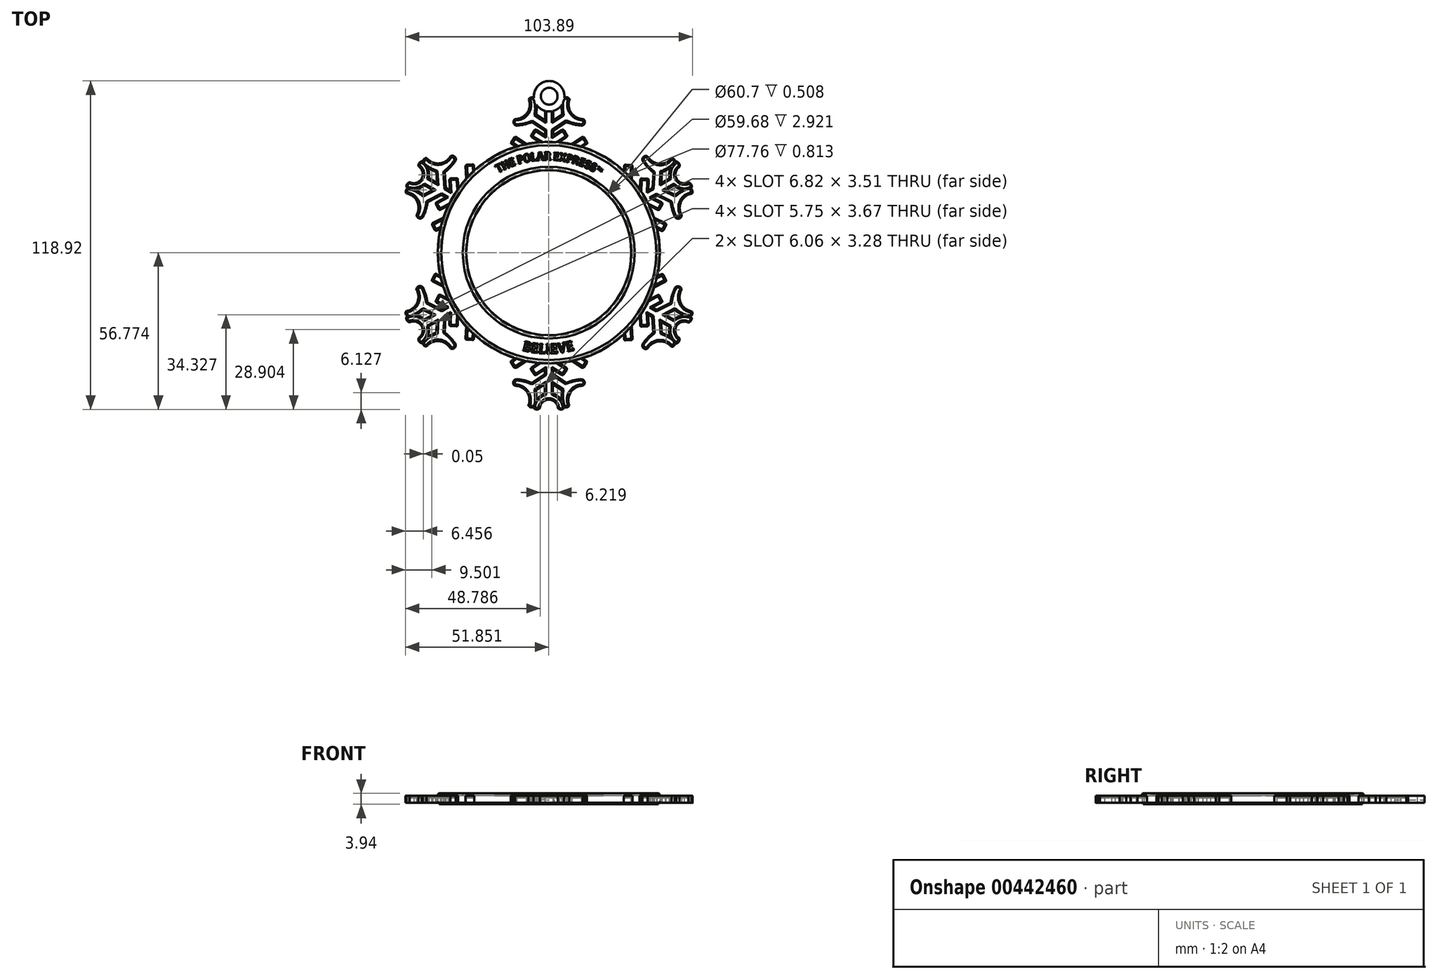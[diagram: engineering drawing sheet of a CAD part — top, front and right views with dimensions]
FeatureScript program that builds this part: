
annotation { "Feature Type Name" : "Feature", "Feature Type Description" : "" }
export const myFeature = defineFeature(function(context is Context, id is Id, definition is map)
    precondition{}
    {
        {
            var Q0;
            Q0=qCreatedBy(makeId("Top.planeOp"),FACE);
            var sketch = newSketch(context, id + "F0", { "sketchPlane" : qUnion([Q0])});
            skLineSegment(sketch, "E0.bottom", {"start": v(-89.67, 62.48) * mm, "end": v(13.76, 62.48) * mm});
            skLineSegment(sketch, "E0.top", {"start": v(-89.67, -44.14) * mm, "end": v(13.76, -44.14) * mm});
            skLineSegment(sketch, "E0.left", {"start": v(-89.67, 62.48) * mm, "end": v(-89.67, -44.14) * mm});
            skLineSegment(sketch, "E0.right", {"start": v(13.76, 62.48) * mm, "end": v(13.76, -44.14) * mm});
            skSolve(sketch);
        }
        {
            var Q0;
            Q0=makeQuery(id+"F0.imprint","IMPRINT",FACE,{"disambiguationData":[TD([[makeQuery(id+"F0.imprint","IMPRINT",EDGE,{"derivedFrom":sQuery(id+"F0.wireOp",EDGE,"E0.bottom")}),-1.0]])]});
            var sketch = newSketch(context, id + "F1", { "sketchPlane" : qUnion([Q0])});
            skLineSegment(sketch, "E1", {"start": v(-37.72, -43.99) * mm, "end": v(-37.72, 64.24) * mm});
            skLineSegment(sketch, "E2", {"start": v(-50.86, -34.68) * mm, "end": v(-48.2, -32.93) * mm});
            skLineSegment(sketch, "E3", {"start": v(-48.2, -32.93) * mm, "end": v(-37.72, -32.93) * mm});
            skLineSegment(sketch, "E4", {"start": v(-49.18, -37.24) * mm, "end": v(-45.3, -34.68) * mm});
            skLineSegment(sketch, "E5", {"start": v(-45.3, -34.68) * mm, "end": v(-41.3, -35.15) * mm});
            skLineSegment(sketch, "E6", {"start": v(-41.3, -35.15) * mm, "end": v(-41.47, -35.86) * mm});
            skLineSegment(sketch, "E7", {"start": v(-41.47, -35.86) * mm, "end": v(-43.84, -37.4) * mm});
            skLineSegment(sketch, "E8", {"start": v(-42.17, -39.97) * mm, "end": v(-39.2, -38.03) * mm});
            skLineSegment(sketch, "E9", {"start": v(-39.2, -38.03) * mm, "end": v(-39.2, -39.79) * mm});
            skLineSegment(sketch, "E10", {"start": v(-39.2, -39.79) * mm, "end": v(-43.97, -42.95) * mm});
            skLineSegment(sketch, "E11", {"start": v(-50.86, -34.68) * mm, "end": v(-51.7, -35.23) * mm});
            skLineSegment(sketch, "E12", {"start": v(-49.18, -37.24) * mm, "end": v(-50.01, -37.79) * mm});
            skLineSegment(sketch, "E13", {"start": v(-51.7, -35.23) * mm, "end": v(-50.01, -37.79) * mm});
            skLineSegment(sketch, "E14", {"start": v(-43.84, -37.4) * mm, "end": v(-44.45, -37.8) * mm});
            skLineSegment(sketch, "E15", {"start": v(-44.45, -37.8) * mm, "end": v(-42.8, -40.34) * mm});
            skLineSegment(sketch, "E16", {"start": v(-42.17, -39.97) * mm, "end": v(-42.78, -40.37) * mm});
            skLineSegment(sketch, "E17", {"start": v(-42.8, -40.34) * mm, "end": v(-42.78, -40.37) * mm});
            skLineSegment(sketch, "E18.trimOffspring", {"start": v(-39.2, -43.46) * mm, "end": v(-39.2, -46.98) * mm});
            skArc(sketch, "E19", {"start": v(-39.2, -46.98) * mm, "mid": v(-41.06, -47.9) * mm, "end": v(-42.34, -49.52) * mm});
            skLineSegment(sketch, "E20", {"start": v(-37.72, -43.99) * mm, "end": v(-37.72, -49.05) * mm});
            skArc(sketch, "E21", {"start": v(-37.72, -49.05) * mm, "mid": v(-39.97, -49.95) * mm, "end": v(-40.99, -52.14) * mm});
            skArc(sketch, "E22", {"start": v(-45.12, -51.18) * mm, "mid": v(-45.67, -46.32) * mm, "end": v(-50, -44.04) * mm});
            skLineSegment(sketch, "E23", {"start": v(-39.2, -43.46) * mm, "end": v(-42.47, -45.63) * mm});
            skArc(sketch, "E24", {"start": v(-42.34, -49.52) * mm, "mid": v(-42.28, -47.57) * mm, "end": v(-42.47, -45.63) * mm});
            skArc(sketch, "E25", {"start": v(-43.97, -42.95) * mm, "mid": v(-46.67, -42.07) * mm, "end": v(-49.48, -41.65) * mm});
            skArc(sketch, "E26", {"start": v(-49.48, -41.65) * mm, "mid": v(-50.63, -42.65) * mm, "end": v(-50, -44.04) * mm});
            skArc(sketch, "E27", {"start": v(-45.12, -51.18) * mm, "mid": v(-44.22, -51.87) * mm, "end": v(-43.13, -51.55) * mm});
            skLineSegment(sketch, "E28", {"start": v(-43.13, -51.55) * mm, "end": v(-43.23, -52.11) * mm});
            skArc(sketch, "E29", {"start": v(-43.23, -52.11) * mm, "mid": v(-42.12, -52.62) * mm, "end": v(-40.99, -52.14) * mm});
            skSolve(sketch);
        }
        {
            var Q0;
            Q0 = qSketchRegion(id + "F1", true);
            extrude(context, id + "F2", {"entities" : qUnion([Q0]), "depth" : 1.52 * mm});
        }
        {
            var Q0;
            Q0=makeQuery(id+"F2.opExtrude","SWEPT_EDGE",EDGE,{"disambiguationData":[OSD([sQuery(id+"F1.wireOp",EDGE,"E11"),sQuery(id+"F1.wireOp",EDGE,"E13")])]});
            var Q1;
            Q1=makeQuery(id+"F2.opExtrude","SWEPT_EDGE",EDGE,{"disambiguationData":[OSD([sQuery(id+"F1.wireOp",EDGE,"E12"),sQuery(id+"F1.wireOp",EDGE,"E13")])]});
            var Q2;
            Q2=makeQuery(id+"F2.opExtrude","SWEPT_EDGE",EDGE,{"disambiguationData":[OSD([sQuery(id+"F1.wireOp",EDGE,"E14"),sQuery(id+"F1.wireOp",EDGE,"E15")])]});
            var Q3;
            Q3=makeQuery(id+"F2.opExtrude","SWEPT_EDGE",EDGE,{"disambiguationData":[OSD([sQuery(id+"F1.wireOp",EDGE,"E16"),sQuery(id+"F1.wireOp",EDGE,"E17")])]});
            fillet(context, id + "F3", {"entities" : qUnion([Q0, Q1, Q2, Q3]), "radius" : 0.5 * mm, "tangentPropagation" : true, "allowEdgeOverflow" : false});
        }
        {
            var Q0;
            Q0=makeQuery(id+"F2.opExtrude","SWEPT_BODY",BODY,{"disambiguationData":[OSD([sQuery(id+"F1.wireOp",EDGE,"E1"),sQuery(id+"F1.wireOp",EDGE,"E2"),sQuery(id+"F1.wireOp",EDGE,"E3"),sQuery(id+"F1.wireOp",EDGE,"E4"),sQuery(id+"F1.wireOp",EDGE,"E5"),sQuery(id+"F1.wireOp",EDGE,"E6"),sQuery(id+"F1.wireOp",EDGE,"E7"),sQuery(id+"F1.wireOp",EDGE,"E8"),sQuery(id+"F1.wireOp",EDGE,"E9"),sQuery(id+"F1.wireOp",EDGE,"E10"),sQuery(id+"F1.wireOp",EDGE,"E11"),sQuery(id+"F1.wireOp",EDGE,"E12"),sQuery(id+"F1.wireOp",EDGE,"E13"),sQuery(id+"F1.wireOp",EDGE,"E14"),sQuery(id+"F1.wireOp",EDGE,"E15"),sQuery(id+"F1.wireOp",EDGE,"E16"),sQuery(id+"F1.wireOp",EDGE,"E17"),sQuery(id+"F1.wireOp",EDGE,"E18.trimOffspring"),sQuery(id+"F1.wireOp",EDGE,"E19"),sQuery(id+"F1.wireOp",EDGE,"E20"),sQuery(id+"F1.wireOp",EDGE,"E21"),sQuery(id+"F1.wireOp",EDGE,"E22"),sQuery(id+"F1.wireOp",EDGE,"E23"),sQuery(id+"F1.wireOp",EDGE,"E24"),sQuery(id+"F1.wireOp",EDGE,"E25"),sQuery(id+"F1.wireOp",EDGE,"E26"),sQuery(id+"F1.wireOp",EDGE,"E27"),sQuery(id+"F1.wireOp",EDGE,"E28"),sQuery(id+"F1.wireOp",EDGE,"E29")])]});
            var Q1;
            Q1=makeQuery(id+"F2.opExtrude","SWEPT_FACE",FACE,{"disambiguationData":[OSD([sQuery(id+"F1.wireOp",EDGE,"E1"),sQuery(id+"F1.wireOp",EDGE,"E20")])]});
            mirror(context, id + "F4", {"operationType" : NewBodyOperationType.ADD, "entities" : qUnion([Q0]), "mirrorPlane" : qUnion([Q1])});
        }
        {
            var Q0;
            {var subQ0=makeQuery(id+"F2.opExtrude","CAP_FACE",FACE,{"disambiguationData":[OSD([sQuery(id+"F1.wireOp",EDGE,"E1"),sQuery(id+"F1.wireOp",EDGE,"E2"),sQuery(id+"F1.wireOp",EDGE,"E3"),sQuery(id+"F1.wireOp",EDGE,"E4"),sQuery(id+"F1.wireOp",EDGE,"E5"),sQuery(id+"F1.wireOp",EDGE,"E6"),sQuery(id+"F1.wireOp",EDGE,"E7"),sQuery(id+"F1.wireOp",EDGE,"E8"),sQuery(id+"F1.wireOp",EDGE,"E9"),sQuery(id+"F1.wireOp",EDGE,"E10"),sQuery(id+"F1.wireOp",EDGE,"E11"),sQuery(id+"F1.wireOp",EDGE,"E12"),sQuery(id+"F1.wireOp",EDGE,"E13"),sQuery(id+"F1.wireOp",EDGE,"E14"),sQuery(id+"F1.wireOp",EDGE,"E15"),sQuery(id+"F1.wireOp",EDGE,"E16"),sQuery(id+"F1.wireOp",EDGE,"E17"),sQuery(id+"F1.wireOp",EDGE,"E18.trimOffspring"),sQuery(id+"F1.wireOp",EDGE,"E19"),sQuery(id+"F1.wireOp",EDGE,"E20"),sQuery(id+"F1.wireOp",EDGE,"E21"),sQuery(id+"F1.wireOp",EDGE,"E22"),sQuery(id+"F1.wireOp",EDGE,"E23"),sQuery(id+"F1.wireOp",EDGE,"E24"),sQuery(id+"F1.wireOp",EDGE,"E25"),sQuery(id+"F1.wireOp",EDGE,"E26"),sQuery(id+"F1.wireOp",EDGE,"E27"),sQuery(id+"F1.wireOp",EDGE,"E28"),sQuery(id+"F1.wireOp",EDGE,"E29")])],"isStart":false});Q0=makeQuery(id+"F4.boolean.opBoolean","MERGE",FACE,{"derivedFrom":[subQ0,makeQuery(id+"F4.opPattern","COPY",FACE,{"derivedFrom":subQ0,"instanceName":"1"})]});}
            var sketch = newSketch(context, id + "F5", { "sketchPlane" : qUnion([Q0])});
            skLineSegment(sketch, "E30", {"start": v(-38.68, -37.09) * mm, "end": v(-38.68, -40.03) * mm});
            skLineSegment(sketch, "E31", {"start": v(-38.68, -47.34) * mm, "end": v(-38.68, -42.57) * mm});
            skLineSegment(sketch, "E32", {"start": v(-38.68, -40.03) * mm, "end": v(-43.93, -43.46) * mm});
            skLineSegment(sketch, "E33", {"start": v(-38.68, -42.57) * mm, "end": v(-42.98, -45.42) * mm});
            skLineSegment(sketch, "E34", {"start": v(-40.7, -35.88) * mm, "end": v(-43.4, -37.66) * mm});
            skLineSegment(sketch, "E35", {"start": v(-43.4, -37.66) * mm, "end": v(-43.77, -37.9) * mm});
            skLineSegment(sketch, "E36", {"start": v(-43.77, -37.9) * mm, "end": v(-42.61, -39.7) * mm});
            skLineSegment(sketch, "E37", {"start": v(-38.68, -37.09) * mm, "end": v(-42.61, -39.7) * mm});
            skLineSegment(sketch, "E38.trimOffspring", {"start": v(-38.68, -42.57) * mm, "end": v(-38.68, -47.34) * mm});
            skArc(sketch, "E39", {"start": v(-43.93, -43.46) * mm, "mid": v(-46.6, -42.57) * mm, "end": v(-49.38, -42.12) * mm});
            skArc(sketch, "E40", {"start": v(-49.38, -42.12) * mm, "mid": v(-50.03, -42.74) * mm, "end": v(-49.71, -43.58) * mm});
            skArc(sketch, "E41", {"start": v(-42.9, -50.88) * mm, "mid": v(-42.7, -48.15) * mm, "end": v(-42.98, -45.42) * mm});
            skArc(sketch, "E42", {"start": v(-44.52, -51) * mm, "mid": v(-45.27, -46) * mm, "end": v(-49.71, -43.58) * mm});
            skArc(sketch, "E43", {"start": v(-44.52, -51) * mm, "mid": v(-43.68, -51.33) * mm, "end": v(-42.9, -50.88) * mm});
            skArc(sketch, "E44", {"start": v(-37.76, -48.56) * mm, "mid": v(-40.27, -49.56) * mm, "end": v(-41.5, -51.96) * mm});
            skArc(sketch, "E45", {"start": v(-38.68, -47.34) * mm, "mid": v(-41.04, -48.47) * mm, "end": v(-42.51, -50.63) * mm});
            skArc(sketch, "E46", {"start": v(-42.72, -51.96) * mm, "mid": v(-42.11, -52.15) * mm, "end": v(-41.5, -51.96) * mm});
            skArc(sketch, "E47", {"start": v(-42.51, -50.63) * mm, "mid": v(-42.65, -51.3) * mm, "end": v(-42.72, -51.96) * mm});
            skLineSegment(sketch, "E48", {"start": v(-49.87, -37.08) * mm, "end": v(-45.7, -34.34) * mm});
            skLineSegment(sketch, "E49", {"start": v(-45.7, -34.34) * mm, "end": v(-48.36, -33.8) * mm});
            skLineSegment(sketch, "E50", {"start": v(-48.36, -33.8) * mm, "end": v(-48.45, -33.67) * mm});
            skLineSegment(sketch, "E51", {"start": v(-49.87, -37.08) * mm, "end": v(-51, -35.37) * mm});
            skLineSegment(sketch, "E52", {"start": v(-51, -35.37) * mm, "end": v(-48.45, -33.67) * mm});
            skLineSegment(sketch, "E53", {"start": v(-37.76, -48.56) * mm, "end": v(-37.58, -34.16) * mm});
            skLineSegment(sketch, "E54", {"start": v(-37.58, -34.16) * mm, "end": v(-40.7, -35.88) * mm});
            skSolve(sketch);
        }
        {
            var Q0;
            Q0 = qSketchRegion(id + "F5", true);
            extrude(context, id + "F6", {"entities" : qUnion([Q0]), "operationType" : NewBodyOperationType.REMOVE, "oppositeDirection" : true, "depth" : 0.76 * mm});
        }
        {
            var Q0;
            {var subQ0=makeQuery(id+"F2.opExtrude","CAP_FACE",FACE,{"disambiguationData":[OSD([sQuery(id+"F1.wireOp",EDGE,"E1"),sQuery(id+"F1.wireOp",EDGE,"E2"),sQuery(id+"F1.wireOp",EDGE,"E3"),sQuery(id+"F1.wireOp",EDGE,"E4"),sQuery(id+"F1.wireOp",EDGE,"E5"),sQuery(id+"F1.wireOp",EDGE,"E6"),sQuery(id+"F1.wireOp",EDGE,"E7"),sQuery(id+"F1.wireOp",EDGE,"E8"),sQuery(id+"F1.wireOp",EDGE,"E9"),sQuery(id+"F1.wireOp",EDGE,"E10"),sQuery(id+"F1.wireOp",EDGE,"E11"),sQuery(id+"F1.wireOp",EDGE,"E12"),sQuery(id+"F1.wireOp",EDGE,"E13"),sQuery(id+"F1.wireOp",EDGE,"E14"),sQuery(id+"F1.wireOp",EDGE,"E15"),sQuery(id+"F1.wireOp",EDGE,"E16"),sQuery(id+"F1.wireOp",EDGE,"E17"),sQuery(id+"F1.wireOp",EDGE,"E18.trimOffspring"),sQuery(id+"F1.wireOp",EDGE,"E19"),sQuery(id+"F1.wireOp",EDGE,"E20"),sQuery(id+"F1.wireOp",EDGE,"E21"),sQuery(id+"F1.wireOp",EDGE,"E22"),sQuery(id+"F1.wireOp",EDGE,"E23"),sQuery(id+"F1.wireOp",EDGE,"E24"),sQuery(id+"F1.wireOp",EDGE,"E25"),sQuery(id+"F1.wireOp",EDGE,"E26"),sQuery(id+"F1.wireOp",EDGE,"E27"),sQuery(id+"F1.wireOp",EDGE,"E28"),sQuery(id+"F1.wireOp",EDGE,"E29")])],"isStart":false});Q0=makeQuery(id+"F4.boolean.opBoolean","MERGE",FACE,{"derivedFrom":[subQ0,makeQuery(id+"F4.opPattern","COPY",FACE,{"derivedFrom":subQ0,"instanceName":"1"})]});}
            var sketch = newSketch(context, id + "F7", { "sketchPlane" : qUnion([Q0])});
            skLineSegment(sketch, "E55", {"start": v(-37.58, -34.16) * mm, "end": v(-31.7, -37.88) * mm});
            skLineSegment(sketch, "E56", {"start": v(-31.7, -37.88) * mm, "end": v(-32.82, -39.66) * mm});
            skLineSegment(sketch, "E57", {"start": v(-32.82, -39.66) * mm, "end": v(-36.7, -37.23) * mm});
            skLineSegment(sketch, "E58.right", {"start": v(-36.7, -37.23) * mm, "end": v(-36.7, -40.03) * mm});
            skPoint(sketch, "E59.start.orphan", {"position": v(-37.58, -36.67) * mm});
            skLineSegment(sketch, "E60", {"start": v(-37.76, -47.63) * mm, "end": v(-38.17, -35.66) * mm});
            skLineSegment(sketch, "E61", {"start": v(-38.17, -35.66) * mm, "end": v(-37.58, -34.16) * mm});
            skLineSegment(sketch, "E62", {"start": v(-36.7, -40.03) * mm, "end": v(-31.5, -43.46) * mm});
            skPoint(sketch, "E63.end.orphan", {"position": v(-36.25, -42.3) * mm});
            skPoint(sketch, "E64.end.orphan", {"position": v(-36.7, -42.95) * mm});
            skLineSegment(sketch, "E65", {"start": v(-36.7, -42.58) * mm, "end": v(-32.35, -45.36) * mm});
            skArc(sketch, "E66", {"start": v(-26.04, -42.12) * mm, "mid": v(-28.85, -42.5) * mm, "end": v(-31.5, -43.46) * mm});
            skArc(sketch, "E67", {"start": v(-32.35, -45.36) * mm, "mid": v(-32.64, -48.26) * mm, "end": v(-32.07, -51.11) * mm});
            skArc(sketch, "E68", {"start": v(-25.6, -43.58) * mm, "mid": v(-25.28, -42.69) * mm, "end": v(-26.04, -42.12) * mm});
            skArc(sketch, "E69", {"start": v(-32.07, -51.11) * mm, "mid": v(-31.44, -51.43) * mm, "end": v(-30.9, -50.98) * mm});
            skArc(sketch, "E70", {"start": v(-25.6, -43.58) * mm, "mid": v(-30.18, -45.9) * mm, "end": v(-30.9, -50.98) * mm});
            skLineSegment(sketch, "E71", {"start": v(-41.5, -51.96) * mm, "end": v(-29.9, -51.96) * mm});
            skArc(sketch, "E72", {"start": v(-34.1, -51.96) * mm, "mid": v(-35.24, -49.51) * mm, "end": v(-37.76, -48.56) * mm});
            skLineSegment(sketch, "E73", {"start": v(-38.68, -47.34) * mm, "end": v(-37.77, -47.34) * mm});
            skArc(sketch, "E74", {"start": v(-32.7, -51.96) * mm, "mid": v(-34.01, -49.06) * mm, "end": v(-36.7, -47.34) * mm});
            skArc(sketch, "E75", {"start": v(-34.1, -51.96) * mm, "mid": v(-33.4, -52.23) * mm, "end": v(-32.7, -51.96) * mm});
            skLineSegment(sketch, "E76.trimOffspring", {"start": v(-36.7, -42.58) * mm, "end": v(-36.7, -47.34) * mm});
            skLineSegment(sketch, "E77", {"start": v(-29.73, -34.22) * mm, "end": v(-25.56, -36.96) * mm});
            skLineSegment(sketch, "E78", {"start": v(-25.56, -36.96) * mm, "end": v(-24.45, -35.37) * mm});
            skLineSegment(sketch, "E79", {"start": v(-24.45, -35.37) * mm, "end": v(-27.72, -33.27) * mm});
            skLineSegment(sketch, "E80", {"start": v(-27.72, -33.27) * mm, "end": v(-29.73, -34.22) * mm});
            skSolve(sketch);
        }
        {
            var Q0;
            Q0 = qSketchRegion(id + "F7", true);
            var Q1;
            Q1=makeQuery(id+"F7.imprint","IMPRINT",FACE,{"disambiguationData":[TD([[makeQuery(id+"F7.imprint","IMPRINT",EDGE,{"derivedFrom":sQuery(id+"F7.wireOp",EDGE,"E55")}),-1.0]])]});
            extrude(context, id + "F8", {"entities" : qUnion([Q0, Q1]), "operationType" : NewBodyOperationType.REMOVE, "oppositeDirection" : true, "depth" : 0.76 * mm});
        }
        {
            var Q0;
            Q0=makeQuery(id+"F8.boolean.opBoolean","COPY",EDGE,{"derivedFrom":makeQuery(id+"F8.opExtrude","SWEPT_EDGE",EDGE,{"disambiguationData":[OSD([sQuery(id+"F7.wireOp",EDGE,"E78"),sQuery(id+"F7.wireOp",EDGE,"E79")])]})});
            var Q1;
            Q1=makeQuery(id+"F8.boolean.opBoolean","COPY",EDGE,{"derivedFrom":makeQuery(id+"F8.opExtrude","SWEPT_EDGE",EDGE,{"disambiguationData":[OSD([sQuery(id+"F7.wireOp",EDGE,"E77"),sQuery(id+"F7.wireOp",EDGE,"E78")])]})});
            var Q2;
            Q2=makeQuery(id+"F6.boolean.opBoolean","COPY",EDGE,{"derivedFrom":makeQuery(id+"F6.opExtrude","SWEPT_EDGE",EDGE,{"disambiguationData":[OSD([sQuery(id+"F5.wireOp",EDGE,"E51"),sQuery(id+"F5.wireOp",EDGE,"E52")])]})});
            var Q3;
            Q3=makeQuery(id+"F6.boolean.opBoolean","COPY",EDGE,{"derivedFrom":makeQuery(id+"F6.opExtrude","SWEPT_EDGE",EDGE,{"disambiguationData":[OSD([sQuery(id+"F5.wireOp",EDGE,"E48"),sQuery(id+"F5.wireOp",EDGE,"E51")])]})});
            var Q4;
            Q4=makeQuery(id+"F6.boolean.opBoolean","COPY",EDGE,{"derivedFrom":makeQuery(id+"F6.opExtrude","SWEPT_EDGE",EDGE,{"disambiguationData":[OSD([sQuery(id+"F5.wireOp",EDGE,"E35"),sQuery(id+"F5.wireOp",EDGE,"E36")])]})});
            var Q5;
            Q5=makeQuery(id+"F6.boolean.opBoolean","COPY",EDGE,{"derivedFrom":makeQuery(id+"F6.opExtrude","SWEPT_EDGE",EDGE,{"disambiguationData":[OSD([sQuery(id+"F5.wireOp",EDGE,"E36"),sQuery(id+"F5.wireOp",EDGE,"E37")])]})});
            var Q6;
            Q6=makeQuery(id+"F8.boolean.opBoolean","COPY",EDGE,{"derivedFrom":makeQuery(id+"F8.opExtrude","SWEPT_EDGE",EDGE,{"disambiguationData":[OSD([sQuery(id+"F7.wireOp",EDGE,"E55"),sQuery(id+"F7.wireOp",EDGE,"E56")])]})});
            var Q7;
            Q7=makeQuery(id+"F8.boolean.opBoolean","COPY",EDGE,{"derivedFrom":makeQuery(id+"F8.opExtrude","SWEPT_EDGE",EDGE,{"disambiguationData":[OSD([sQuery(id+"F7.wireOp",EDGE,"E56"),sQuery(id+"F7.wireOp",EDGE,"E57")])]})});
            fillet(context, id + "F9", {"entities" : qUnion([Q0, Q1, Q2, Q3, Q4, Q5, Q6, Q7]), "radius" : 0.5 * mm, "tangentPropagation" : true, "allowEdgeOverflow" : false});
        }
        {
            var Q0;
            Q0=makeQuery(id+"F2.opExtrude","SWEPT_FACE",FACE,{"disambiguationData":[OSD([sQuery(id+"F1.wireOp",EDGE,"E9")])]});
            cPlane(context, id + "F10", {"entities" : qUnion([Q0]), "cplaneType" : CPlaneType.OFFSET, "offset" : 1.52 * mm, "oppositeDirection" : true, "width" : 152.4 * mm, "height" : 152.4 * mm});
        }
        {
            var Q0;
            Q0=qCreatedBy(id+"F10.planeOp",FACE);
            var sketch = newSketch(context, id + "F11", { "sketchPlane" : qUnion([Q0])});
            skLineSegment(sketch, "E81", {"start": v(-4.25, 0) * mm, "end": v(-4.25, 7.93) * mm});
            skSolve(sketch);
        }
        {
            var Q0;
            Q0=makeQuery(id+"F2.opExtrude","SWEPT_BODY",BODY,{"disambiguationData":[OSD([sQuery(id+"F1.wireOp",EDGE,"E1"),sQuery(id+"F1.wireOp",EDGE,"E2"),sQuery(id+"F1.wireOp",EDGE,"E3"),sQuery(id+"F1.wireOp",EDGE,"E4"),sQuery(id+"F1.wireOp",EDGE,"E5"),sQuery(id+"F1.wireOp",EDGE,"E6"),sQuery(id+"F1.wireOp",EDGE,"E7"),sQuery(id+"F1.wireOp",EDGE,"E8"),sQuery(id+"F1.wireOp",EDGE,"E9"),sQuery(id+"F1.wireOp",EDGE,"E10"),sQuery(id+"F1.wireOp",EDGE,"E11"),sQuery(id+"F1.wireOp",EDGE,"E12"),sQuery(id+"F1.wireOp",EDGE,"E13"),sQuery(id+"F1.wireOp",EDGE,"E14"),sQuery(id+"F1.wireOp",EDGE,"E15"),sQuery(id+"F1.wireOp",EDGE,"E16"),sQuery(id+"F1.wireOp",EDGE,"E17"),sQuery(id+"F1.wireOp",EDGE,"E18.trimOffspring"),sQuery(id+"F1.wireOp",EDGE,"E19"),sQuery(id+"F1.wireOp",EDGE,"E20"),sQuery(id+"F1.wireOp",EDGE,"E21"),sQuery(id+"F1.wireOp",EDGE,"E22"),sQuery(id+"F1.wireOp",EDGE,"E23"),sQuery(id+"F1.wireOp",EDGE,"E24"),sQuery(id+"F1.wireOp",EDGE,"E25"),sQuery(id+"F1.wireOp",EDGE,"E26"),sQuery(id+"F1.wireOp",EDGE,"E27"),sQuery(id+"F1.wireOp",EDGE,"E28"),sQuery(id+"F1.wireOp",EDGE,"E29")])]});
            var Q1;
            Q1=sQuery(id+"F11.wireOp",EDGE,"E81");
            circularPattern(context, id + "F12", {"entities" : qUnion([Q0]), "axis" : qUnion([Q1]), "angle" : 360 * degree, "instanceCount" : 6, "equalSpace" : true});
        }
        {
            var Q0;
            {var subQ0=makeQuery(id+"F2.opExtrude","CAP_FACE",FACE,{"disambiguationData":[OSD([sQuery(id+"F1.wireOp",EDGE,"E1"),sQuery(id+"F1.wireOp",EDGE,"E2"),sQuery(id+"F1.wireOp",EDGE,"E3"),sQuery(id+"F1.wireOp",EDGE,"E4"),sQuery(id+"F1.wireOp",EDGE,"E5"),sQuery(id+"F1.wireOp",EDGE,"E6"),sQuery(id+"F1.wireOp",EDGE,"E7"),sQuery(id+"F1.wireOp",EDGE,"E8"),sQuery(id+"F1.wireOp",EDGE,"E9"),sQuery(id+"F1.wireOp",EDGE,"E10"),sQuery(id+"F1.wireOp",EDGE,"E11"),sQuery(id+"F1.wireOp",EDGE,"E12"),sQuery(id+"F1.wireOp",EDGE,"E13"),sQuery(id+"F1.wireOp",EDGE,"E14"),sQuery(id+"F1.wireOp",EDGE,"E15"),sQuery(id+"F1.wireOp",EDGE,"E16"),sQuery(id+"F1.wireOp",EDGE,"E17"),sQuery(id+"F1.wireOp",EDGE,"E18.trimOffspring"),sQuery(id+"F1.wireOp",EDGE,"E19"),sQuery(id+"F1.wireOp",EDGE,"E20"),sQuery(id+"F1.wireOp",EDGE,"E21"),sQuery(id+"F1.wireOp",EDGE,"E22"),sQuery(id+"F1.wireOp",EDGE,"E23"),sQuery(id+"F1.wireOp",EDGE,"E24"),sQuery(id+"F1.wireOp",EDGE,"E25"),sQuery(id+"F1.wireOp",EDGE,"E26"),sQuery(id+"F1.wireOp",EDGE,"E27"),sQuery(id+"F1.wireOp",EDGE,"E28"),sQuery(id+"F1.wireOp",EDGE,"E29")])],"isStart":false});Q0=makeQuery(id+"F12.opPattern","COPY",FACE,{"derivedFrom":makeQuery(id+"F4.boolean.opBoolean","MERGE",FACE,{"derivedFrom":[subQ0,makeQuery(id+"F4.opPattern","COPY",FACE,{"derivedFrom":subQ0,"instanceName":"1"})]}),"instanceName":"3"});}
            var sketch = newSketch(context, id + "F13", { "sketchPlane" : qUnion([Q0])});
            skLineSegment(sketch, "E82", {"start": v(-37.77, 42.66) * mm, "end": v(-37.77, -34.35) * mm});
            skCircle(sketch, "E83", {"center": v(-37.77, 4.15) * mm, "radius": 40.15 * mm});
            skSolve(sketch);
        }
        {
            var Q0;
            Q0 = qSketchRegion(id + "F13", true);
            extrude(context, id + "F14", {"entities" : qUnion([Q0]), "depth" : 1.9 * mm, "hasSecondDirection" : true, "secondDirectionOppositeDirection" : true, "secondDirectionDepth" : 1.52 * mm});
        }
        {
            var Q0;
            {var subQ0=makeQuery(id+"F2.opExtrude","CAP_FACE",FACE,{"disambiguationData":[OSD([sQuery(id+"F1.wireOp",EDGE,"E1"),sQuery(id+"F1.wireOp",EDGE,"E2"),sQuery(id+"F1.wireOp",EDGE,"E3"),sQuery(id+"F1.wireOp",EDGE,"E4"),sQuery(id+"F1.wireOp",EDGE,"E5"),sQuery(id+"F1.wireOp",EDGE,"E6"),sQuery(id+"F1.wireOp",EDGE,"E7"),sQuery(id+"F1.wireOp",EDGE,"E8"),sQuery(id+"F1.wireOp",EDGE,"E9"),sQuery(id+"F1.wireOp",EDGE,"E10"),sQuery(id+"F1.wireOp",EDGE,"E11"),sQuery(id+"F1.wireOp",EDGE,"E12"),sQuery(id+"F1.wireOp",EDGE,"E13"),sQuery(id+"F1.wireOp",EDGE,"E14"),sQuery(id+"F1.wireOp",EDGE,"E15"),sQuery(id+"F1.wireOp",EDGE,"E16"),sQuery(id+"F1.wireOp",EDGE,"E17"),sQuery(id+"F1.wireOp",EDGE,"E18.trimOffspring"),sQuery(id+"F1.wireOp",EDGE,"E19"),sQuery(id+"F1.wireOp",EDGE,"E20"),sQuery(id+"F1.wireOp",EDGE,"E21"),sQuery(id+"F1.wireOp",EDGE,"E22"),sQuery(id+"F1.wireOp",EDGE,"E23"),sQuery(id+"F1.wireOp",EDGE,"E24"),sQuery(id+"F1.wireOp",EDGE,"E25"),sQuery(id+"F1.wireOp",EDGE,"E26"),sQuery(id+"F1.wireOp",EDGE,"E27"),sQuery(id+"F1.wireOp",EDGE,"E28"),sQuery(id+"F1.wireOp",EDGE,"E29")])],"isStart":false});Q0=makeQuery(id+"F12.opPattern","COPY",FACE,{"derivedFrom":makeQuery(id+"F4.boolean.opBoolean","MERGE",FACE,{"derivedFrom":[subQ0,makeQuery(id+"F4.opPattern","COPY",FACE,{"derivedFrom":subQ0,"instanceName":"1"})]}),"instanceName":"3"});}
            var sketch = newSketch(context, id + "F15", { "sketchPlane" : qUnion([Q0])});
            skCircle(sketch, "E84", {"center": v(-37.62, 60.79) * mm, "radius": 5.51 * mm});
            skPoint(sketch, "E84.first.point", {"position": v(-43.13, 60.6) * mm});
            skPoint(sketch, "E84.second.point", {"position": v(-32.11, 60.6) * mm});
            skPoint(sketch, "E84.third.point", {"position": v(-39.1, 55.48) * mm});
            skSolve(sketch);
        }
        {
            var Q0;
            Q0 = qSketchRegion(id + "F15", true);
            extrude(context, id + "F16", {"entities" : qUnion([Q0]), "operationType" : NewBodyOperationType.ADD, "oppositeDirection" : true, "depth" : 1.52 * mm});
        }
        {
            var Q0;
            {var subQ0=makeQuery(id+"F2.opExtrude","CAP_FACE",FACE,{"disambiguationData":[OSD([sQuery(id+"F1.wireOp",EDGE,"E1"),sQuery(id+"F1.wireOp",EDGE,"E2"),sQuery(id+"F1.wireOp",EDGE,"E3"),sQuery(id+"F1.wireOp",EDGE,"E4"),sQuery(id+"F1.wireOp",EDGE,"E5"),sQuery(id+"F1.wireOp",EDGE,"E6"),sQuery(id+"F1.wireOp",EDGE,"E7"),sQuery(id+"F1.wireOp",EDGE,"E8"),sQuery(id+"F1.wireOp",EDGE,"E9"),sQuery(id+"F1.wireOp",EDGE,"E10"),sQuery(id+"F1.wireOp",EDGE,"E11"),sQuery(id+"F1.wireOp",EDGE,"E12"),sQuery(id+"F1.wireOp",EDGE,"E13"),sQuery(id+"F1.wireOp",EDGE,"E14"),sQuery(id+"F1.wireOp",EDGE,"E15"),sQuery(id+"F1.wireOp",EDGE,"E16"),sQuery(id+"F1.wireOp",EDGE,"E17"),sQuery(id+"F1.wireOp",EDGE,"E18.trimOffspring"),sQuery(id+"F1.wireOp",EDGE,"E19"),sQuery(id+"F1.wireOp",EDGE,"E20"),sQuery(id+"F1.wireOp",EDGE,"E21"),sQuery(id+"F1.wireOp",EDGE,"E22"),sQuery(id+"F1.wireOp",EDGE,"E23"),sQuery(id+"F1.wireOp",EDGE,"E24"),sQuery(id+"F1.wireOp",EDGE,"E25"),sQuery(id+"F1.wireOp",EDGE,"E26"),sQuery(id+"F1.wireOp",EDGE,"E27"),sQuery(id+"F1.wireOp",EDGE,"E28"),sQuery(id+"F1.wireOp",EDGE,"E29")])],"isStart":false});Q0=makeQuery(id+"F16.boolean.opBoolean","MERGE",FACE,{"derivedFrom":[makeQuery(id+"F12.opPattern","COPY",FACE,{"derivedFrom":makeQuery(id+"F4.boolean.opBoolean","MERGE",FACE,{"derivedFrom":[subQ0,makeQuery(id+"F4.opPattern","COPY",FACE,{"derivedFrom":subQ0,"instanceName":"1"})]}),"instanceName":"3"}),makeQuery(id+"F16.opExtrude","CAP_FACE",FACE,{"disambiguationData":[OSD([sQuery(id+"F15.wireOp",EDGE,"E84")])],"isStart":true})]});}
            var sketch = newSketch(context, id + "F17", { "sketchPlane" : qUnion([Q0])});
            skPoint(sketch, "E85.first.point", {"position": v(-40.63, 65.4) * mm});
            skPoint(sketch, "E85.second.point", {"position": v(-34.78, 56.05) * mm});
            skCircle(sketch, "E86", {"center": v(-37.63, 60.78) * mm, "radius": 4.15 * mm});
            skSolve(sketch);
        }
        {
            var Q0;
            Q0 = qSketchRegion(id + "F17", true);
            extrude(context, id + "F18", {"entities" : qUnion([Q0]), "operationType" : NewBodyOperationType.REMOVE, "oppositeDirection" : true, "depth" : 25.4 * mm});
        }
        {
            var Q0;
            Q0=makeQuery(id+"F14.opExtrude","CAP_FACE",FACE,{"disambiguationData":[OSD([sQuery(id+"F13.wireOp",EDGE,"E83")])],"isStart":false});
            var sketch = newSketch(context, id + "F19", { "sketchPlane" : qUnion([Q0])});
            skCircle(sketch, "E87", {"center": v(-37.77, 4.15) * mm, "radius": 40.15 * mm});
            skPoint(sketch, "E87.first.point", {"position": v(-58.85, 38.33) * mm});
            skPoint(sketch, "E87.second.point", {"position": v(-15.43, -29.21) * mm});
            skPoint(sketch, "E87.third.point", {"position": v(-9.12, 32.28) * mm});
            skCircle(sketch, "E88", {"center": v(-37.77, 4.15) * mm, "radius": 29.84 * mm});
            skSolve(sketch);
        }
        {
            var Q0;
            Q0=makeQuery(id+"F19.imprint","IMPRINT",FACE,{"disambiguationData":[TD([[makeQuery(id+"F19.imprint","IMPRINT",EDGE,{"derivedFrom":sQuery(id+"F19.wireOp",EDGE,"E88")}),1.0]])]});
            extrude(context, id + "F20", {"entities" : qUnion([Q0]), "operationType" : NewBodyOperationType.REMOVE, "oppositeDirection" : true, "depth" : 25.4 * mm});
        }
        {
            var Q0;
            Q0=makeQuery(id+"F14.opExtrude","CAP_FACE",FACE,{"disambiguationData":[OSD([sQuery(id+"F13.wireOp",EDGE,"E83")])],"isStart":false});
            var sketch = newSketch(context, id + "F21", { "sketchPlane" : qUnion([Q0])});
            skArc(sketch, "E89", {"start": v(-15.22, -29.07) * mm, "mid": v(-2.8, 23.88) * mm, "end": v(-54.55, 40.63) * mm});
            skPoint(sketch, "E89.first.point", {"position": v(-54.55, 40.63) * mm});
            skPoint(sketch, "E89.second.point", {"position": v(-15.22, -29.07) * mm});
            skPoint(sketch, "E89.third.point", {"position": v(-9.74, 32.9) * mm});
            skCircle(sketch, "E90.0", {"center": v(-37.77, 4.15) * mm, "radius": 38.88 * mm});
            skCircle(sketch, "E91.0", {"center": v(-37.77, 4.15) * mm, "radius": 31.1 * mm});
            skSolve(sketch);
        }
        {
            var Q0;
            Q0 = qSketchRegion(id + "F21", true);
            extrude(context, id + "F22", {"entities" : qUnion([Q0]), "operationType" : NewBodyOperationType.REMOVE, "oppositeDirection" : true, "depth" : 0.81 * mm});
        }
        {
            var Q0;
            Q0=makeQuery(id+"F14.opExtrude","CAP_EDGE",EDGE,{"disambiguationData":[OSD([sQuery(id+"F13.wireOp",EDGE,"E83")])],"isStart":false});
            var Q1;
            Q1=makeQuery(id+"F22.boolean.opBoolean","COPY",EDGE,{"derivedFrom":makeQuery(id+"F22.opExtrude","CAP_EDGE",EDGE,{"disambiguationData":[OSD([sQuery(id+"F21.wireOp",EDGE,"E90.0")])],"isStart":true})});
            var Q2;
            Q2=makeQuery(id+"F22.boolean.opBoolean","COPY",EDGE,{"derivedFrom":makeQuery(id+"F22.opExtrude","CAP_EDGE",EDGE,{"disambiguationData":[OSD([sQuery(id+"F21.wireOp",EDGE,"E91.0")])],"isStart":true})});
            var Q3;
            Q3=makeQuery(id+"F20.boolean.opBoolean","COPY",EDGE,{"derivedFrom":makeQuery(id+"F20.opExtrude","CAP_EDGE",EDGE,{"disambiguationData":[OSD([sQuery(id+"F19.wireOp",EDGE,"E88")])],"isStart":true})});
            var Q4;
            Q4=makeQuery(id+"F20.boolean.opBoolean","INTERSECT",EDGE,{"derivedFrom":[makeQuery(id+"F14.opExtrude","CAP_FACE",FACE,{"disambiguationData":[OSD([sQuery(id+"F13.wireOp",EDGE,"E83")])],"isStart":true}),makeQuery(id+"F20.opExtrude","SWEPT_FACE",FACE,{"disambiguationData":[OSD([sQuery(id+"F19.wireOp",EDGE,"E88")])]})]});
            var Q5;
            Q5=makeQuery(id+"F14.opExtrude","CAP_EDGE",EDGE,{"disambiguationData":[OSD([sQuery(id+"F13.wireOp",EDGE,"E83")])],"isStart":true});
            fillet(context, id + "F23", {"entities" : qUnion([Q0, Q1, Q2, Q3, Q4, Q5]), "radius" : 0.5 * mm, "tangentPropagation" : true, "allowEdgeOverflow" : false});
        }
        {
            var Q0;
            Q0=makeQuery(id+"F14.opExtrude","CAP_FACE",FACE,{"disambiguationData":[OSD([sQuery(id+"F13.wireOp",EDGE,"E83")])],"isStart":true});
            extrude(context, id + "F24", {"entities" : qUnion([Q0]), "depth" : 0.5 * mm});
        }
        {
            var Q0;
            Q0=makeQuery(id+"F22.boolean.opBoolean","COPY",FACE,{"derivedFrom":makeQuery(id+"F22.opExtrude","CAP_FACE",FACE,{"disambiguationData":[OSD([sQuery(id+"F21.wireOp",EDGE,"E90.0"),sQuery(id+"F21.wireOp",EDGE,"E91.0")])],"isStart":false})});
            var sketch = newSketch(context, id + "F25", { "sketchPlane" : qUnion([Q0])});
            skLineSegment(sketch, "E92", {"start": v(-56.52, 35.62) * mm, "end": v(-55.5, 33.7) * mm});
            skLineSegment(sketch, "E93", {"start": v(-55.5, 33.7) * mm, "end": v(-55.65, 33.63) * mm});
            skLineSegment(sketch, "E94", {"start": v(-55.65, 33.63) * mm, "end": v(-55.51, 33.37) * mm});
            skLineSegment(sketch, "E95", {"start": v(-55.51, 33.37) * mm, "end": v(-54.77, 33.77) * mm});
            skLineSegment(sketch, "E96", {"start": v(-54.77, 33.77) * mm, "end": v(-54.88, 33.99) * mm});
            skLineSegment(sketch, "E97", {"start": v(-54.88, 33.99) * mm, "end": v(-55.02, 33.91) * mm});
            skLineSegment(sketch, "E98", {"start": v(-55.02, 33.91) * mm, "end": v(-56.05, 35.83) * mm});
            skLineSegment(sketch, "E99", {"start": v(-56.05, 35.83) * mm, "end": v(-55.6, 36.08) * mm});
            skLineSegment(sketch, "E100", {"start": v(-55.6, 36.08) * mm, "end": v(-55.4, 35.93) * mm});
            skLineSegment(sketch, "E101", {"start": v(-55.4, 35.93) * mm, "end": v(-55.2, 36.01) * mm});
            skLineSegment(sketch, "E102", {"start": v(-55.2, 36.01) * mm, "end": v(-55.54, 36.52) * mm});
            skLineSegment(sketch, "E103", {"start": v(-55.54, 36.52) * mm, "end": v(-57.37, 35.6) * mm});
            skLineSegment(sketch, "E104", {"start": v(-57.37, 35.6) * mm, "end": v(-57.1, 35.06) * mm});
            skLineSegment(sketch, "E105", {"start": v(-57.1, 35.06) * mm, "end": v(-56.94, 35.06) * mm});
            skLineSegment(sketch, "E106", {"start": v(-56.94, 35.06) * mm, "end": v(-56.87, 35.48) * mm});
            skLineSegment(sketch, "E107", {"start": v(-56.87, 35.48) * mm, "end": v(-56.52, 35.62) * mm});
            skLineSegment(sketch, "E108", {"start": v(-53.96, 34.5) * mm, "end": v(-54.16, 34.4) * mm});
            skLineSegment(sketch, "E109", {"start": v(-54.16, 34.4) * mm, "end": v(-54.02, 34.13) * mm});
            skLineSegment(sketch, "E110", {"start": v(-54.02, 34.13) * mm, "end": v(-53.24, 34.47) * mm});
            skLineSegment(sketch, "E111", {"start": v(-53.24, 34.47) * mm, "end": v(-53.37, 34.71) * mm});
            skLineSegment(sketch, "E112", {"start": v(-53.37, 34.71) * mm, "end": v(-53.46, 34.67) * mm});
            skLineSegment(sketch, "E113", {"start": v(-53.46, 34.67) * mm, "end": v(-53.87, 35.62) * mm});
            skLineSegment(sketch, "E114", {"start": v(-53.87, 35.62) * mm, "end": v(-53, 36) * mm});
            skLineSegment(sketch, "E115", {"start": v(-53, 36) * mm, "end": v(-52.6, 35.09) * mm});
            skLineSegment(sketch, "E116", {"start": v(-52.6, 35.09) * mm, "end": v(-52.73, 35.02) * mm});
            skLineSegment(sketch, "E117", {"start": v(-52.73, 35.02) * mm, "end": v(-52.56, 34.71) * mm});
            skLineSegment(sketch, "E118", {"start": v(-52.56, 34.71) * mm, "end": v(-51.87, 35.09) * mm});
            skLineSegment(sketch, "E119", {"start": v(-51.87, 35.09) * mm, "end": v(-52, 35.33) * mm});
            skLineSegment(sketch, "E120", {"start": v(-52, 35.33) * mm, "end": v(-52.06, 35.3) * mm});
            skLineSegment(sketch, "E121", {"start": v(-52.06, 35.3) * mm, "end": v(-52.97, 37.32) * mm});
            skLineSegment(sketch, "E122", {"start": v(-52.95, 37.69) * mm, "end": v(-53.67, 37.42) * mm});
            skLineSegment(sketch, "E123", {"start": v(-53.67, 37.42) * mm, "end": v(-53.67, 37.12) * mm});
            skLineSegment(sketch, "E124", {"start": v(-53.67, 37.12) * mm, "end": v(-53.47, 37.12) * mm});
            skLineSegment(sketch, "E125", {"start": v(-53.47, 37.12) * mm, "end": v(-53.1, 36.42) * mm});
            skLineSegment(sketch, "E126", {"start": v(-53.1, 36.42) * mm, "end": v(-54.03, 36) * mm});
            skLineSegment(sketch, "E127", {"start": v(-54.03, 36) * mm, "end": v(-54.39, 36.74) * mm});
            skLineSegment(sketch, "E128", {"start": v(-54.39, 36.74) * mm, "end": v(-54.22, 36.83) * mm});
            skLineSegment(sketch, "E129", {"start": v(-54.22, 36.83) * mm, "end": v(-54.4, 37.06) * mm});
            skLineSegment(sketch, "E130", {"start": v(-54.4, 37.06) * mm, "end": v(-55.08, 36.78) * mm});
            skLineSegment(sketch, "E131", {"start": v(-55.08, 36.78) * mm, "end": v(-55.04, 36.49) * mm});
            skLineSegment(sketch, "E132", {"start": v(-54.88, 36.5) * mm, "end": v(-54.87, 36.5) * mm});
            skLineSegment(sketch, "E133", {"start": v(-55.04, 36.49) * mm, "end": v(-54.9, 36.56) * mm});
            skLineSegment(sketch, "E134", {"start": v(-54.9, 36.56) * mm, "end": v(-53.96, 34.5) * mm});
            skLineSegment(sketch, "E135", {"start": v(-52.95, 37.69) * mm, "end": v(-52.8, 37.5) * mm});
            skLineSegment(sketch, "E136", {"start": v(-52.8, 37.5) * mm, "end": v(-52.97, 37.4) * mm});
            skLineSegment(sketch, "E137", {"start": v(-52.97, 37.4) * mm, "end": v(-52.97, 37.32) * mm});
            skLineSegment(sketch, "E138", {"start": v(-52.15, 37.69) * mm, "end": v(-52.33, 37.69) * mm});
            skLineSegment(sketch, "E139", {"start": v(-52.33, 37.69) * mm, "end": v(-52.33, 37.98) * mm});
            skLineSegment(sketch, "E140", {"start": v(-52.33, 37.98) * mm, "end": v(-50.87, 38.51) * mm});
            skLineSegment(sketch, "E141", {"start": v(-50.87, 38.51) * mm, "end": v(-50.56, 37.96) * mm});
            skLineSegment(sketch, "E142", {"start": v(-50.56, 37.96) * mm, "end": v(-50.74, 37.86) * mm});
            skLineSegment(sketch, "E143", {"start": v(-50.74, 37.86) * mm, "end": v(-50.9, 38) * mm});
            skLineSegment(sketch, "E144", {"start": v(-50.9, 38) * mm, "end": v(-51.61, 37.8) * mm});
            skLineSegment(sketch, "E145", {"start": v(-51.61, 37.8) * mm, "end": v(-51.34, 37.08) * mm});
            skLineSegment(sketch, "E146", {"start": v(-51.34, 37.08) * mm, "end": v(-50.76, 37.24) * mm});
            skLineSegment(sketch, "E147", {"start": v(-50.76, 37.24) * mm, "end": v(-50.76, 37.42) * mm});
            skLineSegment(sketch, "E148", {"start": v(-50.76, 37.42) * mm, "end": v(-50.54, 37.42) * mm});
            skLineSegment(sketch, "E149", {"start": v(-50.54, 37.42) * mm, "end": v(-50.35, 36.94) * mm});
            skLineSegment(sketch, "E150", {"start": v(-50.35, 36.94) * mm, "end": v(-50.53, 36.8) * mm});
            skLineSegment(sketch, "E151", {"start": v(-50.53, 36.8) * mm, "end": v(-50.62, 36.9) * mm});
            skLineSegment(sketch, "E152", {"start": v(-50.62, 36.9) * mm, "end": v(-51.19, 36.71) * mm});
            skLineSegment(sketch, "E153", {"start": v(-51.19, 36.71) * mm, "end": v(-50.9, 35.83) * mm});
            skLineSegment(sketch, "E154", {"start": v(-50.9, 35.83) * mm, "end": v(-50.1, 36.14) * mm});
            skLineSegment(sketch, "E155", {"start": v(-50.1, 36.14) * mm, "end": v(-50.1, 36.42) * mm});
            skLineSegment(sketch, "E156", {"start": v(-50.1, 36.42) * mm, "end": v(-49.88, 36.42) * mm});
            skLineSegment(sketch, "E157", {"start": v(-49.88, 36.42) * mm, "end": v(-49.72, 35.88) * mm});
            skLineSegment(sketch, "E158", {"start": v(-49.72, 35.88) * mm, "end": v(-51.32, 35.2) * mm});
            skLineSegment(sketch, "E159", {"start": v(-51.32, 35.2) * mm, "end": v(-51.52, 35.49) * mm});
            skLineSegment(sketch, "E160", {"start": v(-51.52, 35.49) * mm, "end": v(-51.38, 35.53) * mm});
            skLineSegment(sketch, "E161", {"start": v(-51.38, 35.53) * mm, "end": v(-51.38, 35.78) * mm});
            skLineSegment(sketch, "E162", {"start": v(-51.38, 35.78) * mm, "end": v(-52.15, 37.69) * mm});
            skSolve(sketch);
        }
        {
            var Q0;
            Q0 = qSketchRegion(id + "F25", true);
            extrude(context, id + "F26", {"entities" : qUnion([Q0]), "operationType" : NewBodyOperationType.ADD, "depth" : 0.5 * mm});
        }
        {
            var Q0;
            Q0=makeQuery(id+"F22.boolean.opBoolean","COPY",FACE,{"derivedFrom":makeQuery(id+"F22.opExtrude","CAP_FACE",FACE,{"disambiguationData":[OSD([sQuery(id+"F21.wireOp",EDGE,"E90.0"),sQuery(id+"F21.wireOp",EDGE,"E91.0")])],"isStart":false})});
            var sketch = newSketch(context, id + "F27", { "sketchPlane" : qUnion([Q0])});
            skLineSegment(sketch, "E163", {"start": v(-49.19, 38.72) * mm, "end": v(-48.56, 36.58) * mm});
            skLineSegment(sketch, "E164", {"start": v(-48.56, 36.58) * mm, "end": v(-48.74, 36.47) * mm});
            skLineSegment(sketch, "E165", {"start": v(-48.74, 36.47) * mm, "end": v(-48.62, 36.2) * mm});
            skLineSegment(sketch, "E166", {"start": v(-48.62, 36.2) * mm, "end": v(-47.87, 36.41) * mm});
            skLineSegment(sketch, "E167", {"start": v(-47.87, 36.41) * mm, "end": v(-47.9, 36.72) * mm});
            skLineSegment(sketch, "E168", {"start": v(-47.9, 36.72) * mm, "end": v(-48.09, 36.7) * mm});
            skLineSegment(sketch, "E169", {"start": v(-48.09, 36.7) * mm, "end": v(-48.66, 38.78) * mm});
            skLineSegment(sketch, "E170", {"start": v(-48.77, 39.16) * mm, "end": v(-49.38, 39.03) * mm});
            skLineSegment(sketch, "E171", {"start": v(-49.38, 39.03) * mm, "end": v(-49.38, 38.75) * mm});
            skLineSegment(sketch, "E172", {"start": v(-49.38, 38.75) * mm, "end": v(-49.19, 38.72) * mm});
            skArc(sketch, "E173", {"start": v(-48.4, 37.8) * mm, "mid": v(-47.75, 38.5) * mm, "end": v(-48.66, 38.78) * mm});
            skArc(sketch, "E174", {"start": v(-48.3, 37.44) * mm, "mid": v(-47.28, 38.65) * mm, "end": v(-48.77, 39.16) * mm});
            skArc(sketch, "E175", {"start": v(-45.27, 39.17) * mm, "mid": v(-45.9, 39.5) * mm, "end": v(-46.37, 38.97) * mm});
            skArc(sketch, "E176", {"start": v(-46.14, 37.7) * mm, "mid": v(-45.5, 37.34) * mm, "end": v(-44.99, 37.87) * mm});
            skArc(sketch, "E177", {"start": v(-46.37, 38.97) * mm, "mid": v(-46.3, 38.33) * mm, "end": v(-46.14, 37.7) * mm});
            skArc(sketch, "E178", {"start": v(-44.99, 37.87) * mm, "mid": v(-45.07, 38.53) * mm, "end": v(-45.27, 39.17) * mm});
            skArc(sketch, "E179", {"start": v(-44.84, 39.46) * mm, "mid": v(-45.97, 39.91) * mm, "end": v(-46.89, 39.11) * mm});
            skArc(sketch, "E180", {"start": v(-46.89, 39.11) * mm, "mid": v(-46.86, 38.1) * mm, "end": v(-46.37, 37.2) * mm});
            skArc(sketch, "E181", {"start": v(-44.56, 37.6) * mm, "mid": v(-44.53, 38.56) * mm, "end": v(-44.84, 39.46) * mm});
            skArc(sketch, "E182", {"start": v(-46.37, 37.2) * mm, "mid": v(-45.36, 36.96) * mm, "end": v(-44.56, 37.6) * mm});
            skLineSegment(sketch, "E183", {"start": v(-44.04, 39.85) * mm, "end": v(-43.8, 37.62) * mm});
            skLineSegment(sketch, "E184", {"start": v(-43.8, 37.62) * mm, "end": v(-43.98, 37.6) * mm});
            skLineSegment(sketch, "E185", {"start": v(-43.98, 37.6) * mm, "end": v(-43.86, 37.29) * mm});
            skLineSegment(sketch, "E186", {"start": v(-43.86, 37.29) * mm, "end": v(-42.14, 37.53) * mm});
            skLineSegment(sketch, "E187", {"start": v(-42.14, 37.53) * mm, "end": v(-42.14, 38.17) * mm});
            skLineSegment(sketch, "E188", {"start": v(-42.14, 38.17) * mm, "end": v(-42.4, 38.17) * mm});
            skLineSegment(sketch, "E189", {"start": v(-42.4, 38.17) * mm, "end": v(-42.44, 37.88) * mm});
            skLineSegment(sketch, "E190", {"start": v(-42.44, 37.88) * mm, "end": v(-43.29, 37.76) * mm});
            skLineSegment(sketch, "E191", {"start": v(-43.29, 37.76) * mm, "end": v(-43.54, 39.9) * mm});
            skLineSegment(sketch, "E192", {"start": v(-43.54, 39.9) * mm, "end": v(-43.36, 39.93) * mm});
            skLineSegment(sketch, "E193", {"start": v(-43.36, 39.93) * mm, "end": v(-43.4, 40.24) * mm});
            skLineSegment(sketch, "E194", {"start": v(-43.4, 40.24) * mm, "end": v(-44.25, 40.17) * mm});
            skLineSegment(sketch, "E195", {"start": v(-44.25, 40.17) * mm, "end": v(-44.27, 39.86) * mm});
            skLineSegment(sketch, "E196", {"start": v(-44.27, 39.86) * mm, "end": v(-44.04, 39.85) * mm});
            skLineSegment(sketch, "E197", {"start": v(-41, 40.13) * mm, "end": v(-41.25, 38.88) * mm});
            skLineSegment(sketch, "E198", {"start": v(-41.45, 37.91) * mm, "end": v(-41.4, 37.84) * mm});
            skLineSegment(sketch, "E199", {"start": v(-41.4, 37.84) * mm, "end": v(-41.23, 37.84) * mm});
            skLineSegment(sketch, "E200", {"start": v(-41.23, 37.84) * mm, "end": v(-41.23, 37.55) * mm});
            skLineSegment(sketch, "E201", {"start": v(-41.23, 37.55) * mm, "end": v(-42.02, 37.55) * mm});
            skLineSegment(sketch, "E202", {"start": v(-42.02, 37.55) * mm, "end": v(-42.05, 37.82) * mm});
            skLineSegment(sketch, "E203", {"start": v(-42.05, 37.82) * mm, "end": v(-41.88, 37.84) * mm});
            skLineSegment(sketch, "E204", {"start": v(-41.88, 37.84) * mm, "end": v(-41.35, 40.17) * mm});
            skLineSegment(sketch, "E205", {"start": v(-41, 40.13) * mm, "end": v(-40.51, 38.88) * mm});
            skLineSegment(sketch, "E206", {"start": v(-40.15, 37.93) * mm, "end": v(-40.32, 37.93) * mm});
            skLineSegment(sketch, "E207", {"start": v(-40.32, 37.93) * mm, "end": v(-40.27, 37.62) * mm});
            skLineSegment(sketch, "E208", {"start": v(-40.27, 37.62) * mm, "end": v(-39.46, 37.67) * mm});
            skLineSegment(sketch, "E209", {"start": v(-39.46, 37.67) * mm, "end": v(-39.48, 38) * mm});
            skLineSegment(sketch, "E210", {"start": v(-39.48, 38) * mm, "end": v(-39.61, 38) * mm});
            skLineSegment(sketch, "E211", {"start": v(-39.61, 38) * mm, "end": v(-40.54, 40.18) * mm});
            skLineSegment(sketch, "E212", {"start": v(-41.34, 38.45) * mm, "end": v(-40.36, 38.49) * mm});
            skLineSegment(sketch, "E213", {"start": v(-40.51, 38.88) * mm, "end": v(-41.25, 38.88) * mm});
            skLineSegment(sketch, "E214", {"start": v(-41.35, 40.17) * mm, "end": v(-41.54, 40.2) * mm});
            skLineSegment(sketch, "E215", {"start": v(-41.54, 40.2) * mm, "end": v(-41.5, 40.51) * mm});
            skLineSegment(sketch, "E216", {"start": v(-41.5, 40.51) * mm, "end": v(-40.38, 40.51) * mm});
            skLineSegment(sketch, "E217", {"start": v(-40.38, 40.51) * mm, "end": v(-40.3, 40.27) * mm});
            skLineSegment(sketch, "E218", {"start": v(-40.3, 40.27) * mm, "end": v(-40.54, 40.18) * mm});
            skLineSegment(sketch, "E219.trimOffspring", {"start": v(-40.36, 38.49) * mm, "end": v(-40.15, 37.93) * mm});
            skLineSegment(sketch, "E220.trimOffspring", {"start": v(-41.34, 38.45) * mm, "end": v(-41.45, 37.91) * mm});
            skLineSegment(sketch, "E221", {"start": v(-39.1, 40.27) * mm, "end": v(-39.1, 38) * mm});
            skLineSegment(sketch, "E222", {"start": v(-39.1, 38) * mm, "end": v(-39.3, 38) * mm});
            skLineSegment(sketch, "E223", {"start": v(-39.3, 38) * mm, "end": v(-39.3, 37.69) * mm});
            skLineSegment(sketch, "E224", {"start": v(-39.3, 37.69) * mm, "end": v(-38.53, 37.69) * mm});
            skLineSegment(sketch, "E225", {"start": v(-38.53, 37.69) * mm, "end": v(-38.43, 38) * mm});
            skLineSegment(sketch, "E226", {"start": v(-38.43, 38) * mm, "end": v(-38.62, 38) * mm});
            skLineSegment(sketch, "E227", {"start": v(-38.62, 38) * mm, "end": v(-38.62, 38.87) * mm});
            skLineSegment(sketch, "E228", {"start": v(-38.62, 38.87) * mm, "end": v(-38.24, 38.87) * mm});
            skLineSegment(sketch, "E229", {"start": v(-38.06, 39.3) * mm, "end": v(-38.62, 39.3) * mm});
            skLineSegment(sketch, "E230", {"start": v(-38.62, 39.3) * mm, "end": v(-38.62, 40.24) * mm});
            skLineSegment(sketch, "E231", {"start": v(-38.62, 40.24) * mm, "end": v(-38.12, 40.24) * mm});
            skLineSegment(sketch, "E232", {"start": v(-37.84, 40.57) * mm, "end": v(-39.24, 40.57) * mm});
            skLineSegment(sketch, "E233", {"start": v(-39.24, 40.57) * mm, "end": v(-39.3, 40.31) * mm});
            skLineSegment(sketch, "E234", {"start": v(-39.3, 40.31) * mm, "end": v(-39.1, 40.27) * mm});
            skArc(sketch, "E235", {"start": v(-38.06, 39.3) * mm, "mid": v(-37.73, 39.79) * mm, "end": v(-38.12, 40.24) * mm});
            skArc(sketch, "E236", {"start": v(-37.74, 39.03) * mm, "mid": v(-37.24, 39.83) * mm, "end": v(-37.84, 40.57) * mm});
            skArc(sketch, "E237", {"start": v(-37.34, 38.14) * mm, "mid": v(-37.4, 38.65) * mm, "end": v(-37.74, 39.03) * mm});
            skArc(sketch, "E238", {"start": v(-37.84, 38.1) * mm, "mid": v(-37.92, 38.54) * mm, "end": v(-38.24, 38.87) * mm});
            skArc(sketch, "E239", {"start": v(-37.84, 38.1) * mm, "mid": v(-37.79, 37.85) * mm, "end": v(-37.6, 37.69) * mm});
            skArc(sketch, "E240", {"start": v(-37.34, 38.14) * mm, "mid": v(-37.21, 37.98) * mm, "end": v(-37, 37.97) * mm});
            skArc(sketch, "E241", {"start": v(-37.08, 37.7) * mm, "mid": v(-36.98, 37.81) * mm, "end": v(-37, 37.97) * mm});
            skLineSegment(sketch, "E242", {"start": v(-37.6, 37.69) * mm, "end": v(-37.08, 37.7) * mm});
            skPoint(sketch, "E243.start.orphan", {"position": v(-37.98, 40.4) * mm});
            skPoint(sketch, "E244.trimOffspring.end.orphan", {"position": v(-38.15, 39.08) * mm});
            skSolve(sketch);
        }
        {
            var Q0;
            Q0 = qSketchRegion(id + "F27", true);
            extrude(context, id + "F28", {"entities" : qUnion([Q0]), "operationType" : NewBodyOperationType.ADD, "depth" : 0.76 * mm});
        }
        {
            var Q0;
            {var subQ0=sQuery(id+"F21.wireOp",EDGE,"E91.0");var subQ1=sQuery(id+"F21.wireOp",EDGE,"E90.0");Q0=makeQuery(id+"F28.boolean.opBoolean","SPLIT",FACE,{"disambiguationData":[TD([makeQuery(id+"F22.boolean.opBoolean","COPY",FACE,{"derivedFrom":makeQuery(id+"F22.opExtrude","SWEPT_FACE",FACE,{"disambiguationData":[OSD([subQ1])]})})])],"derivedFrom":makeQuery(id+"F22.boolean.opBoolean","COPY",FACE,{"derivedFrom":makeQuery(id+"F22.opExtrude","CAP_FACE",FACE,{"disambiguationData":[OSD([subQ1,subQ0])],"isStart":false})})});}
            var sketch = newSketch(context, id + "F29", { "sketchPlane" : qUnion([Q0])});
            skLineSegment(sketch, "E245", {"start": v(-35.83, 37.96) * mm, "end": v(-35.72, 40.18) * mm});
            skLineSegment(sketch, "E246", {"start": v(-35.72, 40.18) * mm, "end": v(-35.89, 40.19) * mm});
            skLineSegment(sketch, "E247", {"start": v(-35.89, 40.19) * mm, "end": v(-35.78, 40.5) * mm});
            skLineSegment(sketch, "E248", {"start": v(-35.78, 40.5) * mm, "end": v(-34.16, 40.34) * mm});
            skLineSegment(sketch, "E249", {"start": v(-34.16, 40.34) * mm, "end": v(-34.16, 39.8) * mm});
            skLineSegment(sketch, "E250", {"start": v(-34.16, 39.8) * mm, "end": v(-34.44, 39.7) * mm});
            skLineSegment(sketch, "E251", {"start": v(-34.44, 39.7) * mm, "end": v(-34.44, 39.95) * mm});
            skLineSegment(sketch, "E252", {"start": v(-34.44, 39.95) * mm, "end": v(-34.64, 40.08) * mm});
            skLineSegment(sketch, "E253", {"start": v(-34.64, 40.08) * mm, "end": v(-35.22, 40.08) * mm});
            skLineSegment(sketch, "E254", {"start": v(-35.22, 39.23) * mm, "end": v(-34.64, 39.15) * mm});
            skLineSegment(sketch, "E255", {"start": v(-34.64, 39.15) * mm, "end": v(-34.61, 39.38) * mm});
            skLineSegment(sketch, "E256", {"start": v(-34.61, 39.38) * mm, "end": v(-34.4, 39.26) * mm});
            skLineSegment(sketch, "E257", {"start": v(-34.4, 39.26) * mm, "end": v(-34.4, 38.7) * mm});
            skLineSegment(sketch, "E258", {"start": v(-34.4, 38.7) * mm, "end": v(-34.66, 38.64) * mm});
            skLineSegment(sketch, "E259", {"start": v(-34.66, 38.64) * mm, "end": v(-34.7, 38.8) * mm});
            skLineSegment(sketch, "E260", {"start": v(-35.42, 37.95) * mm, "end": v(-34.6, 37.84) * mm});
            skLineSegment(sketch, "E261", {"start": v(-34.6, 37.84) * mm, "end": v(-34.42, 38.09) * mm});
            skLineSegment(sketch, "E262", {"start": v(-34.42, 38.09) * mm, "end": v(-34.22, 38.09) * mm});
            skLineSegment(sketch, "E263", {"start": v(-34.22, 38.09) * mm, "end": v(-34.29, 37.47) * mm});
            skLineSegment(sketch, "E264", {"start": v(-34.29, 37.47) * mm, "end": v(-36.06, 37.65) * mm});
            skLineSegment(sketch, "E265", {"start": v(-36.06, 37.65) * mm, "end": v(-36.06, 37.9) * mm});
            skLineSegment(sketch, "E266", {"start": v(-36.06, 37.9) * mm, "end": v(-35.83, 37.96) * mm});
            skLineSegment(sketch, "E267", {"start": v(-35.22, 40.08) * mm, "end": v(-35.3, 39.24) * mm});
            skLineSegment(sketch, "E268", {"start": v(-35.33, 38.92) * mm, "end": v(-34.7, 38.8) * mm});
            skLineSegment(sketch, "E269", {"start": v(-34.64, 39.15) * mm, "end": v(-35.3, 39.24) * mm});
            skLineSegment(sketch, "E270.trimOffspring", {"start": v(-35.33, 38.92) * mm, "end": v(-35.42, 37.95) * mm});
            skLineSegment(sketch, "E271", {"start": v(-33.58, 40.01) * mm, "end": v(-33, 38.76) * mm});
            skLineSegment(sketch, "E272", {"start": v(-31.8, 37.4) * mm, "end": v(-32.4, 38.7) * mm});
            skLineSegment(sketch, "E273", {"start": v(-32.94, 39.85) * mm, "end": v(-32.77, 39.85) * mm});
            skLineSegment(sketch, "E274", {"start": v(-32.77, 39.85) * mm, "end": v(-32.77, 40.13) * mm});
            skLineSegment(sketch, "E275", {"start": v(-32.77, 40.13) * mm, "end": v(-33.58, 40.3) * mm});
            skLineSegment(sketch, "E276", {"start": v(-33.58, 40.3) * mm, "end": v(-33.75, 40.06) * mm});
            skLineSegment(sketch, "E277", {"start": v(-33.75, 40.06) * mm, "end": v(-33.58, 40.01) * mm});
            skLineSegment(sketch, "E278", {"start": v(-33.42, 37.68) * mm, "end": v(-32.79, 38.32) * mm});
            skLineSegment(sketch, "E279", {"start": v(-31.52, 39.61) * mm, "end": v(-31.37, 39.61) * mm});
            skLineSegment(sketch, "E280", {"start": v(-31.37, 39.61) * mm, "end": v(-31.37, 39.9) * mm});
            skLineSegment(sketch, "E281", {"start": v(-31.37, 39.9) * mm, "end": v(-32.05, 40.01) * mm});
            skLineSegment(sketch, "E282", {"start": v(-32.05, 40.01) * mm, "end": v(-32.2, 39.83) * mm});
            skLineSegment(sketch, "E283", {"start": v(-32.2, 39.83) * mm, "end": v(-32.05, 39.78) * mm});
            skLineSegment(sketch, "E284", {"start": v(-32.05, 39.78) * mm, "end": v(-32.62, 39.16) * mm});
            skLineSegment(sketch, "E285", {"start": v(-33.91, 37.76) * mm, "end": v(-34.11, 37.76) * mm});
            skLineSegment(sketch, "E286", {"start": v(-34.11, 37.76) * mm, "end": v(-34.07, 37.46) * mm});
            skLineSegment(sketch, "E287", {"start": v(-34.07, 37.46) * mm, "end": v(-33.36, 37.36) * mm});
            skLineSegment(sketch, "E288", {"start": v(-33.36, 37.36) * mm, "end": v(-33.24, 37.57) * mm});
            skLineSegment(sketch, "E289", {"start": v(-33.24, 37.57) * mm, "end": v(-33.42, 37.68) * mm});
            skLineSegment(sketch, "E290", {"start": v(-32.43, 37.55) * mm, "end": v(-32.58, 37.55) * mm});
            skLineSegment(sketch, "E291", {"start": v(-32.58, 37.55) * mm, "end": v(-32.58, 37.23) * mm});
            skLineSegment(sketch, "E292", {"start": v(-32.58, 37.23) * mm, "end": v(-31.76, 37.05) * mm});
            skLineSegment(sketch, "E293", {"start": v(-31.76, 37.05) * mm, "end": v(-31.62, 37.33) * mm});
            skLineSegment(sketch, "E294", {"start": v(-31.62, 37.33) * mm, "end": v(-31.8, 37.4) * mm});
            skLineSegment(sketch, "E295.trimOffspring", {"start": v(-33, 38.76) * mm, "end": v(-33.91, 37.76) * mm});
            skLineSegment(sketch, "E296.trimOffspring", {"start": v(-32.62, 39.16) * mm, "end": v(-32.94, 39.85) * mm});
            skLineSegment(sketch, "E297.trimOffspring", {"start": v(-32.4, 38.7) * mm, "end": v(-31.52, 39.61) * mm});
            skLineSegment(sketch, "E298.trimOffspring", {"start": v(-32.79, 38.32) * mm, "end": v(-32.43, 37.55) * mm});
            skLineSegment(sketch, "E299", {"start": v(-31.33, 37.28) * mm, "end": v(-31.23, 37.35) * mm});
            skLineSegment(sketch, "E300", {"start": v(-31.23, 37.35) * mm, "end": v(-30.77, 39.45) * mm});
            skLineSegment(sketch, "E301", {"start": v(-30.31, 39.35) * mm, "end": v(-30.53, 38.35) * mm});
            skLineSegment(sketch, "E302", {"start": v(-30.77, 37.24) * mm, "end": v(-30.74, 37.14) * mm});
            skLineSegment(sketch, "E303", {"start": v(-30.74, 37.14) * mm, "end": v(-30.6, 37.1) * mm});
            skLineSegment(sketch, "E304", {"start": v(-30.6, 37.1) * mm, "end": v(-30.72, 36.83) * mm});
            skLineSegment(sketch, "E305", {"start": v(-30.72, 36.83) * mm, "end": v(-31.45, 37) * mm});
            skLineSegment(sketch, "E306", {"start": v(-31.45, 37) * mm, "end": v(-31.45, 37.29) * mm});
            skLineSegment(sketch, "E307", {"start": v(-31.45, 37.29) * mm, "end": v(-31.33, 37.28) * mm});
            skLineSegment(sketch, "E308", {"start": v(-30.77, 39.45) * mm, "end": v(-30.85, 39.54) * mm});
            skLineSegment(sketch, "E309", {"start": v(-30.85, 39.54) * mm, "end": v(-30.77, 39.8) * mm});
            skLineSegment(sketch, "E310", {"start": v(-30.77, 39.8) * mm, "end": v(-29.74, 39.6) * mm});
            skLineSegment(sketch, "E311", {"start": v(-30.53, 38.35) * mm, "end": v(-30.02, 38.23) * mm});
            skLineSegment(sketch, "E312", {"start": v(-30.1, 37.86) * mm, "end": v(-30.61, 37.97) * mm});
            skArc(sketch, "E313", {"start": v(-30.02, 38.23) * mm, "mid": v(-29.66, 38.92) * mm, "end": v(-30.31, 39.35) * mm});
            skArc(sketch, "E314", {"start": v(-30.1, 37.86) * mm, "mid": v(-29.15, 38.56) * mm, "end": v(-29.74, 39.6) * mm});
            skLineSegment(sketch, "E315.trimOffspring", {"start": v(-30.61, 37.97) * mm, "end": v(-30.77, 37.24) * mm});
            skSolve(sketch);
        }
        {
            var Q0;
            Q0 = qSketchRegion(id + "F29", true);
            extrude(context, id + "F30", {"entities" : qUnion([Q0]), "operationType" : NewBodyOperationType.ADD, "depth" : 0.76 * mm});
        }
        {
            var Q0;
            {var subQ95=sQuery(id+"F21.wireOp",EDGE,"E90.0");var subQ96=makeQuery(id+"F22.boolean.opBoolean","COPY",FACE,{"derivedFrom":makeQuery(id+"F22.opExtrude","SWEPT_FACE",FACE,{"disambiguationData":[OSD([subQ95])]})});var subQ97=sQuery(id+"F21.wireOp",EDGE,"E91.0");Q0=makeQuery(id+"F30.boolean.opBoolean","SPLIT",FACE,{"disambiguationData":[TD([subQ96])],"derivedFrom":makeQuery(id+"F28.boolean.opBoolean","SPLIT",FACE,{"disambiguationData":[TD([subQ96])],"derivedFrom":makeQuery(id+"F22.boolean.opBoolean","COPY",FACE,{"derivedFrom":makeQuery(id+"F22.opExtrude","CAP_FACE",FACE,{"disambiguationData":[OSD([subQ95,subQ97])],"isStart":false})})})});}
            var sketch = newSketch(context, id + "F31", { "sketchPlane" : qUnion([Q0])});
            skLineSegment(sketch, "E316", {"start": v(-29.13, 36.82) * mm, "end": v(-28.47, 38.9) * mm});
            skLineSegment(sketch, "E317", {"start": v(-28.47, 38.9) * mm, "end": v(-28.64, 38.95) * mm});
            skLineSegment(sketch, "E318", {"start": v(-28.64, 38.95) * mm, "end": v(-28.54, 39.28) * mm});
            skLineSegment(sketch, "E319", {"start": v(-28.54, 39.28) * mm, "end": v(-27.44, 38.93) * mm});
            skLineSegment(sketch, "E320", {"start": v(-27.58, 38.64) * mm, "end": v(-28.01, 38.74) * mm});
            skLineSegment(sketch, "E321", {"start": v(-28.01, 38.74) * mm, "end": v(-28.27, 37.88) * mm});
            skLineSegment(sketch, "E322", {"start": v(-28.62, 36.7) * mm, "end": v(-28.49, 36.56) * mm});
            skLineSegment(sketch, "E323", {"start": v(-28.49, 36.56) * mm, "end": v(-28.63, 36.33) * mm});
            skLineSegment(sketch, "E324", {"start": v(-28.63, 36.33) * mm, "end": v(-29.31, 36.49) * mm});
            skLineSegment(sketch, "E325", {"start": v(-29.31, 36.49) * mm, "end": v(-29.31, 36.79) * mm});
            skLineSegment(sketch, "E326", {"start": v(-29.31, 36.79) * mm, "end": v(-29.13, 36.82) * mm});
            skLineSegment(sketch, "E327", {"start": v(-28.27, 37.88) * mm, "end": v(-27.8, 37.7) * mm});
            skLineSegment(sketch, "E328", {"start": v(-27.93, 37.37) * mm, "end": v(-28.38, 37.5) * mm});
            skArc(sketch, "E329", {"start": v(-27.8, 37.7) * mm, "mid": v(-27.3, 38.08) * mm, "end": v(-27.58, 38.64) * mm});
            skArc(sketch, "E330", {"start": v(-27.5, 37.37) * mm, "mid": v(-26.87, 38.13) * mm, "end": v(-27.44, 38.93) * mm});
            skLineSegment(sketch, "E331", {"start": v(-27.93, 37.37) * mm, "end": v(-27.86, 37.23) * mm});
            skLineSegment(sketch, "E332", {"start": v(-27.77, 36.85) * mm, "end": v(-27.77, 36.17) * mm});
            skLineSegment(sketch, "E333", {"start": v(-27.77, 36.17) * mm, "end": v(-27.69, 36.06) * mm});
            skLineSegment(sketch, "E334", {"start": v(-27.69, 36.06) * mm, "end": v(-27.24, 35.92) * mm});
            skLineSegment(sketch, "E335", {"start": v(-27.24, 35.92) * mm, "end": v(-27.06, 36.13) * mm});
            skLineSegment(sketch, "E336", {"start": v(-27.06, 36.13) * mm, "end": v(-27.32, 36.25) * mm});
            skLineSegment(sketch, "E337", {"start": v(-27.32, 36.25) * mm, "end": v(-27.32, 36.98) * mm});
            skArc(sketch, "E338", {"start": v(-27.32, 36.98) * mm, "mid": v(-27.37, 37.2) * mm, "end": v(-27.5, 37.37) * mm});
            skArc(sketch, "E339", {"start": v(-27.77, 36.85) * mm, "mid": v(-27.77, 37.05) * mm, "end": v(-27.86, 37.23) * mm});
            skLineSegment(sketch, "E340.trimOffspring", {"start": v(-28.38, 37.5) * mm, "end": v(-28.62, 36.7) * mm});
            skLineSegment(sketch, "E341", {"start": v(-26.9, 36.1) * mm, "end": v(-26.7, 36.1) * mm});
            skLineSegment(sketch, "E342", {"start": v(-26.7, 36.1) * mm, "end": v(-25.94, 38.1) * mm});
            skLineSegment(sketch, "E343", {"start": v(-25.94, 38.1) * mm, "end": v(-26.1, 38.27) * mm});
            skLineSegment(sketch, "E344", {"start": v(-26.1, 38.27) * mm, "end": v(-25.9, 38.48) * mm});
            skLineSegment(sketch, "E345", {"start": v(-25.9, 38.48) * mm, "end": v(-24.4, 37.92) * mm});
            skLineSegment(sketch, "E346", {"start": v(-24.4, 37.92) * mm, "end": v(-24.62, 37.37) * mm});
            skLineSegment(sketch, "E347", {"start": v(-24.62, 37.37) * mm, "end": v(-24.85, 37.36) * mm});
            skLineSegment(sketch, "E348", {"start": v(-24.85, 37.36) * mm, "end": v(-24.84, 37.64) * mm});
            skLineSegment(sketch, "E349", {"start": v(-24.84, 37.64) * mm, "end": v(-25.43, 37.92) * mm});
            skLineSegment(sketch, "E350", {"start": v(-25.75, 37.15) * mm, "end": v(-25.25, 36.91) * mm});
            skLineSegment(sketch, "E351", {"start": v(-25.25, 36.91) * mm, "end": v(-25.1, 37.1) * mm});
            skLineSegment(sketch, "E352", {"start": v(-25.1, 37.1) * mm, "end": v(-24.92, 36.94) * mm});
            skLineSegment(sketch, "E353", {"start": v(-24.92, 36.94) * mm, "end": v(-25.11, 36.4) * mm});
            skLineSegment(sketch, "E354", {"start": v(-25.11, 36.4) * mm, "end": v(-25.3, 36.4) * mm});
            skLineSegment(sketch, "E355", {"start": v(-25.3, 36.4) * mm, "end": v(-25.3, 36.55) * mm});
            skLineSegment(sketch, "E356", {"start": v(-25.3, 36.55) * mm, "end": v(-25.89, 36.82) * mm});
            skLineSegment(sketch, "E357", {"start": v(-25.89, 36.82) * mm, "end": v(-26.22, 35.97) * mm});
            skLineSegment(sketch, "E358", {"start": v(-26.22, 35.97) * mm, "end": v(-25.88, 36.82) * mm});
            skLineSegment(sketch, "E359", {"start": v(-26.22, 35.97) * mm, "end": v(-25.54, 35.64) * mm});
            skLineSegment(sketch, "E360", {"start": v(-25.54, 35.64) * mm, "end": v(-25.43, 35.64) * mm});
            skLineSegment(sketch, "E361", {"start": v(-25.43, 35.64) * mm, "end": v(-25.3, 35.87) * mm});
            skLineSegment(sketch, "E362", {"start": v(-25.3, 35.87) * mm, "end": v(-25.05, 35.73) * mm});
            skLineSegment(sketch, "E363", {"start": v(-25.05, 35.73) * mm, "end": v(-25.3, 35.2) * mm});
            skLineSegment(sketch, "E364", {"start": v(-25.3, 35.2) * mm, "end": v(-26.92, 35.77) * mm});
            skLineSegment(sketch, "E365", {"start": v(-26.92, 35.77) * mm, "end": v(-26.9, 36.1) * mm});
            skLineSegment(sketch, "E366.trimOffspring", {"start": v(-25.75, 37.15) * mm, "end": v(-25.43, 37.92) * mm});
            skArc(sketch, "E367", {"start": v(-24.45, 35.34) * mm, "mid": v(-23.67, 35.02) * mm, "end": v(-23.77, 35.85) * mm});
            skArc(sketch, "E368", {"start": v(-23.77, 37.4) * mm, "mid": v(-24.24, 36.62) * mm, "end": v(-23.77, 35.85) * mm});
            skArc(sketch, "E369", {"start": v(-22.8, 37.3) * mm, "mid": v(-23.28, 37.45) * mm, "end": v(-23.77, 37.4) * mm});
            skArc(sketch, "E370", {"start": v(-22.89, 36.86) * mm, "mid": v(-23.56, 37.03) * mm, "end": v(-23.48, 36.34) * mm});
            skArc(sketch, "E371", {"start": v(-24.37, 34.77) * mm, "mid": v(-23.02, 35.05) * mm, "end": v(-23.48, 36.34) * mm});
            skLineSegment(sketch, "E372", {"start": v(-24.45, 35.34) * mm, "end": v(-24.45, 35.67) * mm});
            skLineSegment(sketch, "E373", {"start": v(-24.45, 35.67) * mm, "end": v(-24.6, 35.75) * mm});
            skLineSegment(sketch, "E374", {"start": v(-24.6, 35.75) * mm, "end": v(-24.93, 35.34) * mm});
            skLineSegment(sketch, "E375", {"start": v(-24.93, 35.34) * mm, "end": v(-24.88, 35.2) * mm});
            skLineSegment(sketch, "E376", {"start": v(-24.88, 35.2) * mm, "end": v(-24.37, 34.77) * mm});
            skLineSegment(sketch, "E377", {"start": v(-22.89, 36.86) * mm, "end": v(-22.89, 36.47) * mm});
            skLineSegment(sketch, "E378", {"start": v(-22.89, 36.47) * mm, "end": v(-22.69, 36.47) * mm});
            skLineSegment(sketch, "E379", {"start": v(-22.69, 36.47) * mm, "end": v(-22.32, 36.86) * mm});
            skLineSegment(sketch, "E380", {"start": v(-22.32, 36.86) * mm, "end": v(-22.8, 37.3) * mm});
            skLineSegment(sketch, "E381", {"start": v(-20.84, 35.8) * mm, "end": v(-20.84, 35.43) * mm});
            skLineSegment(sketch, "E382", {"start": v(-20.84, 35.43) * mm, "end": v(-20.7, 35.38) * mm});
            skLineSegment(sketch, "E383", {"start": v(-20.7, 35.38) * mm, "end": v(-20.28, 35.82) * mm});
            skLineSegment(sketch, "E384", {"start": v(-20.28, 35.82) * mm, "end": v(-20.46, 36.06) * mm});
            skArc(sketch, "E385", {"start": v(-20.46, 36.06) * mm, "mid": v(-21.63, 36.46) * mm, "end": v(-22.15, 35.34) * mm});
            skArc(sketch, "E386", {"start": v(-20.84, 35.8) * mm, "mid": v(-21.4, 36.14) * mm, "end": v(-21.64, 35.52) * mm});
            skArc(sketch, "E387", {"start": v(-22.49, 34.43) * mm, "mid": v(-21.72, 34.09) * mm, "end": v(-21.77, 34.93) * mm});
            skArc(sketch, "E388", {"start": v(-22.02, 33.67) * mm, "mid": v(-21.13, 34) * mm, "end": v(-21.12, 34.94) * mm});
            skArc(sketch, "E389", {"start": v(-21.64, 35.52) * mm, "mid": v(-21.4, 35.21) * mm, "end": v(-21.12, 34.94) * mm});
            skArc(sketch, "E390", {"start": v(-22.15, 35.34) * mm, "mid": v(-21.99, 35.1) * mm, "end": v(-21.77, 34.93) * mm});
            skArc(sketch, "E391", {"start": v(-23, 34.41) * mm, "mid": v(-22.6, 33.93) * mm, "end": v(-22.02, 33.67) * mm});
            skLineSegment(sketch, "E392", {"start": v(-23, 34.41) * mm, "end": v(-22.61, 34.85) * mm});
            skLineSegment(sketch, "E393", {"start": v(-22.61, 34.85) * mm, "end": v(-22.48, 34.8) * mm});
            skLineSegment(sketch, "E394", {"start": v(-22.48, 34.8) * mm, "end": v(-22.49, 34.43) * mm});
            skLineSegment(sketch, "E395", {"start": v(-20.04, 34.58) * mm, "end": v(-20, 34.63) * mm});
            skLineSegment(sketch, "E396", {"start": v(-20, 34.63) * mm, "end": v(-19.63, 35.13) * mm});
            skLineSegment(sketch, "E397", {"start": v(-19.63, 35.13) * mm, "end": v(-19.75, 35.22) * mm});
            skLineSegment(sketch, "E398", {"start": v(-19.75, 35.22) * mm, "end": v(-19.86, 35.22) * mm});
            skLineSegment(sketch, "E399", {"start": v(-19.86, 35.22) * mm, "end": v(-20, 35.22) * mm});
            skLineSegment(sketch, "E400", {"start": v(-20, 35.22) * mm, "end": v(-19.78, 35.48) * mm});
            skLineSegment(sketch, "E401", {"start": v(-19.78, 35.48) * mm, "end": v(-19.12, 34.93) * mm});
            skLineSegment(sketch, "E402", {"start": v(-19.12, 34.93) * mm, "end": v(-19.27, 34.75) * mm});
            skLineSegment(sketch, "E403", {"start": v(-19.27, 34.75) * mm, "end": v(-19.3, 34.77) * mm});
            skLineSegment(sketch, "E404", {"start": v(-19.3, 34.77) * mm, "end": v(-19.42, 34.99) * mm});
            skLineSegment(sketch, "E405", {"start": v(-19.42, 34.99) * mm, "end": v(-19.81, 34.43) * mm});
            skLineSegment(sketch, "E406", {"start": v(-19.81, 34.43) * mm, "end": v(-19.78, 34.36) * mm});
            skLineSegment(sketch, "E407", {"start": v(-19.78, 34.36) * mm, "end": v(-19.89, 34.23) * mm});
            skLineSegment(sketch, "E408", {"start": v(-19.89, 34.23) * mm, "end": v(-20.2, 34.43) * mm});
            skLineSegment(sketch, "E409", {"start": v(-20.2, 34.43) * mm, "end": v(-20.12, 34.57) * mm});
            skLineSegment(sketch, "E410", {"start": v(-20.12, 34.57) * mm, "end": v(-20.04, 34.58) * mm});
            skLineSegment(sketch, "E411", {"start": v(-19.26, 34.08) * mm, "end": v(-19, 34.4) * mm});
            skLineSegment(sketch, "E412", {"start": v(-19, 34.4) * mm, "end": v(-19, 33.95) * mm});
            skLineSegment(sketch, "E413", {"start": v(-19, 33.95) * mm, "end": v(-18.95, 33.92) * mm});
            skLineSegment(sketch, "E414", {"start": v(-18.95, 33.92) * mm, "end": v(-18.55, 34.08) * mm});
            skLineSegment(sketch, "E415", {"start": v(-18.55, 34.08) * mm, "end": v(-18.8, 33.72) * mm});
            skLineSegment(sketch, "E416", {"start": v(-18.8, 33.72) * mm, "end": v(-18.89, 33.76) * mm});
            skLineSegment(sketch, "E417", {"start": v(-18.89, 33.76) * mm, "end": v(-18.96, 33.6) * mm});
            skLineSegment(sketch, "E418", {"start": v(-18.96, 33.6) * mm, "end": v(-18.7, 33.38) * mm});
            skLineSegment(sketch, "E419", {"start": v(-18.7, 33.38) * mm, "end": v(-18.57, 33.44) * mm});
            skLineSegment(sketch, "E420", {"start": v(-18.57, 33.44) * mm, "end": v(-18.64, 33.58) * mm});
            skLineSegment(sketch, "E421", {"start": v(-18.64, 33.58) * mm, "end": v(-18.22, 34.11) * mm});
            skLineSegment(sketch, "E422", {"start": v(-18.22, 34.11) * mm, "end": v(-18.14, 34.08) * mm});
            skLineSegment(sketch, "E423", {"start": v(-18.14, 34.08) * mm, "end": v(-18.14, 34.16) * mm});
            skLineSegment(sketch, "E424", {"start": v(-18.14, 34.16) * mm, "end": v(-18.32, 34.4) * mm});
            skLineSegment(sketch, "E425", {"start": v(-18.32, 34.4) * mm, "end": v(-18.75, 34.2) * mm});
            skLineSegment(sketch, "E426", {"start": v(-18.75, 34.2) * mm, "end": v(-18.76, 34.68) * mm});
            skLineSegment(sketch, "E427", {"start": v(-18.76, 34.68) * mm, "end": v(-18.95, 34.86) * mm});
            skLineSegment(sketch, "E428", {"start": v(-18.95, 34.86) * mm, "end": v(-19.06, 34.77) * mm});
            skLineSegment(sketch, "E429", {"start": v(-19.06, 34.77) * mm, "end": v(-19.02, 34.66) * mm});
            skLineSegment(sketch, "E430", {"start": v(-19.02, 34.66) * mm, "end": v(-19.4, 34.15) * mm});
            skLineSegment(sketch, "E431", {"start": v(-19.4, 34.15) * mm, "end": v(-19.53, 34.17) * mm});
            skLineSegment(sketch, "E432", {"start": v(-19.53, 34.17) * mm, "end": v(-19.53, 34.02) * mm});
            skLineSegment(sketch, "E433", {"start": v(-19.53, 34.02) * mm, "end": v(-19.36, 33.86) * mm});
            skLineSegment(sketch, "E434", {"start": v(-19.36, 33.86) * mm, "end": v(-19.21, 33.9) * mm});
            skLineSegment(sketch, "E435", {"start": v(-19.21, 33.9) * mm, "end": v(-19.26, 34.08) * mm});
            skSolve(sketch);
        }
        {
            var Q0;
            Q0 = qSketchRegion(id + "F31", true);
            extrude(context, id + "F32", {"entities" : qUnion([Q0]), "operationType" : NewBodyOperationType.ADD, "depth" : 0.76 * mm});
        }
        {
            var Q0;
            {var subQ153=sQuery(id+"F21.wireOp",EDGE,"E90.0");var subQ154=makeQuery(id+"F22.boolean.opBoolean","COPY",FACE,{"derivedFrom":makeQuery(id+"F22.opExtrude","SWEPT_FACE",FACE,{"disambiguationData":[OSD([subQ153])]})});var subQ155=sQuery(id+"F21.wireOp",EDGE,"E91.0");Q0=makeQuery(id+"F32.boolean.opBoolean","SPLIT",FACE,{"disambiguationData":[TD([subQ154])],"derivedFrom":makeQuery(id+"F30.boolean.opBoolean","SPLIT",FACE,{"disambiguationData":[TD([subQ154])],"derivedFrom":makeQuery(id+"F28.boolean.opBoolean","SPLIT",FACE,{"disambiguationData":[TD([subQ154])],"derivedFrom":makeQuery(id+"F22.boolean.opBoolean","COPY",FACE,{"derivedFrom":makeQuery(id+"F22.opExtrude","CAP_FACE",FACE,{"disambiguationData":[OSD([subQ153,subQ155])],"isStart":false})})})})});}
            var sketch = newSketch(context, id + "F33", { "sketchPlane" : qUnion([Q0])});
            skLineSegment(sketch, "E436", {"start": v(-46.8, -30.92) * mm, "end": v(-46.25, -28.38) * mm});
            skLineSegment(sketch, "E437", {"start": v(-46.25, -28.38) * mm, "end": v(-46.46, -28.23) * mm});
            skLineSegment(sketch, "E438", {"start": v(-46.46, -28.23) * mm, "end": v(-46.36, -27.9) * mm});
            skLineSegment(sketch, "E439", {"start": v(-46.36, -27.9) * mm, "end": v(-44.77, -28.25) * mm});
            skLineSegment(sketch, "E440", {"start": v(-45.15, -28.6) * mm, "end": v(-45.65, -28.49) * mm});
            skLineSegment(sketch, "E441", {"start": v(-45.65, -28.49) * mm, "end": v(-45.86, -29.44) * mm});
            skLineSegment(sketch, "E442", {"start": v(-45.86, -29.44) * mm, "end": v(-45.38, -29.54) * mm});
            skLineSegment(sketch, "E443", {"start": v(-45.38, -30.04) * mm, "end": v(-45.96, -29.93) * mm});
            skLineSegment(sketch, "E444", {"start": v(-45.96, -29.93) * mm, "end": v(-46.17, -31.06) * mm});
            skLineSegment(sketch, "E445", {"start": v(-46.17, -31.06) * mm, "end": v(-45.7, -31.15) * mm});
            skLineSegment(sketch, "E446", {"start": v(-45.79, -31.6) * mm, "end": v(-47.12, -31.34) * mm});
            skLineSegment(sketch, "E447", {"start": v(-47.12, -31.34) * mm, "end": v(-47.12, -31.01) * mm});
            skLineSegment(sketch, "E448", {"start": v(-47.12, -31.01) * mm, "end": v(-46.8, -30.92) * mm});
            skArc(sketch, "E449", {"start": v(-45.38, -29.54) * mm, "mid": v(-44.93, -29.15) * mm, "end": v(-45.15, -28.6) * mm});
            skArc(sketch, "E450", {"start": v(-44.85, -29.9) * mm, "mid": v(-44.3, -29.1) * mm, "end": v(-44.77, -28.25) * mm});
            skArc(sketch, "E451", {"start": v(-45.7, -31.15) * mm, "mid": v(-45.14, -30.7) * mm, "end": v(-45.38, -30.04) * mm});
            skArc(sketch, "E452", {"start": v(-45.79, -31.6) * mm, "mid": v(-44.57, -31.16) * mm, "end": v(-44.85, -29.9) * mm});
            skLineSegment(sketch, "E453", {"start": v(-42.84, -28.96) * mm, "end": v(-42.98, -30.02) * mm});
            skLineSegment(sketch, "E454", {"start": v(-43.24, -32.07) * mm, "end": v(-44.01, -31.97) * mm});
            skLineSegment(sketch, "E455", {"start": v(-44.01, -31.97) * mm, "end": v(-44.01, -31.63) * mm});
            skLineSegment(sketch, "E456", {"start": v(-44.01, -31.63) * mm, "end": v(-43.84, -31.63) * mm});
            skLineSegment(sketch, "E457", {"start": v(-43.84, -31.63) * mm, "end": v(-43.5, -28.87) * mm});
            skLineSegment(sketch, "E458", {"start": v(-43.5, -28.87) * mm, "end": v(-43.7, -28.85) * mm});
            skLineSegment(sketch, "E459", {"start": v(-43.7, -28.85) * mm, "end": v(-43.56, -28.48) * mm});
            skLineSegment(sketch, "E460", {"start": v(-43.56, -28.48) * mm, "end": v(-41.61, -28.74) * mm});
            skLineSegment(sketch, "E461", {"start": v(-41.61, -28.74) * mm, "end": v(-41.61, -29.42) * mm});
            skLineSegment(sketch, "E462", {"start": v(-41.61, -29.42) * mm, "end": v(-41.97, -29.47) * mm});
            skLineSegment(sketch, "E463", {"start": v(-41.97, -29.47) * mm, "end": v(-42, -29.16) * mm});
            skLineSegment(sketch, "E464", {"start": v(-42, -29.16) * mm, "end": v(-42.84, -28.96) * mm});
            skLineSegment(sketch, "E465", {"start": v(-42.98, -30.02) * mm, "end": v(-42.2, -30.11) * mm});
            skLineSegment(sketch, "E466", {"start": v(-42.2, -30.11) * mm, "end": v(-42.18, -29.92) * mm});
            skLineSegment(sketch, "E467", {"start": v(-42.18, -29.92) * mm, "end": v(-41.89, -29.95) * mm});
            skLineSegment(sketch, "E468", {"start": v(-41.98, -30.8) * mm, "end": v(-42.29, -30.76) * mm});
            skLineSegment(sketch, "E469", {"start": v(-42.29, -30.76) * mm, "end": v(-42.31, -30.58) * mm});
            skLineSegment(sketch, "E470", {"start": v(-42.31, -30.58) * mm, "end": v(-43.04, -30.5) * mm});
            skLineSegment(sketch, "E471", {"start": v(-43.04, -30.5) * mm, "end": v(-43.18, -31.6) * mm});
            skLineSegment(sketch, "E472", {"start": v(-43.18, -31.6) * mm, "end": v(-42.23, -31.72) * mm});
            skLineSegment(sketch, "E473", {"start": v(-42.23, -31.72) * mm, "end": v(-42.04, -31.4) * mm});
            skLineSegment(sketch, "E474", {"start": v(-42.04, -31.4) * mm, "end": v(-41.71, -31.43) * mm});
            skLineSegment(sketch, "E475", {"start": v(-41.71, -31.43) * mm, "end": v(-41.93, -32.24) * mm});
            skLineSegment(sketch, "E476", {"start": v(-41.93, -32.24) * mm, "end": v(-43.24, -32.07) * mm});
            skLineSegment(sketch, "E477", {"start": v(-41.89, -29.95) * mm, "end": v(-41.98, -30.8) * mm});
            skLineSegment(sketch, "E478", {"start": v(-41.08, -29.11) * mm, "end": v(-40.88, -29.19) * mm});
            skLineSegment(sketch, "E479", {"start": v(-40.88, -29.19) * mm, "end": v(-40.97, -31.8) * mm});
            skLineSegment(sketch, "E480", {"start": v(-40.97, -31.8) * mm, "end": v(-41.08, -31.91) * mm});
            skLineSegment(sketch, "E481", {"start": v(-41.08, -31.91) * mm, "end": v(-41.26, -31.91) * mm});
            skLineSegment(sketch, "E482", {"start": v(-41.26, -31.91) * mm, "end": v(-41.26, -32.32) * mm});
            skLineSegment(sketch, "E483", {"start": v(-41.26, -32.32) * mm, "end": v(-39.11, -32.38) * mm});
            skLineSegment(sketch, "E484", {"start": v(-39.11, -32.38) * mm, "end": v(-38.95, -31.66) * mm});
            skLineSegment(sketch, "E485", {"start": v(-38.95, -31.66) * mm, "end": v(-39.19, -31.55) * mm});
            skLineSegment(sketch, "E486", {"start": v(-39.19, -31.55) * mm, "end": v(-39.4, -31.88) * mm});
            skLineSegment(sketch, "E487", {"start": v(-39.4, -31.88) * mm, "end": v(-40.36, -31.88) * mm});
            skLineSegment(sketch, "E488", {"start": v(-40.36, -31.88) * mm, "end": v(-40.24, -29.21) * mm});
            skLineSegment(sketch, "E489", {"start": v(-40.24, -29.21) * mm, "end": v(-40.19, -29.18) * mm});
            skLineSegment(sketch, "E490", {"start": v(-40.19, -29.18) * mm, "end": v(-40, -29.18) * mm});
            skLineSegment(sketch, "E491", {"start": v(-40, -29.18) * mm, "end": v(-40, -28.83) * mm});
            skLineSegment(sketch, "E492", {"start": v(-40, -28.83) * mm, "end": v(-41, -28.77) * mm});
            skLineSegment(sketch, "E493", {"start": v(-41, -28.77) * mm, "end": v(-41.08, -29.11) * mm});
            skLineSegment(sketch, "E494", {"start": v(-38.6, -28.87) * mm, "end": v(-37.65, -28.87) * mm});
            skLineSegment(sketch, "E495", {"start": v(-37.65, -28.87) * mm, "end": v(-37.54, -29.18) * mm});
            skLineSegment(sketch, "E496", {"start": v(-37.54, -29.18) * mm, "end": v(-37.8, -29.27) * mm});
            skLineSegment(sketch, "E497", {"start": v(-37.8, -29.27) * mm, "end": v(-37.73, -31.89) * mm});
            skLineSegment(sketch, "E498", {"start": v(-37.73, -31.89) * mm, "end": v(-37.68, -32.02) * mm});
            skLineSegment(sketch, "E499", {"start": v(-37.68, -32.02) * mm, "end": v(-37.5, -32.02) * mm});
            skLineSegment(sketch, "E500", {"start": v(-37.5, -32.02) * mm, "end": v(-37.5, -32.44) * mm});
            skLineSegment(sketch, "E501", {"start": v(-37.5, -32.44) * mm, "end": v(-38.5, -32.44) * mm});
            skLineSegment(sketch, "E502", {"start": v(-38.5, -32.44) * mm, "end": v(-38.55, -32.05) * mm});
            skLineSegment(sketch, "E503", {"start": v(-38.55, -32.05) * mm, "end": v(-38.4, -32.01) * mm});
            skLineSegment(sketch, "E504", {"start": v(-38.4, -32.01) * mm, "end": v(-38.4, -31.94) * mm});
            skLineSegment(sketch, "E505", {"start": v(-38.4, -31.94) * mm, "end": v(-38.4, -29.35) * mm});
            skLineSegment(sketch, "E506", {"start": v(-38.4, -29.35) * mm, "end": v(-38.46, -29.23) * mm});
            skLineSegment(sketch, "E507", {"start": v(-38.46, -29.23) * mm, "end": v(-38.66, -29.23) * mm});
            skLineSegment(sketch, "E508", {"start": v(-38.66, -29.23) * mm, "end": v(-38.6, -28.87) * mm});
            skLineSegment(sketch, "E509", {"start": v(-36.88, -29.2) * mm, "end": v(-36.75, -29.3) * mm});
            skLineSegment(sketch, "E510", {"start": v(-36.75, -29.3) * mm, "end": v(-36.65, -31.9) * mm});
            skLineSegment(sketch, "E511", {"start": v(-36.65, -31.9) * mm, "end": v(-36.73, -32) * mm});
            skLineSegment(sketch, "E512", {"start": v(-36.73, -32) * mm, "end": v(-36.88, -31.99) * mm});
            skLineSegment(sketch, "E513", {"start": v(-36.88, -31.99) * mm, "end": v(-36.88, -32.28) * mm});
            skLineSegment(sketch, "E514", {"start": v(-36.88, -32.28) * mm, "end": v(-36.77, -32.4) * mm});
            skLineSegment(sketch, "E515", {"start": v(-36.77, -32.4) * mm, "end": v(-34.6, -32.3) * mm});
            skLineSegment(sketch, "E516", {"start": v(-34.6, -32.3) * mm, "end": v(-34.6, -31.44) * mm});
            skLineSegment(sketch, "E517", {"start": v(-34.6, -31.44) * mm, "end": v(-34.92, -31.43) * mm});
            skLineSegment(sketch, "E518", {"start": v(-34.92, -31.43) * mm, "end": v(-34.95, -31.68) * mm});
            skLineSegment(sketch, "E519", {"start": v(-34.95, -31.68) * mm, "end": v(-35.06, -31.81) * mm});
            skLineSegment(sketch, "E520", {"start": v(-35.06, -31.81) * mm, "end": v(-36.07, -31.86) * mm});
            skLineSegment(sketch, "E521", {"start": v(-36.07, -31.86) * mm, "end": v(-36.12, -30.72) * mm});
            skLineSegment(sketch, "E522", {"start": v(-36.18, -29.2) * mm, "end": v(-35.34, -29.2) * mm});
            skLineSegment(sketch, "E523", {"start": v(-35.34, -29.2) * mm, "end": v(-35.23, -29.3) * mm});
            skLineSegment(sketch, "E524", {"start": v(-35.23, -29.3) * mm, "end": v(-35.23, -29.52) * mm});
            skLineSegment(sketch, "E525", {"start": v(-35.23, -29.52) * mm, "end": v(-35.1, -29.54) * mm});
            skLineSegment(sketch, "E526", {"start": v(-35.1, -29.54) * mm, "end": v(-34.92, -29.4) * mm});
            skLineSegment(sketch, "E527", {"start": v(-34.92, -29.4) * mm, "end": v(-35.01, -28.73) * mm});
            skLineSegment(sketch, "E528", {"start": v(-35.01, -28.73) * mm, "end": v(-36.98, -28.87) * mm});
            skLineSegment(sketch, "E529", {"start": v(-36.98, -28.87) * mm, "end": v(-37.01, -29.18) * mm});
            skLineSegment(sketch, "E530", {"start": v(-37.01, -29.18) * mm, "end": v(-36.88, -29.2) * mm});
            skLineSegment(sketch, "E531", {"start": v(-36.13, -30.27) * mm, "end": v(-35.43, -30.24) * mm});
            skLineSegment(sketch, "E532", {"start": v(-35.43, -30.24) * mm, "end": v(-35.33, -30.16) * mm});
            skLineSegment(sketch, "E533", {"start": v(-35.33, -30.16) * mm, "end": v(-35.34, -30) * mm});
            skLineSegment(sketch, "E534", {"start": v(-35.34, -30) * mm, "end": v(-35.1, -30.03) * mm});
            skLineSegment(sketch, "E535", {"start": v(-35.1, -30.03) * mm, "end": v(-35.06, -30.11) * mm});
            skLineSegment(sketch, "E536", {"start": v(-35.06, -30.11) * mm, "end": v(-35.03, -30.8) * mm});
            skLineSegment(sketch, "E537", {"start": v(-35.03, -30.8) * mm, "end": v(-35.1, -30.86) * mm});
            skLineSegment(sketch, "E538", {"start": v(-35.1, -30.86) * mm, "end": v(-35.29, -30.91) * mm});
            skLineSegment(sketch, "E539", {"start": v(-35.29, -30.91) * mm, "end": v(-35.3, -30.76) * mm});
            skLineSegment(sketch, "E540", {"start": v(-35.3, -30.76) * mm, "end": v(-35.4, -30.69) * mm});
            skLineSegment(sketch, "E541", {"start": v(-35.4, -30.69) * mm, "end": v(-36.12, -30.72) * mm});
            skLineSegment(sketch, "E542.trimOffspring", {"start": v(-36.13, -30.27) * mm, "end": v(-36.18, -29.2) * mm});
            skLineSegment(sketch, "E543", {"start": v(-34.77, -28.72) * mm, "end": v(-34.82, -29.05) * mm});
            skLineSegment(sketch, "E544", {"start": v(-34.82, -29.05) * mm, "end": v(-34.6, -29.05) * mm});
            skLineSegment(sketch, "E545", {"start": v(-34.6, -29.05) * mm, "end": v(-33.1, -32.08) * mm});
            skLineSegment(sketch, "E546", {"start": v(-33.1, -32.08) * mm, "end": v(-32.47, -32.01) * mm});
            skLineSegment(sketch, "E547", {"start": v(-32.47, -32.01) * mm, "end": v(-31.92, -28.68) * mm});
            skLineSegment(sketch, "E548", {"start": v(-31.92, -28.68) * mm, "end": v(-31.7, -28.63) * mm});
            skLineSegment(sketch, "E549", {"start": v(-31.7, -28.63) * mm, "end": v(-31.84, -28.3) * mm});
            skLineSegment(sketch, "E550", {"start": v(-31.84, -28.3) * mm, "end": v(-32.7, -28.41) * mm});
            skLineSegment(sketch, "E551", {"start": v(-32.7, -28.41) * mm, "end": v(-32.7, -28.76) * mm});
            skLineSegment(sketch, "E552", {"start": v(-32.7, -28.76) * mm, "end": v(-32.52, -28.76) * mm});
            skLineSegment(sketch, "E553", {"start": v(-32.52, -28.76) * mm, "end": v(-32.86, -31.29) * mm});
            skLineSegment(sketch, "E554", {"start": v(-32.86, -31.29) * mm, "end": v(-33.91, -29) * mm});
            skLineSegment(sketch, "E555", {"start": v(-33.91, -29) * mm, "end": v(-33.7, -28.96) * mm});
            skLineSegment(sketch, "E556", {"start": v(-33.7, -28.96) * mm, "end": v(-33.83, -28.6) * mm});
            skLineSegment(sketch, "E557", {"start": v(-33.83, -28.6) * mm, "end": v(-34.77, -28.72) * mm});
            skLineSegment(sketch, "E558", {"start": v(-29.8, -29.2) * mm, "end": v(-29.8, -29.05) * mm});
            skLineSegment(sketch, "E559", {"start": v(-29.8, -29.05) * mm, "end": v(-29.52, -29.05) * mm});
            skLineSegment(sketch, "E560", {"start": v(-29.52, -29.05) * mm, "end": v(-29.32, -29.8) * mm});
            skLineSegment(sketch, "E561", {"start": v(-29.32, -29.8) * mm, "end": v(-29.58, -29.95) * mm});
            skLineSegment(sketch, "E562", {"start": v(-29.58, -29.95) * mm, "end": v(-29.7, -29.74) * mm});
            skLineSegment(sketch, "E563", {"start": v(-29.7, -29.74) * mm, "end": v(-30.41, -29.94) * mm});
            skLineSegment(sketch, "E564", {"start": v(-30.5, -29.48) * mm, "end": v(-29.8, -29.28) * mm});
            skLineSegment(sketch, "E565", {"start": v(-29.8, -29.28) * mm, "end": v(-29.8, -29.2) * mm});
            skLineSegment(sketch, "E566", {"start": v(-30.78, -28.48) * mm, "end": v(-30.55, -29.49) * mm});
            skLineSegment(sketch, "E567", {"start": v(-30.2, -31) * mm, "end": v(-29.15, -30.77) * mm});
            skLineSegment(sketch, "E568", {"start": v(-29.15, -30.77) * mm, "end": v(-29.13, -30.42) * mm});
            skLineSegment(sketch, "E569", {"start": v(-29.13, -30.42) * mm, "end": v(-28.85, -30.44) * mm});
            skLineSegment(sketch, "E570", {"start": v(-28.85, -30.44) * mm, "end": v(-28.72, -31.14) * mm});
            skLineSegment(sketch, "E571", {"start": v(-28.72, -31.14) * mm, "end": v(-30.79, -31.64) * mm});
            skLineSegment(sketch, "E572", {"start": v(-30.79, -31.64) * mm, "end": v(-30.98, -31.34) * mm});
            skLineSegment(sketch, "E573", {"start": v(-30.98, -31.34) * mm, "end": v(-30.78, -31.25) * mm});
            skLineSegment(sketch, "E574", {"start": v(-30.78, -31.25) * mm, "end": v(-30.74, -31.13) * mm});
            skLineSegment(sketch, "E575", {"start": v(-30.74, -31.13) * mm, "end": v(-31.38, -28.66) * mm});
            skLineSegment(sketch, "E576", {"start": v(-31.38, -28.66) * mm, "end": v(-31.45, -28.58) * mm});
            skLineSegment(sketch, "E577", {"start": v(-31.45, -28.58) * mm, "end": v(-31.64, -28.59) * mm});
            skLineSegment(sketch, "E578", {"start": v(-31.64, -28.59) * mm, "end": v(-31.65, -28.2) * mm});
            skLineSegment(sketch, "E579", {"start": v(-31.65, -28.2) * mm, "end": v(-29.7, -27.76) * mm});
            skLineSegment(sketch, "E580", {"start": v(-29.7, -27.76) * mm, "end": v(-29.44, -28.42) * mm});
            skLineSegment(sketch, "E581", {"start": v(-29.44, -28.42) * mm, "end": v(-29.76, -28.6) * mm});
            skLineSegment(sketch, "E582", {"start": v(-29.76, -28.6) * mm, "end": v(-29.87, -28.35) * mm});
            skLineSegment(sketch, "E583", {"start": v(-29.87, -28.35) * mm, "end": v(-30, -28.28) * mm});
            skLineSegment(sketch, "E584", {"start": v(-30, -28.28) * mm, "end": v(-30.78, -28.48) * mm});
            skLineSegment(sketch, "E585", {"start": v(-29.7, -29.74) * mm, "end": v(-30.45, -29.95) * mm});
            skLineSegment(sketch, "E586", {"start": v(-30.5, -29.48) * mm, "end": v(-30.55, -29.49) * mm});
            skLineSegment(sketch, "E587.trimOffspring", {"start": v(-30.45, -29.95) * mm, "end": v(-30.2, -31) * mm});
            skSolve(sketch);
        }
        {
            var Q0;
            Q0 = qSketchRegion(id + "F33", true);
            extrude(context, id + "F34", {"entities" : qUnion([Q0]), "operationType" : NewBodyOperationType.ADD, "depth" : 0.76 * mm});
        }
        {
            var Q0;
            Q0=makeQuery(id+"F24.opExtrude","SWEPT_BODY",BODY,{"disambiguationData":[OSD([sQuery(id+"F13.wireOp",EDGE,"E83")])]});
            var Q1;
            Q1=makeQuery(id+"F2.opExtrude","SWEPT_BODY",BODY,{"disambiguationData":[OSD([sQuery(id+"F1.wireOp",EDGE,"E1"),sQuery(id+"F1.wireOp",EDGE,"E2"),sQuery(id+"F1.wireOp",EDGE,"E3"),sQuery(id+"F1.wireOp",EDGE,"E4"),sQuery(id+"F1.wireOp",EDGE,"E5"),sQuery(id+"F1.wireOp",EDGE,"E6"),sQuery(id+"F1.wireOp",EDGE,"E7"),sQuery(id+"F1.wireOp",EDGE,"E8"),sQuery(id+"F1.wireOp",EDGE,"E9"),sQuery(id+"F1.wireOp",EDGE,"E10"),sQuery(id+"F1.wireOp",EDGE,"E11"),sQuery(id+"F1.wireOp",EDGE,"E12"),sQuery(id+"F1.wireOp",EDGE,"E13"),sQuery(id+"F1.wireOp",EDGE,"E14"),sQuery(id+"F1.wireOp",EDGE,"E15"),sQuery(id+"F1.wireOp",EDGE,"E16"),sQuery(id+"F1.wireOp",EDGE,"E17"),sQuery(id+"F1.wireOp",EDGE,"E18.trimOffspring"),sQuery(id+"F1.wireOp",EDGE,"E19"),sQuery(id+"F1.wireOp",EDGE,"E20"),sQuery(id+"F1.wireOp",EDGE,"E21"),sQuery(id+"F1.wireOp",EDGE,"E22"),sQuery(id+"F1.wireOp",EDGE,"E23"),sQuery(id+"F1.wireOp",EDGE,"E24"),sQuery(id+"F1.wireOp",EDGE,"E25"),sQuery(id+"F1.wireOp",EDGE,"E26"),sQuery(id+"F1.wireOp",EDGE,"E27"),sQuery(id+"F1.wireOp",EDGE,"E28"),sQuery(id+"F1.wireOp",EDGE,"E29")])]});
            var Q2;
            Q2=makeQuery(id+"F12.opPattern","COPY",BODY,{"derivedFrom":makeQuery(id+"F2.opExtrude","SWEPT_BODY",BODY,{"disambiguationData":[OSD([sQuery(id+"F1.wireOp",EDGE,"E1"),sQuery(id+"F1.wireOp",EDGE,"E2"),sQuery(id+"F1.wireOp",EDGE,"E3"),sQuery(id+"F1.wireOp",EDGE,"E4"),sQuery(id+"F1.wireOp",EDGE,"E5"),sQuery(id+"F1.wireOp",EDGE,"E6"),sQuery(id+"F1.wireOp",EDGE,"E7"),sQuery(id+"F1.wireOp",EDGE,"E8"),sQuery(id+"F1.wireOp",EDGE,"E9"),sQuery(id+"F1.wireOp",EDGE,"E10"),sQuery(id+"F1.wireOp",EDGE,"E11"),sQuery(id+"F1.wireOp",EDGE,"E12"),sQuery(id+"F1.wireOp",EDGE,"E13"),sQuery(id+"F1.wireOp",EDGE,"E14"),sQuery(id+"F1.wireOp",EDGE,"E15"),sQuery(id+"F1.wireOp",EDGE,"E16"),sQuery(id+"F1.wireOp",EDGE,"E17"),sQuery(id+"F1.wireOp",EDGE,"E18.trimOffspring"),sQuery(id+"F1.wireOp",EDGE,"E19"),sQuery(id+"F1.wireOp",EDGE,"E20"),sQuery(id+"F1.wireOp",EDGE,"E21"),sQuery(id+"F1.wireOp",EDGE,"E22"),sQuery(id+"F1.wireOp",EDGE,"E23"),sQuery(id+"F1.wireOp",EDGE,"E24"),sQuery(id+"F1.wireOp",EDGE,"E25"),sQuery(id+"F1.wireOp",EDGE,"E26"),sQuery(id+"F1.wireOp",EDGE,"E27"),sQuery(id+"F1.wireOp",EDGE,"E28"),sQuery(id+"F1.wireOp",EDGE,"E29")])]}),"instanceName":"1"});
            var Q3;
            Q3=makeQuery(id+"F12.opPattern","COPY",BODY,{"derivedFrom":makeQuery(id+"F2.opExtrude","SWEPT_BODY",BODY,{"disambiguationData":[OSD([sQuery(id+"F1.wireOp",EDGE,"E1"),sQuery(id+"F1.wireOp",EDGE,"E2"),sQuery(id+"F1.wireOp",EDGE,"E3"),sQuery(id+"F1.wireOp",EDGE,"E4"),sQuery(id+"F1.wireOp",EDGE,"E5"),sQuery(id+"F1.wireOp",EDGE,"E6"),sQuery(id+"F1.wireOp",EDGE,"E7"),sQuery(id+"F1.wireOp",EDGE,"E8"),sQuery(id+"F1.wireOp",EDGE,"E9"),sQuery(id+"F1.wireOp",EDGE,"E10"),sQuery(id+"F1.wireOp",EDGE,"E11"),sQuery(id+"F1.wireOp",EDGE,"E12"),sQuery(id+"F1.wireOp",EDGE,"E13"),sQuery(id+"F1.wireOp",EDGE,"E14"),sQuery(id+"F1.wireOp",EDGE,"E15"),sQuery(id+"F1.wireOp",EDGE,"E16"),sQuery(id+"F1.wireOp",EDGE,"E17"),sQuery(id+"F1.wireOp",EDGE,"E18.trimOffspring"),sQuery(id+"F1.wireOp",EDGE,"E19"),sQuery(id+"F1.wireOp",EDGE,"E20"),sQuery(id+"F1.wireOp",EDGE,"E21"),sQuery(id+"F1.wireOp",EDGE,"E22"),sQuery(id+"F1.wireOp",EDGE,"E23"),sQuery(id+"F1.wireOp",EDGE,"E24"),sQuery(id+"F1.wireOp",EDGE,"E25"),sQuery(id+"F1.wireOp",EDGE,"E26"),sQuery(id+"F1.wireOp",EDGE,"E27"),sQuery(id+"F1.wireOp",EDGE,"E28"),sQuery(id+"F1.wireOp",EDGE,"E29")])]}),"instanceName":"2"});
            var Q4;
            Q4=makeQuery(id+"F12.opPattern","COPY",BODY,{"derivedFrom":makeQuery(id+"F2.opExtrude","SWEPT_BODY",BODY,{"disambiguationData":[OSD([sQuery(id+"F1.wireOp",EDGE,"E1"),sQuery(id+"F1.wireOp",EDGE,"E2"),sQuery(id+"F1.wireOp",EDGE,"E3"),sQuery(id+"F1.wireOp",EDGE,"E4"),sQuery(id+"F1.wireOp",EDGE,"E5"),sQuery(id+"F1.wireOp",EDGE,"E6"),sQuery(id+"F1.wireOp",EDGE,"E7"),sQuery(id+"F1.wireOp",EDGE,"E8"),sQuery(id+"F1.wireOp",EDGE,"E9"),sQuery(id+"F1.wireOp",EDGE,"E10"),sQuery(id+"F1.wireOp",EDGE,"E11"),sQuery(id+"F1.wireOp",EDGE,"E12"),sQuery(id+"F1.wireOp",EDGE,"E13"),sQuery(id+"F1.wireOp",EDGE,"E14"),sQuery(id+"F1.wireOp",EDGE,"E15"),sQuery(id+"F1.wireOp",EDGE,"E16"),sQuery(id+"F1.wireOp",EDGE,"E17"),sQuery(id+"F1.wireOp",EDGE,"E18.trimOffspring"),sQuery(id+"F1.wireOp",EDGE,"E19"),sQuery(id+"F1.wireOp",EDGE,"E20"),sQuery(id+"F1.wireOp",EDGE,"E21"),sQuery(id+"F1.wireOp",EDGE,"E22"),sQuery(id+"F1.wireOp",EDGE,"E23"),sQuery(id+"F1.wireOp",EDGE,"E24"),sQuery(id+"F1.wireOp",EDGE,"E25"),sQuery(id+"F1.wireOp",EDGE,"E26"),sQuery(id+"F1.wireOp",EDGE,"E27"),sQuery(id+"F1.wireOp",EDGE,"E28"),sQuery(id+"F1.wireOp",EDGE,"E29")])]}),"instanceName":"3"});
            var Q5;
            Q5=makeQuery(id+"F12.opPattern","COPY",BODY,{"derivedFrom":makeQuery(id+"F2.opExtrude","SWEPT_BODY",BODY,{"disambiguationData":[OSD([sQuery(id+"F1.wireOp",EDGE,"E1"),sQuery(id+"F1.wireOp",EDGE,"E2"),sQuery(id+"F1.wireOp",EDGE,"E3"),sQuery(id+"F1.wireOp",EDGE,"E4"),sQuery(id+"F1.wireOp",EDGE,"E5"),sQuery(id+"F1.wireOp",EDGE,"E6"),sQuery(id+"F1.wireOp",EDGE,"E7"),sQuery(id+"F1.wireOp",EDGE,"E8"),sQuery(id+"F1.wireOp",EDGE,"E9"),sQuery(id+"F1.wireOp",EDGE,"E10"),sQuery(id+"F1.wireOp",EDGE,"E11"),sQuery(id+"F1.wireOp",EDGE,"E12"),sQuery(id+"F1.wireOp",EDGE,"E13"),sQuery(id+"F1.wireOp",EDGE,"E14"),sQuery(id+"F1.wireOp",EDGE,"E15"),sQuery(id+"F1.wireOp",EDGE,"E16"),sQuery(id+"F1.wireOp",EDGE,"E17"),sQuery(id+"F1.wireOp",EDGE,"E18.trimOffspring"),sQuery(id+"F1.wireOp",EDGE,"E19"),sQuery(id+"F1.wireOp",EDGE,"E20"),sQuery(id+"F1.wireOp",EDGE,"E21"),sQuery(id+"F1.wireOp",EDGE,"E22"),sQuery(id+"F1.wireOp",EDGE,"E23"),sQuery(id+"F1.wireOp",EDGE,"E24"),sQuery(id+"F1.wireOp",EDGE,"E25"),sQuery(id+"F1.wireOp",EDGE,"E26"),sQuery(id+"F1.wireOp",EDGE,"E27"),sQuery(id+"F1.wireOp",EDGE,"E28"),sQuery(id+"F1.wireOp",EDGE,"E29")])]}),"instanceName":"4"});
            var Q6;
            Q6=makeQuery(id+"F12.opPattern","COPY",BODY,{"derivedFrom":makeQuery(id+"F2.opExtrude","SWEPT_BODY",BODY,{"disambiguationData":[OSD([sQuery(id+"F1.wireOp",EDGE,"E1"),sQuery(id+"F1.wireOp",EDGE,"E2"),sQuery(id+"F1.wireOp",EDGE,"E3"),sQuery(id+"F1.wireOp",EDGE,"E4"),sQuery(id+"F1.wireOp",EDGE,"E5"),sQuery(id+"F1.wireOp",EDGE,"E6"),sQuery(id+"F1.wireOp",EDGE,"E7"),sQuery(id+"F1.wireOp",EDGE,"E8"),sQuery(id+"F1.wireOp",EDGE,"E9"),sQuery(id+"F1.wireOp",EDGE,"E10"),sQuery(id+"F1.wireOp",EDGE,"E11"),sQuery(id+"F1.wireOp",EDGE,"E12"),sQuery(id+"F1.wireOp",EDGE,"E13"),sQuery(id+"F1.wireOp",EDGE,"E14"),sQuery(id+"F1.wireOp",EDGE,"E15"),sQuery(id+"F1.wireOp",EDGE,"E16"),sQuery(id+"F1.wireOp",EDGE,"E17"),sQuery(id+"F1.wireOp",EDGE,"E18.trimOffspring"),sQuery(id+"F1.wireOp",EDGE,"E19"),sQuery(id+"F1.wireOp",EDGE,"E20"),sQuery(id+"F1.wireOp",EDGE,"E21"),sQuery(id+"F1.wireOp",EDGE,"E22"),sQuery(id+"F1.wireOp",EDGE,"E23"),sQuery(id+"F1.wireOp",EDGE,"E24"),sQuery(id+"F1.wireOp",EDGE,"E25"),sQuery(id+"F1.wireOp",EDGE,"E26"),sQuery(id+"F1.wireOp",EDGE,"E27"),sQuery(id+"F1.wireOp",EDGE,"E28"),sQuery(id+"F1.wireOp",EDGE,"E29")])]}),"instanceName":"5"});
            var Q7;
            Q7=makeQuery(id+"F14.opExtrude","SWEPT_BODY",BODY,{"disambiguationData":[OSD([sQuery(id+"F13.wireOp",EDGE,"E83")])]});
            booleanBodies(context, id + "F35", {"operationType" : BooleanOperationType.UNION, "tools" : qUnion([Q0, Q1, Q2, Q3, Q4, Q5, Q6, Q7])});
        }
        {
            var Q0;
            {var subQ0=sQuery(id+"F15.wireOp",EDGE,"E84");var subQ2=sQuery(id+"F1.wireOp",EDGE,"E27");var subQ3=sQuery(id+"F1.wireOp",EDGE,"E26");var subQ4=sQuery(id+"F1.wireOp",EDGE,"E25");var subQ5=sQuery(id+"F1.wireOp",EDGE,"E24");var subQ6=sQuery(id+"F1.wireOp",EDGE,"E23");var subQ7=sQuery(id+"F1.wireOp",EDGE,"E22");var subQ8=sQuery(id+"F1.wireOp",EDGE,"E19");var subQ9=sQuery(id+"F1.wireOp",EDGE,"E18.trimOffspring");var subQ10=sQuery(id+"F1.wireOp",EDGE,"E17");var subQ11=sQuery(id+"F1.wireOp",EDGE,"E16");var subQ12=sQuery(id+"F1.wireOp",EDGE,"E15");var subQ13=sQuery(id+"F1.wireOp",EDGE,"E14");var subQ14=sQuery(id+"F1.wireOp",EDGE,"E10");var subQ15=sQuery(id+"F1.wireOp",EDGE,"E9");var subQ16=sQuery(id+"F1.wireOp",EDGE,"E8");var subQ17=sQuery(id+"F1.wireOp",EDGE,"E7");var subQ18=sQuery(id+"F1.wireOp",EDGE,"E6");var subQ19=makeQuery(id+"F2.opExtrude","CAP_FACE",FACE,{"disambiguationData":[OSD([sQuery(id+"F1.wireOp",EDGE,"E1"),sQuery(id+"F1.wireOp",EDGE,"E2"),sQuery(id+"F1.wireOp",EDGE,"E3"),sQuery(id+"F1.wireOp",EDGE,"E4"),sQuery(id+"F1.wireOp",EDGE,"E5"),subQ18,subQ17,subQ16,subQ15,subQ14,sQuery(id+"F1.wireOp",EDGE,"E11"),sQuery(id+"F1.wireOp",EDGE,"E12"),sQuery(id+"F1.wireOp",EDGE,"E13"),subQ13,subQ12,subQ11,subQ10,subQ9,subQ8,sQuery(id+"F1.wireOp",EDGE,"E20"),sQuery(id+"F1.wireOp",EDGE,"E21"),subQ7,subQ6,subQ5,subQ4,subQ3,subQ2,sQuery(id+"F1.wireOp",EDGE,"E28"),sQuery(id+"F1.wireOp",EDGE,"E29")])],"isStart":false});var subQ20=makeQuery(id+"F12.opPattern","COPY",FACE,{"derivedFrom":makeQuery(id+"F4.boolean.opBoolean","MERGE",FACE,{"derivedFrom":[subQ19,makeQuery(id+"F4.opPattern","COPY",FACE,{"derivedFrom":subQ19,"instanceName":"1"})]}),"instanceName":"3"});var subQ24=makeQuery(id+"F16.opExtrude","CAP_FACE",FACE,{"disambiguationData":[OSD([subQ0])],"isStart":true});var subQ39=makeQuery(id+"F2.opExtrude","SWEPT_FACE",FACE,{"disambiguationData":[OSD([subQ18])]});Q0=makeQuery(id+"F35.opBoolean","SPLIT",FACE,{"disambiguationData":[TD([makeQuery(id+"F12.opPattern","COPY",FACE,{"derivedFrom":subQ39,"instanceName":"3"})])],"derivedFrom":makeQuery(id+"F16.boolean.opBoolean","MERGE",FACE,{"derivedFrom":[subQ20,subQ24]})});}
            var Q1;
            {var subQ2=sQuery(id+"F1.wireOp",EDGE,"E13");var subQ3=sQuery(id+"F1.wireOp",EDGE,"E11");var subQ5=sQuery(id+"F1.wireOp",EDGE,"E12");var subQ6=sQuery(id+"F1.wireOp",EDGE,"E4");var subQ7=sQuery(id+"F1.wireOp",EDGE,"E2");var subQ8=makeQuery(id+"F2.opExtrude","CAP_FACE",FACE,{"disambiguationData":[OSD([sQuery(id+"F1.wireOp",EDGE,"E1"),subQ7,sQuery(id+"F1.wireOp",EDGE,"E3"),subQ6,sQuery(id+"F1.wireOp",EDGE,"E5"),sQuery(id+"F1.wireOp",EDGE,"E6"),sQuery(id+"F1.wireOp",EDGE,"E7"),sQuery(id+"F1.wireOp",EDGE,"E8"),sQuery(id+"F1.wireOp",EDGE,"E9"),sQuery(id+"F1.wireOp",EDGE,"E10"),subQ3,subQ5,subQ2,sQuery(id+"F1.wireOp",EDGE,"E14"),sQuery(id+"F1.wireOp",EDGE,"E15"),sQuery(id+"F1.wireOp",EDGE,"E16"),sQuery(id+"F1.wireOp",EDGE,"E17"),sQuery(id+"F1.wireOp",EDGE,"E18.trimOffspring"),sQuery(id+"F1.wireOp",EDGE,"E19"),sQuery(id+"F1.wireOp",EDGE,"E20"),sQuery(id+"F1.wireOp",EDGE,"E21"),sQuery(id+"F1.wireOp",EDGE,"E22"),sQuery(id+"F1.wireOp",EDGE,"E23"),sQuery(id+"F1.wireOp",EDGE,"E24"),sQuery(id+"F1.wireOp",EDGE,"E25"),sQuery(id+"F1.wireOp",EDGE,"E26"),sQuery(id+"F1.wireOp",EDGE,"E27"),sQuery(id+"F1.wireOp",EDGE,"E28"),sQuery(id+"F1.wireOp",EDGE,"E29")])],"isStart":false});Q1=makeQuery(id+"F35.opBoolean","SPLIT",FACE,{"disambiguationData":[TD([makeQuery(id+"F12.opPattern","COPY",FACE,{"derivedFrom":makeQuery(id+"F2.opExtrude","SWEPT_FACE",FACE,{"disambiguationData":[OSD([subQ2])]}),"instanceName":"3"})])],"derivedFrom":makeQuery(id+"F16.boolean.opBoolean","MERGE",FACE,{"derivedFrom":[makeQuery(id+"F12.opPattern","COPY",FACE,{"derivedFrom":makeQuery(id+"F4.boolean.opBoolean","MERGE",FACE,{"derivedFrom":[subQ8,makeQuery(id+"F4.opPattern","COPY",FACE,{"derivedFrom":subQ8,"instanceName":"1"})]}),"instanceName":"3"}),makeQuery(id+"F16.opExtrude","CAP_FACE",FACE,{"disambiguationData":[OSD([sQuery(id+"F15.wireOp",EDGE,"E84")])],"isStart":true})]})});}
            var Q2;
            {var subQ0=sQuery(id+"F5.wireOp",EDGE,"E53");Q2=makeQuery(id+"F12.opPattern","COPY",FACE,{"derivedFrom":makeQuery(id+"F8.boolean.opBoolean","MERGE",FACE,{"derivedFrom":[makeQuery(id+"F6.boolean.opBoolean","COPY",FACE,{"derivedFrom":makeQuery(id+"F6.opExtrude","CAP_FACE",FACE,{"disambiguationData":[OSD([sQuery(id+"F5.wireOp",EDGE,"E30"),sQuery(id+"F5.wireOp",EDGE,"E32"),sQuery(id+"F5.wireOp",EDGE,"E33"),sQuery(id+"F5.wireOp",EDGE,"E34"),sQuery(id+"F5.wireOp",EDGE,"E35"),sQuery(id+"F5.wireOp",EDGE,"E36"),sQuery(id+"F5.wireOp",EDGE,"E37"),sQuery(id+"F5.wireOp",EDGE,"E38.trimOffspring"),sQuery(id+"F5.wireOp",EDGE,"E39"),sQuery(id+"F5.wireOp",EDGE,"E40"),sQuery(id+"F5.wireOp",EDGE,"E41"),sQuery(id+"F5.wireOp",EDGE,"E42"),sQuery(id+"F5.wireOp",EDGE,"E43"),sQuery(id+"F5.wireOp",EDGE,"E44"),sQuery(id+"F5.wireOp",EDGE,"E45"),sQuery(id+"F5.wireOp",EDGE,"E46"),sQuery(id+"F5.wireOp",EDGE,"E47"),subQ0,sQuery(id+"F5.wireOp",EDGE,"E54")])],"isStart":false})}),makeQuery(id+"F8.opExtrude","CAP_FACE",FACE,{"disambiguationData":[OSD([subQ0,sQuery(id+"F7.wireOp",EDGE,"E55"),sQuery(id+"F7.wireOp",EDGE,"E56"),sQuery(id+"F7.wireOp",EDGE,"E57"),sQuery(id+"F7.wireOp",EDGE,"E58.right"),sQuery(id+"F7.wireOp",EDGE,"E62"),sQuery(id+"F7.wireOp",EDGE,"E65"),sQuery(id+"F7.wireOp",EDGE,"E66"),sQuery(id+"F7.wireOp",EDGE,"E67"),sQuery(id+"F7.wireOp",EDGE,"E68"),sQuery(id+"F7.wireOp",EDGE,"E69"),sQuery(id+"F7.wireOp",EDGE,"E70"),sQuery(id+"F7.wireOp",EDGE,"E72"),sQuery(id+"F7.wireOp",EDGE,"E74"),sQuery(id+"F7.wireOp",EDGE,"E75"),sQuery(id+"F7.wireOp",EDGE,"E76.trimOffspring")])],"isStart":false})]}),"instanceName":"3"});}
            var Q3;
            Q3=makeQuery(id+"F12.opPattern","COPY",FACE,{"derivedFrom":makeQuery(id+"F6.boolean.opBoolean","COPY",FACE,{"derivedFrom":makeQuery(id+"F6.opExtrude","CAP_FACE",FACE,{"disambiguationData":[OSD([sQuery(id+"F5.wireOp",EDGE,"E48"),sQuery(id+"F5.wireOp",EDGE,"E49"),sQuery(id+"F5.wireOp",EDGE,"E50"),sQuery(id+"F5.wireOp",EDGE,"E51"),sQuery(id+"F5.wireOp",EDGE,"E52")])],"isStart":false})}),"instanceName":"3"});
            var Q4;
            {var subQ2=sQuery(id+"F1.wireOp",EDGE,"E13");var subQ3=sQuery(id+"F1.wireOp",EDGE,"E12");var subQ5=sQuery(id+"F1.wireOp",EDGE,"E11");var subQ6=sQuery(id+"F1.wireOp",EDGE,"E4");var subQ7=sQuery(id+"F1.wireOp",EDGE,"E2");var subQ8=makeQuery(id+"F2.opExtrude","CAP_FACE",FACE,{"disambiguationData":[OSD([sQuery(id+"F1.wireOp",EDGE,"E1"),subQ7,sQuery(id+"F1.wireOp",EDGE,"E3"),subQ6,sQuery(id+"F1.wireOp",EDGE,"E5"),sQuery(id+"F1.wireOp",EDGE,"E6"),sQuery(id+"F1.wireOp",EDGE,"E7"),sQuery(id+"F1.wireOp",EDGE,"E8"),sQuery(id+"F1.wireOp",EDGE,"E9"),sQuery(id+"F1.wireOp",EDGE,"E10"),subQ5,subQ3,subQ2,sQuery(id+"F1.wireOp",EDGE,"E14"),sQuery(id+"F1.wireOp",EDGE,"E15"),sQuery(id+"F1.wireOp",EDGE,"E16"),sQuery(id+"F1.wireOp",EDGE,"E17"),sQuery(id+"F1.wireOp",EDGE,"E18.trimOffspring"),sQuery(id+"F1.wireOp",EDGE,"E19"),sQuery(id+"F1.wireOp",EDGE,"E20"),sQuery(id+"F1.wireOp",EDGE,"E21"),sQuery(id+"F1.wireOp",EDGE,"E22"),sQuery(id+"F1.wireOp",EDGE,"E23"),sQuery(id+"F1.wireOp",EDGE,"E24"),sQuery(id+"F1.wireOp",EDGE,"E25"),sQuery(id+"F1.wireOp",EDGE,"E26"),sQuery(id+"F1.wireOp",EDGE,"E27"),sQuery(id+"F1.wireOp",EDGE,"E28"),sQuery(id+"F1.wireOp",EDGE,"E29")])],"isStart":false});Q4=makeQuery(id+"F35.opBoolean","SPLIT",FACE,{"disambiguationData":[TD([makeQuery(id+"F12.opPattern","COPY",FACE,{"derivedFrom":makeQuery(id+"F4.opPattern","COPY",FACE,{"derivedFrom":makeQuery(id+"F2.opExtrude","SWEPT_FACE",FACE,{"disambiguationData":[OSD([subQ2])]}),"instanceName":"1"}),"instanceName":"3"})])],"derivedFrom":makeQuery(id+"F16.boolean.opBoolean","MERGE",FACE,{"derivedFrom":[makeQuery(id+"F12.opPattern","COPY",FACE,{"derivedFrom":makeQuery(id+"F4.boolean.opBoolean","MERGE",FACE,{"derivedFrom":[subQ8,makeQuery(id+"F4.opPattern","COPY",FACE,{"derivedFrom":subQ8,"instanceName":"1"})]}),"instanceName":"3"}),makeQuery(id+"F16.opExtrude","CAP_FACE",FACE,{"disambiguationData":[OSD([sQuery(id+"F15.wireOp",EDGE,"E84")])],"isStart":true})]})});}
            var Q5;
            Q5=makeQuery(id+"F12.opPattern","COPY",FACE,{"derivedFrom":makeQuery(id+"F8.boolean.opBoolean","COPY",FACE,{"derivedFrom":makeQuery(id+"F8.opExtrude","CAP_FACE",FACE,{"disambiguationData":[OSD([sQuery(id+"F7.wireOp",EDGE,"E77"),sQuery(id+"F7.wireOp",EDGE,"E78"),sQuery(id+"F7.wireOp",EDGE,"E79"),sQuery(id+"F7.wireOp",EDGE,"E80")])],"isStart":false})}),"instanceName":"3"});
            var Q6;
            Q6=makeQuery(id+"F12.opPattern","COPY",FACE,{"derivedFrom":makeQuery(id+"F8.boolean.opBoolean","COPY",FACE,{"derivedFrom":makeQuery(id+"F8.opExtrude","CAP_FACE",FACE,{"disambiguationData":[OSD([sQuery(id+"F7.wireOp",EDGE,"E77"),sQuery(id+"F7.wireOp",EDGE,"E78"),sQuery(id+"F7.wireOp",EDGE,"E79"),sQuery(id+"F7.wireOp",EDGE,"E80")])],"isStart":false})}),"instanceName":"2"});
            var Q7;
            {var subQ0=sQuery(id+"F5.wireOp",EDGE,"E53");Q7=makeQuery(id+"F12.opPattern","COPY",FACE,{"derivedFrom":makeQuery(id+"F8.boolean.opBoolean","MERGE",FACE,{"derivedFrom":[makeQuery(id+"F6.boolean.opBoolean","COPY",FACE,{"derivedFrom":makeQuery(id+"F6.opExtrude","CAP_FACE",FACE,{"disambiguationData":[OSD([sQuery(id+"F5.wireOp",EDGE,"E30"),sQuery(id+"F5.wireOp",EDGE,"E32"),sQuery(id+"F5.wireOp",EDGE,"E33"),sQuery(id+"F5.wireOp",EDGE,"E34"),sQuery(id+"F5.wireOp",EDGE,"E35"),sQuery(id+"F5.wireOp",EDGE,"E36"),sQuery(id+"F5.wireOp",EDGE,"E37"),sQuery(id+"F5.wireOp",EDGE,"E38.trimOffspring"),sQuery(id+"F5.wireOp",EDGE,"E39"),sQuery(id+"F5.wireOp",EDGE,"E40"),sQuery(id+"F5.wireOp",EDGE,"E41"),sQuery(id+"F5.wireOp",EDGE,"E42"),sQuery(id+"F5.wireOp",EDGE,"E43"),sQuery(id+"F5.wireOp",EDGE,"E44"),sQuery(id+"F5.wireOp",EDGE,"E45"),sQuery(id+"F5.wireOp",EDGE,"E46"),sQuery(id+"F5.wireOp",EDGE,"E47"),subQ0,sQuery(id+"F5.wireOp",EDGE,"E54")])],"isStart":false})}),makeQuery(id+"F8.opExtrude","CAP_FACE",FACE,{"disambiguationData":[OSD([subQ0,sQuery(id+"F7.wireOp",EDGE,"E55"),sQuery(id+"F7.wireOp",EDGE,"E56"),sQuery(id+"F7.wireOp",EDGE,"E57"),sQuery(id+"F7.wireOp",EDGE,"E58.right"),sQuery(id+"F7.wireOp",EDGE,"E62"),sQuery(id+"F7.wireOp",EDGE,"E65"),sQuery(id+"F7.wireOp",EDGE,"E66"),sQuery(id+"F7.wireOp",EDGE,"E67"),sQuery(id+"F7.wireOp",EDGE,"E68"),sQuery(id+"F7.wireOp",EDGE,"E69"),sQuery(id+"F7.wireOp",EDGE,"E70"),sQuery(id+"F7.wireOp",EDGE,"E72"),sQuery(id+"F7.wireOp",EDGE,"E74"),sQuery(id+"F7.wireOp",EDGE,"E75"),sQuery(id+"F7.wireOp",EDGE,"E76.trimOffspring")])],"isStart":false})]}),"instanceName":"2"});}
            var Q8;
            {var subQ2=sQuery(id+"F1.wireOp",EDGE,"E13");var subQ3=sQuery(id+"F1.wireOp",EDGE,"E12");var subQ5=sQuery(id+"F1.wireOp",EDGE,"E11");var subQ6=sQuery(id+"F1.wireOp",EDGE,"E4");var subQ7=sQuery(id+"F1.wireOp",EDGE,"E2");var subQ8=makeQuery(id+"F2.opExtrude","CAP_FACE",FACE,{"disambiguationData":[OSD([sQuery(id+"F1.wireOp",EDGE,"E1"),subQ7,sQuery(id+"F1.wireOp",EDGE,"E3"),subQ6,sQuery(id+"F1.wireOp",EDGE,"E5"),sQuery(id+"F1.wireOp",EDGE,"E6"),sQuery(id+"F1.wireOp",EDGE,"E7"),sQuery(id+"F1.wireOp",EDGE,"E8"),sQuery(id+"F1.wireOp",EDGE,"E9"),sQuery(id+"F1.wireOp",EDGE,"E10"),subQ5,subQ3,subQ2,sQuery(id+"F1.wireOp",EDGE,"E14"),sQuery(id+"F1.wireOp",EDGE,"E15"),sQuery(id+"F1.wireOp",EDGE,"E16"),sQuery(id+"F1.wireOp",EDGE,"E17"),sQuery(id+"F1.wireOp",EDGE,"E18.trimOffspring"),sQuery(id+"F1.wireOp",EDGE,"E19"),sQuery(id+"F1.wireOp",EDGE,"E20"),sQuery(id+"F1.wireOp",EDGE,"E21"),sQuery(id+"F1.wireOp",EDGE,"E22"),sQuery(id+"F1.wireOp",EDGE,"E23"),sQuery(id+"F1.wireOp",EDGE,"E24"),sQuery(id+"F1.wireOp",EDGE,"E25"),sQuery(id+"F1.wireOp",EDGE,"E26"),sQuery(id+"F1.wireOp",EDGE,"E27"),sQuery(id+"F1.wireOp",EDGE,"E28"),sQuery(id+"F1.wireOp",EDGE,"E29")])],"isStart":false});Q8=makeQuery(id+"F35.opBoolean","SPLIT",FACE,{"disambiguationData":[TD([makeQuery(id+"F12.opPattern","COPY",FACE,{"derivedFrom":makeQuery(id+"F4.opPattern","COPY",FACE,{"derivedFrom":makeQuery(id+"F2.opExtrude","SWEPT_FACE",FACE,{"disambiguationData":[OSD([subQ2])]}),"instanceName":"1"}),"instanceName":"2"})])],"derivedFrom":makeQuery(id+"F12.opPattern","COPY",FACE,{"derivedFrom":makeQuery(id+"F4.boolean.opBoolean","MERGE",FACE,{"derivedFrom":[subQ8,makeQuery(id+"F4.opPattern","COPY",FACE,{"derivedFrom":subQ8,"instanceName":"1"})]}),"instanceName":"2"})});}
            var Q9;
            {var subQ0=sQuery(id+"F1.wireOp",EDGE,"E16");var subQ1=sQuery(id+"F1.wireOp",EDGE,"E8");var subQ3=sQuery(id+"F1.wireOp",EDGE,"E14");var subQ4=sQuery(id+"F1.wireOp",EDGE,"E7");var subQ6=sQuery(id+"F1.wireOp",EDGE,"E17");var subQ8=sQuery(id+"F1.wireOp",EDGE,"E15");var subQ10=sQuery(id+"F1.wireOp",EDGE,"E29");var subQ12=sQuery(id+"F1.wireOp",EDGE,"E28");var subQ14=sQuery(id+"F1.wireOp",EDGE,"E27");var subQ16=sQuery(id+"F1.wireOp",EDGE,"E26");var subQ18=sQuery(id+"F1.wireOp",EDGE,"E25");var subQ20=sQuery(id+"F1.wireOp",EDGE,"E24");var subQ22=sQuery(id+"F1.wireOp",EDGE,"E23");var subQ24=sQuery(id+"F1.wireOp",EDGE,"E22");var subQ26=sQuery(id+"F1.wireOp",EDGE,"E21");var subQ28=sQuery(id+"F1.wireOp",EDGE,"E19");var subQ30=sQuery(id+"F1.wireOp",EDGE,"E18.trimOffspring");var subQ32=sQuery(id+"F1.wireOp",EDGE,"E10");var subQ34=sQuery(id+"F1.wireOp",EDGE,"E6");var subQ35=makeQuery(id+"F2.opExtrude","SWEPT_FACE",FACE,{"disambiguationData":[OSD([subQ34])]});var subQ38=sQuery(id+"F1.wireOp",EDGE,"E9");var subQ45=makeQuery(id+"F2.opExtrude","CAP_FACE",FACE,{"disambiguationData":[OSD([sQuery(id+"F1.wireOp",EDGE,"E1"),sQuery(id+"F1.wireOp",EDGE,"E2"),sQuery(id+"F1.wireOp",EDGE,"E3"),sQuery(id+"F1.wireOp",EDGE,"E4"),sQuery(id+"F1.wireOp",EDGE,"E5"),subQ34,subQ4,subQ1,subQ38,subQ32,sQuery(id+"F1.wireOp",EDGE,"E11"),sQuery(id+"F1.wireOp",EDGE,"E12"),sQuery(id+"F1.wireOp",EDGE,"E13"),subQ3,subQ8,subQ0,subQ6,subQ30,subQ28,sQuery(id+"F1.wireOp",EDGE,"E20"),subQ26,subQ24,subQ22,subQ20,subQ18,subQ16,subQ14,subQ12,subQ10])],"isStart":false});Q9=makeQuery(id+"F35.opBoolean","SPLIT",FACE,{"disambiguationData":[TD([makeQuery(id+"F12.opPattern","COPY",FACE,{"derivedFrom":subQ35,"instanceName":"2"})])],"derivedFrom":makeQuery(id+"F12.opPattern","COPY",FACE,{"derivedFrom":makeQuery(id+"F4.boolean.opBoolean","MERGE",FACE,{"derivedFrom":[subQ45,makeQuery(id+"F4.opPattern","COPY",FACE,{"derivedFrom":subQ45,"instanceName":"1"})]}),"instanceName":"2"})});}
            var Q10;
            Q10=makeQuery(id+"F12.opPattern","COPY",FACE,{"derivedFrom":makeQuery(id+"F6.boolean.opBoolean","COPY",FACE,{"derivedFrom":makeQuery(id+"F6.opExtrude","CAP_FACE",FACE,{"disambiguationData":[OSD([sQuery(id+"F5.wireOp",EDGE,"E48"),sQuery(id+"F5.wireOp",EDGE,"E49"),sQuery(id+"F5.wireOp",EDGE,"E50"),sQuery(id+"F5.wireOp",EDGE,"E51"),sQuery(id+"F5.wireOp",EDGE,"E52")])],"isStart":false})}),"instanceName":"2"});
            var Q11;
            {var subQ2=sQuery(id+"F1.wireOp",EDGE,"E13");var subQ3=sQuery(id+"F1.wireOp",EDGE,"E11");var subQ5=sQuery(id+"F1.wireOp",EDGE,"E12");var subQ6=sQuery(id+"F1.wireOp",EDGE,"E4");var subQ7=sQuery(id+"F1.wireOp",EDGE,"E2");var subQ8=makeQuery(id+"F2.opExtrude","CAP_FACE",FACE,{"disambiguationData":[OSD([sQuery(id+"F1.wireOp",EDGE,"E1"),subQ7,sQuery(id+"F1.wireOp",EDGE,"E3"),subQ6,sQuery(id+"F1.wireOp",EDGE,"E5"),sQuery(id+"F1.wireOp",EDGE,"E6"),sQuery(id+"F1.wireOp",EDGE,"E7"),sQuery(id+"F1.wireOp",EDGE,"E8"),sQuery(id+"F1.wireOp",EDGE,"E9"),sQuery(id+"F1.wireOp",EDGE,"E10"),subQ3,subQ5,subQ2,sQuery(id+"F1.wireOp",EDGE,"E14"),sQuery(id+"F1.wireOp",EDGE,"E15"),sQuery(id+"F1.wireOp",EDGE,"E16"),sQuery(id+"F1.wireOp",EDGE,"E17"),sQuery(id+"F1.wireOp",EDGE,"E18.trimOffspring"),sQuery(id+"F1.wireOp",EDGE,"E19"),sQuery(id+"F1.wireOp",EDGE,"E20"),sQuery(id+"F1.wireOp",EDGE,"E21"),sQuery(id+"F1.wireOp",EDGE,"E22"),sQuery(id+"F1.wireOp",EDGE,"E23"),sQuery(id+"F1.wireOp",EDGE,"E24"),sQuery(id+"F1.wireOp",EDGE,"E25"),sQuery(id+"F1.wireOp",EDGE,"E26"),sQuery(id+"F1.wireOp",EDGE,"E27"),sQuery(id+"F1.wireOp",EDGE,"E28"),sQuery(id+"F1.wireOp",EDGE,"E29")])],"isStart":false});Q11=makeQuery(id+"F35.opBoolean","SPLIT",FACE,{"disambiguationData":[TD([makeQuery(id+"F12.opPattern","COPY",FACE,{"derivedFrom":makeQuery(id+"F2.opExtrude","SWEPT_FACE",FACE,{"disambiguationData":[OSD([subQ2])]}),"instanceName":"2"})])],"derivedFrom":makeQuery(id+"F12.opPattern","COPY",FACE,{"derivedFrom":makeQuery(id+"F4.boolean.opBoolean","MERGE",FACE,{"derivedFrom":[subQ8,makeQuery(id+"F4.opPattern","COPY",FACE,{"derivedFrom":subQ8,"instanceName":"1"})]}),"instanceName":"2"})});}
            var Q12;
            {var subQ0=sQuery(id+"F5.wireOp",EDGE,"E53");Q12=makeQuery(id+"F12.opPattern","COPY",FACE,{"derivedFrom":makeQuery(id+"F8.boolean.opBoolean","MERGE",FACE,{"derivedFrom":[makeQuery(id+"F6.boolean.opBoolean","COPY",FACE,{"derivedFrom":makeQuery(id+"F6.opExtrude","CAP_FACE",FACE,{"disambiguationData":[OSD([sQuery(id+"F5.wireOp",EDGE,"E30"),sQuery(id+"F5.wireOp",EDGE,"E32"),sQuery(id+"F5.wireOp",EDGE,"E33"),sQuery(id+"F5.wireOp",EDGE,"E34"),sQuery(id+"F5.wireOp",EDGE,"E35"),sQuery(id+"F5.wireOp",EDGE,"E36"),sQuery(id+"F5.wireOp",EDGE,"E37"),sQuery(id+"F5.wireOp",EDGE,"E38.trimOffspring"),sQuery(id+"F5.wireOp",EDGE,"E39"),sQuery(id+"F5.wireOp",EDGE,"E40"),sQuery(id+"F5.wireOp",EDGE,"E41"),sQuery(id+"F5.wireOp",EDGE,"E42"),sQuery(id+"F5.wireOp",EDGE,"E43"),sQuery(id+"F5.wireOp",EDGE,"E44"),sQuery(id+"F5.wireOp",EDGE,"E45"),sQuery(id+"F5.wireOp",EDGE,"E46"),sQuery(id+"F5.wireOp",EDGE,"E47"),subQ0,sQuery(id+"F5.wireOp",EDGE,"E54")])],"isStart":false})}),makeQuery(id+"F8.opExtrude","CAP_FACE",FACE,{"disambiguationData":[OSD([subQ0,sQuery(id+"F7.wireOp",EDGE,"E55"),sQuery(id+"F7.wireOp",EDGE,"E56"),sQuery(id+"F7.wireOp",EDGE,"E57"),sQuery(id+"F7.wireOp",EDGE,"E58.right"),sQuery(id+"F7.wireOp",EDGE,"E62"),sQuery(id+"F7.wireOp",EDGE,"E65"),sQuery(id+"F7.wireOp",EDGE,"E66"),sQuery(id+"F7.wireOp",EDGE,"E67"),sQuery(id+"F7.wireOp",EDGE,"E68"),sQuery(id+"F7.wireOp",EDGE,"E69"),sQuery(id+"F7.wireOp",EDGE,"E70"),sQuery(id+"F7.wireOp",EDGE,"E72"),sQuery(id+"F7.wireOp",EDGE,"E74"),sQuery(id+"F7.wireOp",EDGE,"E75"),sQuery(id+"F7.wireOp",EDGE,"E76.trimOffspring")])],"isStart":false})]}),"instanceName":"1"});}
            var Q13;
            Q13=makeQuery(id+"F12.opPattern","COPY",FACE,{"derivedFrom":makeQuery(id+"F6.boolean.opBoolean","COPY",FACE,{"derivedFrom":makeQuery(id+"F6.opExtrude","CAP_FACE",FACE,{"disambiguationData":[OSD([sQuery(id+"F5.wireOp",EDGE,"E48"),sQuery(id+"F5.wireOp",EDGE,"E49"),sQuery(id+"F5.wireOp",EDGE,"E50"),sQuery(id+"F5.wireOp",EDGE,"E51"),sQuery(id+"F5.wireOp",EDGE,"E52")])],"isStart":false})}),"instanceName":"1"});
            var Q14;
            Q14=makeQuery(id+"F12.opPattern","COPY",FACE,{"derivedFrom":makeQuery(id+"F8.boolean.opBoolean","COPY",FACE,{"derivedFrom":makeQuery(id+"F8.opExtrude","CAP_FACE",FACE,{"disambiguationData":[OSD([sQuery(id+"F7.wireOp",EDGE,"E77"),sQuery(id+"F7.wireOp",EDGE,"E78"),sQuery(id+"F7.wireOp",EDGE,"E79"),sQuery(id+"F7.wireOp",EDGE,"E80")])],"isStart":false})}),"instanceName":"1"});
            var Q15;
            {var subQ2=sQuery(id+"F1.wireOp",EDGE,"E13");var subQ3=sQuery(id+"F1.wireOp",EDGE,"E12");var subQ5=sQuery(id+"F1.wireOp",EDGE,"E11");var subQ6=sQuery(id+"F1.wireOp",EDGE,"E4");var subQ7=sQuery(id+"F1.wireOp",EDGE,"E2");var subQ8=makeQuery(id+"F2.opExtrude","CAP_FACE",FACE,{"disambiguationData":[OSD([sQuery(id+"F1.wireOp",EDGE,"E1"),subQ7,sQuery(id+"F1.wireOp",EDGE,"E3"),subQ6,sQuery(id+"F1.wireOp",EDGE,"E5"),sQuery(id+"F1.wireOp",EDGE,"E6"),sQuery(id+"F1.wireOp",EDGE,"E7"),sQuery(id+"F1.wireOp",EDGE,"E8"),sQuery(id+"F1.wireOp",EDGE,"E9"),sQuery(id+"F1.wireOp",EDGE,"E10"),subQ5,subQ3,subQ2,sQuery(id+"F1.wireOp",EDGE,"E14"),sQuery(id+"F1.wireOp",EDGE,"E15"),sQuery(id+"F1.wireOp",EDGE,"E16"),sQuery(id+"F1.wireOp",EDGE,"E17"),sQuery(id+"F1.wireOp",EDGE,"E18.trimOffspring"),sQuery(id+"F1.wireOp",EDGE,"E19"),sQuery(id+"F1.wireOp",EDGE,"E20"),sQuery(id+"F1.wireOp",EDGE,"E21"),sQuery(id+"F1.wireOp",EDGE,"E22"),sQuery(id+"F1.wireOp",EDGE,"E23"),sQuery(id+"F1.wireOp",EDGE,"E24"),sQuery(id+"F1.wireOp",EDGE,"E25"),sQuery(id+"F1.wireOp",EDGE,"E26"),sQuery(id+"F1.wireOp",EDGE,"E27"),sQuery(id+"F1.wireOp",EDGE,"E28"),sQuery(id+"F1.wireOp",EDGE,"E29")])],"isStart":false});Q15=makeQuery(id+"F35.opBoolean","SPLIT",FACE,{"disambiguationData":[TD([makeQuery(id+"F12.opPattern","COPY",FACE,{"derivedFrom":makeQuery(id+"F4.opPattern","COPY",FACE,{"derivedFrom":makeQuery(id+"F2.opExtrude","SWEPT_FACE",FACE,{"disambiguationData":[OSD([subQ2])]}),"instanceName":"1"}),"instanceName":"1"})])],"derivedFrom":makeQuery(id+"F12.opPattern","COPY",FACE,{"derivedFrom":makeQuery(id+"F4.boolean.opBoolean","MERGE",FACE,{"derivedFrom":[subQ8,makeQuery(id+"F4.opPattern","COPY",FACE,{"derivedFrom":subQ8,"instanceName":"1"})]}),"instanceName":"1"})});}
            var Q16;
            {var subQ0=sQuery(id+"F1.wireOp",EDGE,"E16");var subQ1=sQuery(id+"F1.wireOp",EDGE,"E8");var subQ3=sQuery(id+"F1.wireOp",EDGE,"E14");var subQ4=sQuery(id+"F1.wireOp",EDGE,"E7");var subQ6=sQuery(id+"F1.wireOp",EDGE,"E17");var subQ8=sQuery(id+"F1.wireOp",EDGE,"E15");var subQ10=sQuery(id+"F1.wireOp",EDGE,"E29");var subQ12=sQuery(id+"F1.wireOp",EDGE,"E28");var subQ14=sQuery(id+"F1.wireOp",EDGE,"E27");var subQ16=sQuery(id+"F1.wireOp",EDGE,"E26");var subQ18=sQuery(id+"F1.wireOp",EDGE,"E25");var subQ20=sQuery(id+"F1.wireOp",EDGE,"E24");var subQ22=sQuery(id+"F1.wireOp",EDGE,"E23");var subQ24=sQuery(id+"F1.wireOp",EDGE,"E22");var subQ26=sQuery(id+"F1.wireOp",EDGE,"E21");var subQ28=sQuery(id+"F1.wireOp",EDGE,"E19");var subQ30=sQuery(id+"F1.wireOp",EDGE,"E18.trimOffspring");var subQ32=sQuery(id+"F1.wireOp",EDGE,"E10");var subQ34=sQuery(id+"F1.wireOp",EDGE,"E6");var subQ35=makeQuery(id+"F2.opExtrude","SWEPT_FACE",FACE,{"disambiguationData":[OSD([subQ34])]});var subQ38=sQuery(id+"F1.wireOp",EDGE,"E9");var subQ45=makeQuery(id+"F2.opExtrude","CAP_FACE",FACE,{"disambiguationData":[OSD([sQuery(id+"F1.wireOp",EDGE,"E1"),sQuery(id+"F1.wireOp",EDGE,"E2"),sQuery(id+"F1.wireOp",EDGE,"E3"),sQuery(id+"F1.wireOp",EDGE,"E4"),sQuery(id+"F1.wireOp",EDGE,"E5"),subQ34,subQ4,subQ1,subQ38,subQ32,sQuery(id+"F1.wireOp",EDGE,"E11"),sQuery(id+"F1.wireOp",EDGE,"E12"),sQuery(id+"F1.wireOp",EDGE,"E13"),subQ3,subQ8,subQ0,subQ6,subQ30,subQ28,sQuery(id+"F1.wireOp",EDGE,"E20"),subQ26,subQ24,subQ22,subQ20,subQ18,subQ16,subQ14,subQ12,subQ10])],"isStart":false});Q16=makeQuery(id+"F35.opBoolean","SPLIT",FACE,{"disambiguationData":[TD([makeQuery(id+"F12.opPattern","COPY",FACE,{"derivedFrom":subQ35,"instanceName":"1"})])],"derivedFrom":makeQuery(id+"F12.opPattern","COPY",FACE,{"derivedFrom":makeQuery(id+"F4.boolean.opBoolean","MERGE",FACE,{"derivedFrom":[subQ45,makeQuery(id+"F4.opPattern","COPY",FACE,{"derivedFrom":subQ45,"instanceName":"1"})]}),"instanceName":"1"})});}
            var Q17;
            {var subQ2=sQuery(id+"F1.wireOp",EDGE,"E13");var subQ3=sQuery(id+"F1.wireOp",EDGE,"E11");var subQ5=sQuery(id+"F1.wireOp",EDGE,"E12");var subQ6=sQuery(id+"F1.wireOp",EDGE,"E4");var subQ7=sQuery(id+"F1.wireOp",EDGE,"E2");var subQ8=makeQuery(id+"F2.opExtrude","CAP_FACE",FACE,{"disambiguationData":[OSD([sQuery(id+"F1.wireOp",EDGE,"E1"),subQ7,sQuery(id+"F1.wireOp",EDGE,"E3"),subQ6,sQuery(id+"F1.wireOp",EDGE,"E5"),sQuery(id+"F1.wireOp",EDGE,"E6"),sQuery(id+"F1.wireOp",EDGE,"E7"),sQuery(id+"F1.wireOp",EDGE,"E8"),sQuery(id+"F1.wireOp",EDGE,"E9"),sQuery(id+"F1.wireOp",EDGE,"E10"),subQ3,subQ5,subQ2,sQuery(id+"F1.wireOp",EDGE,"E14"),sQuery(id+"F1.wireOp",EDGE,"E15"),sQuery(id+"F1.wireOp",EDGE,"E16"),sQuery(id+"F1.wireOp",EDGE,"E17"),sQuery(id+"F1.wireOp",EDGE,"E18.trimOffspring"),sQuery(id+"F1.wireOp",EDGE,"E19"),sQuery(id+"F1.wireOp",EDGE,"E20"),sQuery(id+"F1.wireOp",EDGE,"E21"),sQuery(id+"F1.wireOp",EDGE,"E22"),sQuery(id+"F1.wireOp",EDGE,"E23"),sQuery(id+"F1.wireOp",EDGE,"E24"),sQuery(id+"F1.wireOp",EDGE,"E25"),sQuery(id+"F1.wireOp",EDGE,"E26"),sQuery(id+"F1.wireOp",EDGE,"E27"),sQuery(id+"F1.wireOp",EDGE,"E28"),sQuery(id+"F1.wireOp",EDGE,"E29")])],"isStart":false});Q17=makeQuery(id+"F35.opBoolean","SPLIT",FACE,{"disambiguationData":[TD([makeQuery(id+"F12.opPattern","COPY",FACE,{"derivedFrom":makeQuery(id+"F2.opExtrude","SWEPT_FACE",FACE,{"disambiguationData":[OSD([subQ2])]}),"instanceName":"1"})])],"derivedFrom":makeQuery(id+"F12.opPattern","COPY",FACE,{"derivedFrom":makeQuery(id+"F4.boolean.opBoolean","MERGE",FACE,{"derivedFrom":[subQ8,makeQuery(id+"F4.opPattern","COPY",FACE,{"derivedFrom":subQ8,"instanceName":"1"})]}),"instanceName":"1"})});}
            var Q18;
            {var subQ0=sQuery(id+"F5.wireOp",EDGE,"E53");Q18=makeQuery(id+"F8.boolean.opBoolean","MERGE",FACE,{"derivedFrom":[makeQuery(id+"F6.boolean.opBoolean","COPY",FACE,{"derivedFrom":makeQuery(id+"F6.opExtrude","CAP_FACE",FACE,{"disambiguationData":[OSD([sQuery(id+"F5.wireOp",EDGE,"E30"),sQuery(id+"F5.wireOp",EDGE,"E32"),sQuery(id+"F5.wireOp",EDGE,"E33"),sQuery(id+"F5.wireOp",EDGE,"E34"),sQuery(id+"F5.wireOp",EDGE,"E35"),sQuery(id+"F5.wireOp",EDGE,"E36"),sQuery(id+"F5.wireOp",EDGE,"E37"),sQuery(id+"F5.wireOp",EDGE,"E38.trimOffspring"),sQuery(id+"F5.wireOp",EDGE,"E39"),sQuery(id+"F5.wireOp",EDGE,"E40"),sQuery(id+"F5.wireOp",EDGE,"E41"),sQuery(id+"F5.wireOp",EDGE,"E42"),sQuery(id+"F5.wireOp",EDGE,"E43"),sQuery(id+"F5.wireOp",EDGE,"E44"),sQuery(id+"F5.wireOp",EDGE,"E45"),sQuery(id+"F5.wireOp",EDGE,"E46"),sQuery(id+"F5.wireOp",EDGE,"E47"),subQ0,sQuery(id+"F5.wireOp",EDGE,"E54")])],"isStart":false})}),makeQuery(id+"F8.opExtrude","CAP_FACE",FACE,{"disambiguationData":[OSD([subQ0,sQuery(id+"F7.wireOp",EDGE,"E55"),sQuery(id+"F7.wireOp",EDGE,"E56"),sQuery(id+"F7.wireOp",EDGE,"E57"),sQuery(id+"F7.wireOp",EDGE,"E58.right"),sQuery(id+"F7.wireOp",EDGE,"E62"),sQuery(id+"F7.wireOp",EDGE,"E65"),sQuery(id+"F7.wireOp",EDGE,"E66"),sQuery(id+"F7.wireOp",EDGE,"E67"),sQuery(id+"F7.wireOp",EDGE,"E68"),sQuery(id+"F7.wireOp",EDGE,"E69"),sQuery(id+"F7.wireOp",EDGE,"E70"),sQuery(id+"F7.wireOp",EDGE,"E72"),sQuery(id+"F7.wireOp",EDGE,"E74"),sQuery(id+"F7.wireOp",EDGE,"E75"),sQuery(id+"F7.wireOp",EDGE,"E76.trimOffspring")])],"isStart":false})]});}
            var Q19;
            {var subQ3=sQuery(id+"F1.wireOp",EDGE,"E17");var subQ4=sQuery(id+"F1.wireOp",EDGE,"E15");var subQ6=sQuery(id+"F1.wireOp",EDGE,"E16");var subQ7=sQuery(id+"F1.wireOp",EDGE,"E8");var subQ9=sQuery(id+"F1.wireOp",EDGE,"E22");var subQ11=sQuery(id+"F1.wireOp",EDGE,"E26");var subQ13=sQuery(id+"F1.wireOp",EDGE,"E27");var subQ15=sQuery(id+"F1.wireOp",EDGE,"E10");var subQ17=sQuery(id+"F1.wireOp",EDGE,"E21");var subQ19=sQuery(id+"F1.wireOp",EDGE,"E9");var subQ21=sQuery(id+"F1.wireOp",EDGE,"E25");var subQ23=sQuery(id+"F1.wireOp",EDGE,"E29");var subQ25=sQuery(id+"F1.wireOp",EDGE,"E19");var subQ27=sQuery(id+"F1.wireOp",EDGE,"E6");var subQ28=makeQuery(id+"F2.opExtrude","SWEPT_FACE",FACE,{"disambiguationData":[OSD([subQ27])]});var subQ29=sQuery(id+"F1.wireOp",EDGE,"E24");var subQ31=sQuery(id+"F1.wireOp",EDGE,"E28");var subQ33=sQuery(id+"F1.wireOp",EDGE,"E18.trimOffspring");var subQ35=sQuery(id+"F1.wireOp",EDGE,"E23");var subQ37=sQuery(id+"F1.wireOp",EDGE,"E14");var subQ39=sQuery(id+"F1.wireOp",EDGE,"E7");var subQ45=makeQuery(id+"F2.opExtrude","CAP_FACE",FACE,{"disambiguationData":[OSD([sQuery(id+"F1.wireOp",EDGE,"E1"),sQuery(id+"F1.wireOp",EDGE,"E2"),sQuery(id+"F1.wireOp",EDGE,"E3"),sQuery(id+"F1.wireOp",EDGE,"E4"),sQuery(id+"F1.wireOp",EDGE,"E5"),subQ27,subQ39,subQ7,subQ19,subQ15,sQuery(id+"F1.wireOp",EDGE,"E11"),sQuery(id+"F1.wireOp",EDGE,"E12"),sQuery(id+"F1.wireOp",EDGE,"E13"),subQ37,subQ4,subQ6,subQ3,subQ33,subQ25,sQuery(id+"F1.wireOp",EDGE,"E20"),subQ17,subQ9,subQ35,subQ29,subQ21,subQ11,subQ13,subQ31,subQ23])],"isStart":false});Q19=makeQuery(id+"F35.opBoolean","SPLIT",FACE,{"disambiguationData":[TD([subQ28])],"derivedFrom":makeQuery(id+"F4.boolean.opBoolean","MERGE",FACE,{"derivedFrom":[subQ45,makeQuery(id+"F4.opPattern","COPY",FACE,{"derivedFrom":subQ45,"instanceName":"1"})]})});}
            var Q20;
            {var subQ3=sQuery(id+"F1.wireOp",EDGE,"E13");var subQ4=sQuery(id+"F1.wireOp",EDGE,"E11");var subQ5=sQuery(id+"F1.wireOp",EDGE,"E12");var subQ6=sQuery(id+"F1.wireOp",EDGE,"E2");var subQ7=sQuery(id+"F1.wireOp",EDGE,"E4");var subQ8=makeQuery(id+"F2.opExtrude","CAP_FACE",FACE,{"disambiguationData":[OSD([sQuery(id+"F1.wireOp",EDGE,"E1"),subQ6,sQuery(id+"F1.wireOp",EDGE,"E3"),subQ7,sQuery(id+"F1.wireOp",EDGE,"E5"),sQuery(id+"F1.wireOp",EDGE,"E6"),sQuery(id+"F1.wireOp",EDGE,"E7"),sQuery(id+"F1.wireOp",EDGE,"E8"),sQuery(id+"F1.wireOp",EDGE,"E9"),sQuery(id+"F1.wireOp",EDGE,"E10"),subQ4,subQ5,subQ3,sQuery(id+"F1.wireOp",EDGE,"E14"),sQuery(id+"F1.wireOp",EDGE,"E15"),sQuery(id+"F1.wireOp",EDGE,"E16"),sQuery(id+"F1.wireOp",EDGE,"E17"),sQuery(id+"F1.wireOp",EDGE,"E18.trimOffspring"),sQuery(id+"F1.wireOp",EDGE,"E19"),sQuery(id+"F1.wireOp",EDGE,"E20"),sQuery(id+"F1.wireOp",EDGE,"E21"),sQuery(id+"F1.wireOp",EDGE,"E22"),sQuery(id+"F1.wireOp",EDGE,"E23"),sQuery(id+"F1.wireOp",EDGE,"E24"),sQuery(id+"F1.wireOp",EDGE,"E25"),sQuery(id+"F1.wireOp",EDGE,"E26"),sQuery(id+"F1.wireOp",EDGE,"E27"),sQuery(id+"F1.wireOp",EDGE,"E28"),sQuery(id+"F1.wireOp",EDGE,"E29")])],"isStart":false});Q20=makeQuery(id+"F35.opBoolean","SPLIT",FACE,{"disambiguationData":[TD([makeQuery(id+"F4.opPattern","COPY",FACE,{"derivedFrom":makeQuery(id+"F2.opExtrude","SWEPT_FACE",FACE,{"disambiguationData":[OSD([subQ3])]}),"instanceName":"1"})])],"derivedFrom":makeQuery(id+"F4.boolean.opBoolean","MERGE",FACE,{"derivedFrom":[subQ8,makeQuery(id+"F4.opPattern","COPY",FACE,{"derivedFrom":subQ8,"instanceName":"1"})]})});}
            var Q21;
            Q21=makeQuery(id+"F8.boolean.opBoolean","COPY",FACE,{"derivedFrom":makeQuery(id+"F8.opExtrude","CAP_FACE",FACE,{"disambiguationData":[OSD([sQuery(id+"F7.wireOp",EDGE,"E77"),sQuery(id+"F7.wireOp",EDGE,"E78"),sQuery(id+"F7.wireOp",EDGE,"E79"),sQuery(id+"F7.wireOp",EDGE,"E80")])],"isStart":false})});
            var Q22;
            Q22=makeQuery(id+"F6.boolean.opBoolean","COPY",FACE,{"derivedFrom":makeQuery(id+"F6.opExtrude","CAP_FACE",FACE,{"disambiguationData":[OSD([sQuery(id+"F5.wireOp",EDGE,"E48"),sQuery(id+"F5.wireOp",EDGE,"E49"),sQuery(id+"F5.wireOp",EDGE,"E50"),sQuery(id+"F5.wireOp",EDGE,"E51"),sQuery(id+"F5.wireOp",EDGE,"E52")])],"isStart":false})});
            var Q23;
            {var subQ3=sQuery(id+"F1.wireOp",EDGE,"E11");var subQ4=sQuery(id+"F1.wireOp",EDGE,"E2");var subQ5=sQuery(id+"F1.wireOp",EDGE,"E13");var subQ6=sQuery(id+"F1.wireOp",EDGE,"E12");var subQ7=sQuery(id+"F1.wireOp",EDGE,"E4");var subQ8=makeQuery(id+"F2.opExtrude","CAP_FACE",FACE,{"disambiguationData":[OSD([sQuery(id+"F1.wireOp",EDGE,"E1"),subQ4,sQuery(id+"F1.wireOp",EDGE,"E3"),subQ7,sQuery(id+"F1.wireOp",EDGE,"E5"),sQuery(id+"F1.wireOp",EDGE,"E6"),sQuery(id+"F1.wireOp",EDGE,"E7"),sQuery(id+"F1.wireOp",EDGE,"E8"),sQuery(id+"F1.wireOp",EDGE,"E9"),sQuery(id+"F1.wireOp",EDGE,"E10"),subQ3,subQ6,subQ5,sQuery(id+"F1.wireOp",EDGE,"E14"),sQuery(id+"F1.wireOp",EDGE,"E15"),sQuery(id+"F1.wireOp",EDGE,"E16"),sQuery(id+"F1.wireOp",EDGE,"E17"),sQuery(id+"F1.wireOp",EDGE,"E18.trimOffspring"),sQuery(id+"F1.wireOp",EDGE,"E19"),sQuery(id+"F1.wireOp",EDGE,"E20"),sQuery(id+"F1.wireOp",EDGE,"E21"),sQuery(id+"F1.wireOp",EDGE,"E22"),sQuery(id+"F1.wireOp",EDGE,"E23"),sQuery(id+"F1.wireOp",EDGE,"E24"),sQuery(id+"F1.wireOp",EDGE,"E25"),sQuery(id+"F1.wireOp",EDGE,"E26"),sQuery(id+"F1.wireOp",EDGE,"E27"),sQuery(id+"F1.wireOp",EDGE,"E28"),sQuery(id+"F1.wireOp",EDGE,"E29")])],"isStart":false});Q23=makeQuery(id+"F35.opBoolean","SPLIT",FACE,{"disambiguationData":[TD([makeQuery(id+"F2.opExtrude","SWEPT_FACE",FACE,{"disambiguationData":[OSD([subQ5])]})])],"derivedFrom":makeQuery(id+"F4.boolean.opBoolean","MERGE",FACE,{"derivedFrom":[subQ8,makeQuery(id+"F4.opPattern","COPY",FACE,{"derivedFrom":subQ8,"instanceName":"1"})]})});}
            var Q24;
            {var subQ0=sQuery(id+"F5.wireOp",EDGE,"E53");Q24=makeQuery(id+"F12.opPattern","COPY",FACE,{"derivedFrom":makeQuery(id+"F8.boolean.opBoolean","MERGE",FACE,{"derivedFrom":[makeQuery(id+"F6.boolean.opBoolean","COPY",FACE,{"derivedFrom":makeQuery(id+"F6.opExtrude","CAP_FACE",FACE,{"disambiguationData":[OSD([sQuery(id+"F5.wireOp",EDGE,"E30"),sQuery(id+"F5.wireOp",EDGE,"E32"),sQuery(id+"F5.wireOp",EDGE,"E33"),sQuery(id+"F5.wireOp",EDGE,"E34"),sQuery(id+"F5.wireOp",EDGE,"E35"),sQuery(id+"F5.wireOp",EDGE,"E36"),sQuery(id+"F5.wireOp",EDGE,"E37"),sQuery(id+"F5.wireOp",EDGE,"E38.trimOffspring"),sQuery(id+"F5.wireOp",EDGE,"E39"),sQuery(id+"F5.wireOp",EDGE,"E40"),sQuery(id+"F5.wireOp",EDGE,"E41"),sQuery(id+"F5.wireOp",EDGE,"E42"),sQuery(id+"F5.wireOp",EDGE,"E43"),sQuery(id+"F5.wireOp",EDGE,"E44"),sQuery(id+"F5.wireOp",EDGE,"E45"),sQuery(id+"F5.wireOp",EDGE,"E46"),sQuery(id+"F5.wireOp",EDGE,"E47"),subQ0,sQuery(id+"F5.wireOp",EDGE,"E54")])],"isStart":false})}),makeQuery(id+"F8.opExtrude","CAP_FACE",FACE,{"disambiguationData":[OSD([subQ0,sQuery(id+"F7.wireOp",EDGE,"E55"),sQuery(id+"F7.wireOp",EDGE,"E56"),sQuery(id+"F7.wireOp",EDGE,"E57"),sQuery(id+"F7.wireOp",EDGE,"E58.right"),sQuery(id+"F7.wireOp",EDGE,"E62"),sQuery(id+"F7.wireOp",EDGE,"E65"),sQuery(id+"F7.wireOp",EDGE,"E66"),sQuery(id+"F7.wireOp",EDGE,"E67"),sQuery(id+"F7.wireOp",EDGE,"E68"),sQuery(id+"F7.wireOp",EDGE,"E69"),sQuery(id+"F7.wireOp",EDGE,"E70"),sQuery(id+"F7.wireOp",EDGE,"E72"),sQuery(id+"F7.wireOp",EDGE,"E74"),sQuery(id+"F7.wireOp",EDGE,"E75"),sQuery(id+"F7.wireOp",EDGE,"E76.trimOffspring")])],"isStart":false})]}),"instanceName":"5"});}
            var Q25;
            Q25=makeQuery(id+"F12.opPattern","COPY",FACE,{"derivedFrom":makeQuery(id+"F8.boolean.opBoolean","COPY",FACE,{"derivedFrom":makeQuery(id+"F8.opExtrude","CAP_FACE",FACE,{"disambiguationData":[OSD([sQuery(id+"F7.wireOp",EDGE,"E77"),sQuery(id+"F7.wireOp",EDGE,"E78"),sQuery(id+"F7.wireOp",EDGE,"E79"),sQuery(id+"F7.wireOp",EDGE,"E80")])],"isStart":false})}),"instanceName":"5"});
            var Q26;
            {var subQ2=sQuery(id+"F1.wireOp",EDGE,"E13");var subQ3=sQuery(id+"F1.wireOp",EDGE,"E12");var subQ5=sQuery(id+"F1.wireOp",EDGE,"E11");var subQ6=sQuery(id+"F1.wireOp",EDGE,"E4");var subQ7=sQuery(id+"F1.wireOp",EDGE,"E2");var subQ8=makeQuery(id+"F2.opExtrude","CAP_FACE",FACE,{"disambiguationData":[OSD([sQuery(id+"F1.wireOp",EDGE,"E1"),subQ7,sQuery(id+"F1.wireOp",EDGE,"E3"),subQ6,sQuery(id+"F1.wireOp",EDGE,"E5"),sQuery(id+"F1.wireOp",EDGE,"E6"),sQuery(id+"F1.wireOp",EDGE,"E7"),sQuery(id+"F1.wireOp",EDGE,"E8"),sQuery(id+"F1.wireOp",EDGE,"E9"),sQuery(id+"F1.wireOp",EDGE,"E10"),subQ5,subQ3,subQ2,sQuery(id+"F1.wireOp",EDGE,"E14"),sQuery(id+"F1.wireOp",EDGE,"E15"),sQuery(id+"F1.wireOp",EDGE,"E16"),sQuery(id+"F1.wireOp",EDGE,"E17"),sQuery(id+"F1.wireOp",EDGE,"E18.trimOffspring"),sQuery(id+"F1.wireOp",EDGE,"E19"),sQuery(id+"F1.wireOp",EDGE,"E20"),sQuery(id+"F1.wireOp",EDGE,"E21"),sQuery(id+"F1.wireOp",EDGE,"E22"),sQuery(id+"F1.wireOp",EDGE,"E23"),sQuery(id+"F1.wireOp",EDGE,"E24"),sQuery(id+"F1.wireOp",EDGE,"E25"),sQuery(id+"F1.wireOp",EDGE,"E26"),sQuery(id+"F1.wireOp",EDGE,"E27"),sQuery(id+"F1.wireOp",EDGE,"E28"),sQuery(id+"F1.wireOp",EDGE,"E29")])],"isStart":false});Q26=makeQuery(id+"F35.opBoolean","SPLIT",FACE,{"disambiguationData":[TD([makeQuery(id+"F12.opPattern","COPY",FACE,{"derivedFrom":makeQuery(id+"F4.opPattern","COPY",FACE,{"derivedFrom":makeQuery(id+"F2.opExtrude","SWEPT_FACE",FACE,{"disambiguationData":[OSD([subQ2])]}),"instanceName":"1"}),"instanceName":"5"})])],"derivedFrom":makeQuery(id+"F12.opPattern","COPY",FACE,{"derivedFrom":makeQuery(id+"F4.boolean.opBoolean","MERGE",FACE,{"derivedFrom":[subQ8,makeQuery(id+"F4.opPattern","COPY",FACE,{"derivedFrom":subQ8,"instanceName":"1"})]}),"instanceName":"5"})});}
            var Q27;
            {var subQ0=sQuery(id+"F1.wireOp",EDGE,"E16");var subQ1=sQuery(id+"F1.wireOp",EDGE,"E8");var subQ3=sQuery(id+"F1.wireOp",EDGE,"E14");var subQ4=sQuery(id+"F1.wireOp",EDGE,"E7");var subQ6=sQuery(id+"F1.wireOp",EDGE,"E17");var subQ8=sQuery(id+"F1.wireOp",EDGE,"E15");var subQ10=sQuery(id+"F1.wireOp",EDGE,"E29");var subQ12=sQuery(id+"F1.wireOp",EDGE,"E28");var subQ14=sQuery(id+"F1.wireOp",EDGE,"E27");var subQ16=sQuery(id+"F1.wireOp",EDGE,"E26");var subQ18=sQuery(id+"F1.wireOp",EDGE,"E25");var subQ20=sQuery(id+"F1.wireOp",EDGE,"E24");var subQ22=sQuery(id+"F1.wireOp",EDGE,"E23");var subQ24=sQuery(id+"F1.wireOp",EDGE,"E22");var subQ26=sQuery(id+"F1.wireOp",EDGE,"E21");var subQ28=sQuery(id+"F1.wireOp",EDGE,"E19");var subQ30=sQuery(id+"F1.wireOp",EDGE,"E18.trimOffspring");var subQ32=sQuery(id+"F1.wireOp",EDGE,"E10");var subQ34=sQuery(id+"F1.wireOp",EDGE,"E6");var subQ37=sQuery(id+"F1.wireOp",EDGE,"E9");var subQ44=makeQuery(id+"F2.opExtrude","CAP_FACE",FACE,{"disambiguationData":[OSD([sQuery(id+"F1.wireOp",EDGE,"E1"),sQuery(id+"F1.wireOp",EDGE,"E2"),sQuery(id+"F1.wireOp",EDGE,"E3"),sQuery(id+"F1.wireOp",EDGE,"E4"),sQuery(id+"F1.wireOp",EDGE,"E5"),subQ34,subQ4,subQ1,subQ37,subQ32,sQuery(id+"F1.wireOp",EDGE,"E11"),sQuery(id+"F1.wireOp",EDGE,"E12"),sQuery(id+"F1.wireOp",EDGE,"E13"),subQ3,subQ8,subQ0,subQ6,subQ30,subQ28,sQuery(id+"F1.wireOp",EDGE,"E20"),subQ26,subQ24,subQ22,subQ20,subQ18,subQ16,subQ14,subQ12,subQ10])],"isStart":false});Q27=makeQuery(id+"F35.opBoolean","SPLIT",FACE,{"disambiguationData":[TD([makeQuery(id+"F12.opPattern","COPY",FACE,{"derivedFrom":makeQuery(id+"F2.opExtrude","SWEPT_FACE",FACE,{"disambiguationData":[OSD([subQ34])]}),"instanceName":"5"})])],"derivedFrom":makeQuery(id+"F12.opPattern","COPY",FACE,{"derivedFrom":makeQuery(id+"F4.boolean.opBoolean","MERGE",FACE,{"derivedFrom":[subQ44,makeQuery(id+"F4.opPattern","COPY",FACE,{"derivedFrom":subQ44,"instanceName":"1"})]}),"instanceName":"5"})});}
            var Q28;
            Q28=makeQuery(id+"F12.opPattern","COPY",FACE,{"derivedFrom":makeQuery(id+"F6.boolean.opBoolean","COPY",FACE,{"derivedFrom":makeQuery(id+"F6.opExtrude","CAP_FACE",FACE,{"disambiguationData":[OSD([sQuery(id+"F5.wireOp",EDGE,"E48"),sQuery(id+"F5.wireOp",EDGE,"E49"),sQuery(id+"F5.wireOp",EDGE,"E50"),sQuery(id+"F5.wireOp",EDGE,"E51"),sQuery(id+"F5.wireOp",EDGE,"E52")])],"isStart":false})}),"instanceName":"5"});
            var Q29;
            {var subQ2=sQuery(id+"F1.wireOp",EDGE,"E13");var subQ3=sQuery(id+"F1.wireOp",EDGE,"E11");var subQ5=sQuery(id+"F1.wireOp",EDGE,"E12");var subQ6=sQuery(id+"F1.wireOp",EDGE,"E4");var subQ7=sQuery(id+"F1.wireOp",EDGE,"E2");var subQ8=makeQuery(id+"F2.opExtrude","CAP_FACE",FACE,{"disambiguationData":[OSD([sQuery(id+"F1.wireOp",EDGE,"E1"),subQ7,sQuery(id+"F1.wireOp",EDGE,"E3"),subQ6,sQuery(id+"F1.wireOp",EDGE,"E5"),sQuery(id+"F1.wireOp",EDGE,"E6"),sQuery(id+"F1.wireOp",EDGE,"E7"),sQuery(id+"F1.wireOp",EDGE,"E8"),sQuery(id+"F1.wireOp",EDGE,"E9"),sQuery(id+"F1.wireOp",EDGE,"E10"),subQ3,subQ5,subQ2,sQuery(id+"F1.wireOp",EDGE,"E14"),sQuery(id+"F1.wireOp",EDGE,"E15"),sQuery(id+"F1.wireOp",EDGE,"E16"),sQuery(id+"F1.wireOp",EDGE,"E17"),sQuery(id+"F1.wireOp",EDGE,"E18.trimOffspring"),sQuery(id+"F1.wireOp",EDGE,"E19"),sQuery(id+"F1.wireOp",EDGE,"E20"),sQuery(id+"F1.wireOp",EDGE,"E21"),sQuery(id+"F1.wireOp",EDGE,"E22"),sQuery(id+"F1.wireOp",EDGE,"E23"),sQuery(id+"F1.wireOp",EDGE,"E24"),sQuery(id+"F1.wireOp",EDGE,"E25"),sQuery(id+"F1.wireOp",EDGE,"E26"),sQuery(id+"F1.wireOp",EDGE,"E27"),sQuery(id+"F1.wireOp",EDGE,"E28"),sQuery(id+"F1.wireOp",EDGE,"E29")])],"isStart":false});Q29=makeQuery(id+"F35.opBoolean","SPLIT",FACE,{"disambiguationData":[TD([makeQuery(id+"F12.opPattern","COPY",FACE,{"derivedFrom":makeQuery(id+"F2.opExtrude","SWEPT_FACE",FACE,{"disambiguationData":[OSD([subQ2])]}),"instanceName":"5"})])],"derivedFrom":makeQuery(id+"F12.opPattern","COPY",FACE,{"derivedFrom":makeQuery(id+"F4.boolean.opBoolean","MERGE",FACE,{"derivedFrom":[subQ8,makeQuery(id+"F4.opPattern","COPY",FACE,{"derivedFrom":subQ8,"instanceName":"1"})]}),"instanceName":"5"})});}
            var Q30;
            {var subQ0=sQuery(id+"F5.wireOp",EDGE,"E53");Q30=makeQuery(id+"F12.opPattern","COPY",FACE,{"derivedFrom":makeQuery(id+"F8.boolean.opBoolean","MERGE",FACE,{"derivedFrom":[makeQuery(id+"F6.boolean.opBoolean","COPY",FACE,{"derivedFrom":makeQuery(id+"F6.opExtrude","CAP_FACE",FACE,{"disambiguationData":[OSD([sQuery(id+"F5.wireOp",EDGE,"E30"),sQuery(id+"F5.wireOp",EDGE,"E32"),sQuery(id+"F5.wireOp",EDGE,"E33"),sQuery(id+"F5.wireOp",EDGE,"E34"),sQuery(id+"F5.wireOp",EDGE,"E35"),sQuery(id+"F5.wireOp",EDGE,"E36"),sQuery(id+"F5.wireOp",EDGE,"E37"),sQuery(id+"F5.wireOp",EDGE,"E38.trimOffspring"),sQuery(id+"F5.wireOp",EDGE,"E39"),sQuery(id+"F5.wireOp",EDGE,"E40"),sQuery(id+"F5.wireOp",EDGE,"E41"),sQuery(id+"F5.wireOp",EDGE,"E42"),sQuery(id+"F5.wireOp",EDGE,"E43"),sQuery(id+"F5.wireOp",EDGE,"E44"),sQuery(id+"F5.wireOp",EDGE,"E45"),sQuery(id+"F5.wireOp",EDGE,"E46"),sQuery(id+"F5.wireOp",EDGE,"E47"),subQ0,sQuery(id+"F5.wireOp",EDGE,"E54")])],"isStart":false})}),makeQuery(id+"F8.opExtrude","CAP_FACE",FACE,{"disambiguationData":[OSD([subQ0,sQuery(id+"F7.wireOp",EDGE,"E55"),sQuery(id+"F7.wireOp",EDGE,"E56"),sQuery(id+"F7.wireOp",EDGE,"E57"),sQuery(id+"F7.wireOp",EDGE,"E58.right"),sQuery(id+"F7.wireOp",EDGE,"E62"),sQuery(id+"F7.wireOp",EDGE,"E65"),sQuery(id+"F7.wireOp",EDGE,"E66"),sQuery(id+"F7.wireOp",EDGE,"E67"),sQuery(id+"F7.wireOp",EDGE,"E68"),sQuery(id+"F7.wireOp",EDGE,"E69"),sQuery(id+"F7.wireOp",EDGE,"E70"),sQuery(id+"F7.wireOp",EDGE,"E72"),sQuery(id+"F7.wireOp",EDGE,"E74"),sQuery(id+"F7.wireOp",EDGE,"E75"),sQuery(id+"F7.wireOp",EDGE,"E76.trimOffspring")])],"isStart":false})]}),"instanceName":"4"});}
            var Q31;
            Q31=makeQuery(id+"F12.opPattern","COPY",FACE,{"derivedFrom":makeQuery(id+"F6.boolean.opBoolean","COPY",FACE,{"derivedFrom":makeQuery(id+"F6.opExtrude","CAP_FACE",FACE,{"disambiguationData":[OSD([sQuery(id+"F5.wireOp",EDGE,"E48"),sQuery(id+"F5.wireOp",EDGE,"E49"),sQuery(id+"F5.wireOp",EDGE,"E50"),sQuery(id+"F5.wireOp",EDGE,"E51"),sQuery(id+"F5.wireOp",EDGE,"E52")])],"isStart":false})}),"instanceName":"4"});
            var Q32;
            Q32=makeQuery(id+"F12.opPattern","COPY",FACE,{"derivedFrom":makeQuery(id+"F8.boolean.opBoolean","COPY",FACE,{"derivedFrom":makeQuery(id+"F8.opExtrude","CAP_FACE",FACE,{"disambiguationData":[OSD([sQuery(id+"F7.wireOp",EDGE,"E77"),sQuery(id+"F7.wireOp",EDGE,"E78"),sQuery(id+"F7.wireOp",EDGE,"E79"),sQuery(id+"F7.wireOp",EDGE,"E80")])],"isStart":false})}),"instanceName":"4"});
            var Q33;
            {var subQ2=sQuery(id+"F1.wireOp",EDGE,"E13");var subQ3=sQuery(id+"F1.wireOp",EDGE,"E12");var subQ5=sQuery(id+"F1.wireOp",EDGE,"E11");var subQ6=sQuery(id+"F1.wireOp",EDGE,"E4");var subQ7=sQuery(id+"F1.wireOp",EDGE,"E2");var subQ8=makeQuery(id+"F2.opExtrude","CAP_FACE",FACE,{"disambiguationData":[OSD([sQuery(id+"F1.wireOp",EDGE,"E1"),subQ7,sQuery(id+"F1.wireOp",EDGE,"E3"),subQ6,sQuery(id+"F1.wireOp",EDGE,"E5"),sQuery(id+"F1.wireOp",EDGE,"E6"),sQuery(id+"F1.wireOp",EDGE,"E7"),sQuery(id+"F1.wireOp",EDGE,"E8"),sQuery(id+"F1.wireOp",EDGE,"E9"),sQuery(id+"F1.wireOp",EDGE,"E10"),subQ5,subQ3,subQ2,sQuery(id+"F1.wireOp",EDGE,"E14"),sQuery(id+"F1.wireOp",EDGE,"E15"),sQuery(id+"F1.wireOp",EDGE,"E16"),sQuery(id+"F1.wireOp",EDGE,"E17"),sQuery(id+"F1.wireOp",EDGE,"E18.trimOffspring"),sQuery(id+"F1.wireOp",EDGE,"E19"),sQuery(id+"F1.wireOp",EDGE,"E20"),sQuery(id+"F1.wireOp",EDGE,"E21"),sQuery(id+"F1.wireOp",EDGE,"E22"),sQuery(id+"F1.wireOp",EDGE,"E23"),sQuery(id+"F1.wireOp",EDGE,"E24"),sQuery(id+"F1.wireOp",EDGE,"E25"),sQuery(id+"F1.wireOp",EDGE,"E26"),sQuery(id+"F1.wireOp",EDGE,"E27"),sQuery(id+"F1.wireOp",EDGE,"E28"),sQuery(id+"F1.wireOp",EDGE,"E29")])],"isStart":false});Q33=makeQuery(id+"F35.opBoolean","SPLIT",FACE,{"disambiguationData":[TD([makeQuery(id+"F12.opPattern","COPY",FACE,{"derivedFrom":makeQuery(id+"F4.opPattern","COPY",FACE,{"derivedFrom":makeQuery(id+"F2.opExtrude","SWEPT_FACE",FACE,{"disambiguationData":[OSD([subQ2])]}),"instanceName":"1"}),"instanceName":"4"})])],"derivedFrom":makeQuery(id+"F12.opPattern","COPY",FACE,{"derivedFrom":makeQuery(id+"F4.boolean.opBoolean","MERGE",FACE,{"derivedFrom":[subQ8,makeQuery(id+"F4.opPattern","COPY",FACE,{"derivedFrom":subQ8,"instanceName":"1"})]}),"instanceName":"4"})});}
            var Q34;
            {var subQ0=sQuery(id+"F1.wireOp",EDGE,"E16");var subQ1=sQuery(id+"F1.wireOp",EDGE,"E8");var subQ3=sQuery(id+"F1.wireOp",EDGE,"E14");var subQ4=sQuery(id+"F1.wireOp",EDGE,"E7");var subQ6=sQuery(id+"F1.wireOp",EDGE,"E17");var subQ8=sQuery(id+"F1.wireOp",EDGE,"E15");var subQ10=sQuery(id+"F1.wireOp",EDGE,"E29");var subQ12=sQuery(id+"F1.wireOp",EDGE,"E28");var subQ14=sQuery(id+"F1.wireOp",EDGE,"E27");var subQ16=sQuery(id+"F1.wireOp",EDGE,"E26");var subQ18=sQuery(id+"F1.wireOp",EDGE,"E25");var subQ20=sQuery(id+"F1.wireOp",EDGE,"E24");var subQ22=sQuery(id+"F1.wireOp",EDGE,"E23");var subQ24=sQuery(id+"F1.wireOp",EDGE,"E22");var subQ26=sQuery(id+"F1.wireOp",EDGE,"E21");var subQ28=sQuery(id+"F1.wireOp",EDGE,"E19");var subQ30=sQuery(id+"F1.wireOp",EDGE,"E18.trimOffspring");var subQ32=sQuery(id+"F1.wireOp",EDGE,"E10");var subQ34=sQuery(id+"F1.wireOp",EDGE,"E6");var subQ35=makeQuery(id+"F2.opExtrude","SWEPT_FACE",FACE,{"disambiguationData":[OSD([subQ34])]});var subQ38=sQuery(id+"F1.wireOp",EDGE,"E9");var subQ45=makeQuery(id+"F2.opExtrude","CAP_FACE",FACE,{"disambiguationData":[OSD([sQuery(id+"F1.wireOp",EDGE,"E1"),sQuery(id+"F1.wireOp",EDGE,"E2"),sQuery(id+"F1.wireOp",EDGE,"E3"),sQuery(id+"F1.wireOp",EDGE,"E4"),sQuery(id+"F1.wireOp",EDGE,"E5"),subQ34,subQ4,subQ1,subQ38,subQ32,sQuery(id+"F1.wireOp",EDGE,"E11"),sQuery(id+"F1.wireOp",EDGE,"E12"),sQuery(id+"F1.wireOp",EDGE,"E13"),subQ3,subQ8,subQ0,subQ6,subQ30,subQ28,sQuery(id+"F1.wireOp",EDGE,"E20"),subQ26,subQ24,subQ22,subQ20,subQ18,subQ16,subQ14,subQ12,subQ10])],"isStart":false});Q34=makeQuery(id+"F35.opBoolean","SPLIT",FACE,{"disambiguationData":[TD([makeQuery(id+"F12.opPattern","COPY",FACE,{"derivedFrom":subQ35,"instanceName":"4"})])],"derivedFrom":makeQuery(id+"F12.opPattern","COPY",FACE,{"derivedFrom":makeQuery(id+"F4.boolean.opBoolean","MERGE",FACE,{"derivedFrom":[subQ45,makeQuery(id+"F4.opPattern","COPY",FACE,{"derivedFrom":subQ45,"instanceName":"1"})]}),"instanceName":"4"})});}
            var Q35;
            {var subQ2=sQuery(id+"F1.wireOp",EDGE,"E13");var subQ3=sQuery(id+"F1.wireOp",EDGE,"E11");var subQ5=sQuery(id+"F1.wireOp",EDGE,"E12");var subQ6=sQuery(id+"F1.wireOp",EDGE,"E4");var subQ7=sQuery(id+"F1.wireOp",EDGE,"E2");var subQ8=makeQuery(id+"F2.opExtrude","CAP_FACE",FACE,{"disambiguationData":[OSD([sQuery(id+"F1.wireOp",EDGE,"E1"),subQ7,sQuery(id+"F1.wireOp",EDGE,"E3"),subQ6,sQuery(id+"F1.wireOp",EDGE,"E5"),sQuery(id+"F1.wireOp",EDGE,"E6"),sQuery(id+"F1.wireOp",EDGE,"E7"),sQuery(id+"F1.wireOp",EDGE,"E8"),sQuery(id+"F1.wireOp",EDGE,"E9"),sQuery(id+"F1.wireOp",EDGE,"E10"),subQ3,subQ5,subQ2,sQuery(id+"F1.wireOp",EDGE,"E14"),sQuery(id+"F1.wireOp",EDGE,"E15"),sQuery(id+"F1.wireOp",EDGE,"E16"),sQuery(id+"F1.wireOp",EDGE,"E17"),sQuery(id+"F1.wireOp",EDGE,"E18.trimOffspring"),sQuery(id+"F1.wireOp",EDGE,"E19"),sQuery(id+"F1.wireOp",EDGE,"E20"),sQuery(id+"F1.wireOp",EDGE,"E21"),sQuery(id+"F1.wireOp",EDGE,"E22"),sQuery(id+"F1.wireOp",EDGE,"E23"),sQuery(id+"F1.wireOp",EDGE,"E24"),sQuery(id+"F1.wireOp",EDGE,"E25"),sQuery(id+"F1.wireOp",EDGE,"E26"),sQuery(id+"F1.wireOp",EDGE,"E27"),sQuery(id+"F1.wireOp",EDGE,"E28"),sQuery(id+"F1.wireOp",EDGE,"E29")])],"isStart":false});Q35=makeQuery(id+"F35.opBoolean","SPLIT",FACE,{"disambiguationData":[TD([makeQuery(id+"F12.opPattern","COPY",FACE,{"derivedFrom":makeQuery(id+"F2.opExtrude","SWEPT_FACE",FACE,{"disambiguationData":[OSD([subQ2])]}),"instanceName":"4"})])],"derivedFrom":makeQuery(id+"F12.opPattern","COPY",FACE,{"derivedFrom":makeQuery(id+"F4.boolean.opBoolean","MERGE",FACE,{"derivedFrom":[subQ8,makeQuery(id+"F4.opPattern","COPY",FACE,{"derivedFrom":subQ8,"instanceName":"1"})]}),"instanceName":"4"})});}
            extrude(context, id + "F36", {"entities" : qUnion([Q0, Q1, Q2, Q3, Q4, Q5, Q6, Q7, Q8, Q9, Q10, Q11, Q12, Q13, Q14, Q15, Q16, Q17, Q18, Q19, Q20, Q21, Q22, Q23, Q24, Q25, Q26, Q27, Q28, Q29, Q30, Q31, Q32, Q33, Q34, Q35]), "operationType" : NewBodyOperationType.ADD, "depth" : 1 * mm});
        }
        {
            var Q0;
            {var subQ0=sQuery(id+"F1.wireOp",EDGE,"E16");var subQ1=sQuery(id+"F1.wireOp",EDGE,"E8");var subQ3=sQuery(id+"F1.wireOp",EDGE,"E14");var subQ4=sQuery(id+"F1.wireOp",EDGE,"E7");var subQ6=sQuery(id+"F1.wireOp",EDGE,"E17");var subQ8=sQuery(id+"F1.wireOp",EDGE,"E15");var subQ10=sQuery(id+"F1.wireOp",EDGE,"E27");var subQ12=sQuery(id+"F1.wireOp",EDGE,"E26");var subQ14=sQuery(id+"F1.wireOp",EDGE,"E25");var subQ16=sQuery(id+"F1.wireOp",EDGE,"E24");var subQ18=sQuery(id+"F1.wireOp",EDGE,"E23");var subQ20=sQuery(id+"F1.wireOp",EDGE,"E22");var subQ22=sQuery(id+"F1.wireOp",EDGE,"E19");var subQ24=sQuery(id+"F1.wireOp",EDGE,"E10");var subQ26=sQuery(id+"F1.wireOp",EDGE,"E6");var subQ27=makeQuery(id+"F2.opExtrude","SWEPT_FACE",FACE,{"disambiguationData":[OSD([subQ26])]});var subQ30=sQuery(id+"F1.wireOp",EDGE,"E9");var subQ33=sQuery(id+"F1.wireOp",EDGE,"E18.trimOffspring");var subQ39=sQuery(id+"F15.wireOp",EDGE,"E84");var subQ40=sQuery(id+"F1.wireOp",EDGE,"E29");var subQ41=sQuery(id+"F1.wireOp",EDGE,"E28");var subQ42=sQuery(id+"F1.wireOp",EDGE,"E21");var subQ43=sQuery(id+"F1.wireOp",EDGE,"E20");var subQ44=sQuery(id+"F1.wireOp",EDGE,"E13");var subQ45=sQuery(id+"F1.wireOp",EDGE,"E12");var subQ46=sQuery(id+"F1.wireOp",EDGE,"E11");var subQ47=sQuery(id+"F1.wireOp",EDGE,"E5");var subQ48=sQuery(id+"F1.wireOp",EDGE,"E4");var subQ49=sQuery(id+"F1.wireOp",EDGE,"E3");var subQ50=sQuery(id+"F1.wireOp",EDGE,"E2");var subQ51=sQuery(id+"F1.wireOp",EDGE,"E1");var subQ52=makeQuery(id+"F2.opExtrude","CAP_FACE",FACE,{"disambiguationData":[OSD([subQ51,subQ50,subQ49,subQ48,subQ47,subQ26,subQ4,subQ1,subQ30,subQ24,subQ46,subQ45,subQ44,subQ3,subQ8,subQ0,subQ6,subQ33,subQ22,subQ43,subQ42,subQ20,subQ18,subQ16,subQ14,subQ12,subQ10,subQ41,subQ40])],"isStart":false});Q0=makeQuery(id+"F36.opExtrude","CAP_FACE",FACE,{"disambiguationData":[OSD([subQ51,subQ50,subQ49,subQ48,subQ47,subQ26,subQ4,subQ1,subQ30,subQ24,subQ46,subQ45,subQ44,subQ3,subQ8,subQ0,subQ6,subQ33,subQ22,subQ43,subQ42,subQ20,subQ18,subQ16,subQ14,subQ12,subQ10,subQ41,subQ40,subQ39]),TDD([makeQuery(id+"F35.opBoolean","SPLIT",FACE,{"disambiguationData":[TD([makeQuery(id+"F12.opPattern","COPY",FACE,{"derivedFrom":subQ27,"instanceName":"3"})])],"derivedFrom":makeQuery(id+"F16.boolean.opBoolean","MERGE",FACE,{"derivedFrom":[makeQuery(id+"F12.opPattern","COPY",FACE,{"derivedFrom":makeQuery(id+"F4.boolean.opBoolean","MERGE",FACE,{"derivedFrom":[subQ52,makeQuery(id+"F4.opPattern","COPY",FACE,{"derivedFrom":subQ52,"instanceName":"1"})]}),"instanceName":"3"}),makeQuery(id+"F16.opExtrude","CAP_FACE",FACE,{"disambiguationData":[OSD([subQ39])],"isStart":true})]})})])],"isStart":false});}
            var sketch = newSketch(context, id + "F37", { "sketchPlane" : qUnion([Q0])});
            skCircle(sketch, "E588", {"center": v(-37.62, 60.79) * mm, "radius": 5.51 * mm});
            skPoint(sketch, "E588.first.point", {"position": v(-37.62, 66.3) * mm});
            skPoint(sketch, "E588.second.point", {"position": v(-37.58, 55.28) * mm});
            skPoint(sketch, "E588.second.point.positionSnap0", {"position": v(-37.66, 55.28) * mm});
            skPoint(sketch, "E588.third.point", {"position": v(-32.7, 63.25) * mm});
            skCircle(sketch, "E589", {"center": v(-37.62, 60.79) * mm, "radius": 3.04 * mm});
            skSolve(sketch);
        }
        {
            var Q0;
            Q0 = qSketchRegion(id + "F37", true);
            extrude(context, id + "F38", {"entities" : qUnion([Q0]), "operationType" : NewBodyOperationType.ADD, "oppositeDirection" : true, "depth" : 2.5 * mm});
        }
        {
            var Q0;
            {var subQ0=makeQuery(id+"F2.opExtrude","CAP_FACE",FACE,{"disambiguationData":[OSD([sQuery(id+"F1.wireOp",EDGE,"E1"),sQuery(id+"F1.wireOp",EDGE,"E2"),sQuery(id+"F1.wireOp",EDGE,"E3"),sQuery(id+"F1.wireOp",EDGE,"E4"),sQuery(id+"F1.wireOp",EDGE,"E5"),sQuery(id+"F1.wireOp",EDGE,"E6"),sQuery(id+"F1.wireOp",EDGE,"E7"),sQuery(id+"F1.wireOp",EDGE,"E8"),sQuery(id+"F1.wireOp",EDGE,"E9"),sQuery(id+"F1.wireOp",EDGE,"E10"),sQuery(id+"F1.wireOp",EDGE,"E11"),sQuery(id+"F1.wireOp",EDGE,"E12"),sQuery(id+"F1.wireOp",EDGE,"E13"),sQuery(id+"F1.wireOp",EDGE,"E14"),sQuery(id+"F1.wireOp",EDGE,"E15"),sQuery(id+"F1.wireOp",EDGE,"E16"),sQuery(id+"F1.wireOp",EDGE,"E17"),sQuery(id+"F1.wireOp",EDGE,"E18.trimOffspring"),sQuery(id+"F1.wireOp",EDGE,"E19"),sQuery(id+"F1.wireOp",EDGE,"E20"),sQuery(id+"F1.wireOp",EDGE,"E21"),sQuery(id+"F1.wireOp",EDGE,"E22"),sQuery(id+"F1.wireOp",EDGE,"E23"),sQuery(id+"F1.wireOp",EDGE,"E24"),sQuery(id+"F1.wireOp",EDGE,"E25"),sQuery(id+"F1.wireOp",EDGE,"E26"),sQuery(id+"F1.wireOp",EDGE,"E27"),sQuery(id+"F1.wireOp",EDGE,"E28"),sQuery(id+"F1.wireOp",EDGE,"E29")])],"isStart":true});var subQ1=makeQuery(id+"F4.boolean.opBoolean","MERGE",FACE,{"derivedFrom":[subQ0,makeQuery(id+"F4.opPattern","COPY",FACE,{"derivedFrom":subQ0,"instanceName":"1"})]});Q0=makeQuery(id+"F35.opBoolean","MERGE",FACE,{"disambiguationData":[OD(7.0)],"derivedFrom":[subQ1,makeQuery(id+"F12.opPattern","COPY",FACE,{"derivedFrom":subQ1,"instanceName":"1"}),makeQuery(id+"F12.opPattern","COPY",FACE,{"derivedFrom":subQ1,"instanceName":"2"}),makeQuery(id+"F12.opPattern","COPY",FACE,{"derivedFrom":subQ1,"instanceName":"4"}),makeQuery(id+"F12.opPattern","COPY",FACE,{"derivedFrom":subQ1,"instanceName":"5"}),makeQuery(id+"F16.boolean.opBoolean","MERGE",FACE,{"derivedFrom":[makeQuery(id+"F12.opPattern","COPY",FACE,{"derivedFrom":subQ1,"instanceName":"3"}),makeQuery(id+"F16.opExtrude","CAP_FACE",FACE,{"disambiguationData":[OSD([sQuery(id+"F15.wireOp",EDGE,"E84")])],"isStart":false})]}),makeQuery(id+"F14.opExtrude","CAP_FACE",FACE,{"disambiguationData":[OSD([sQuery(id+"F13.wireOp",EDGE,"E83")])],"isStart":true})]});}
            var sketch = newSketch(context, id + "F39", { "sketchPlane" : qUnion([Q0])});
            skCircle(sketch, "E590", {"center": v(-37.64, -60.78) * mm, "radius": 5.52 * mm});
            skPoint(sketch, "E590.first.point", {"position": v(-37.62, -66.3) * mm});
            skPoint(sketch, "E590.second.point", {"position": v(-35.8, -55.57) * mm});
            skPoint(sketch, "E590.third.point", {"position": v(-40.14, -55.86) * mm});
            skCircle(sketch, "E591", {"center": v(-37.64, -60.78) * mm, "radius": 3.06 * mm});
            skPoint(sketch, "E591.first.point", {"position": v(-37.63, -57.72) * mm});
            skPoint(sketch, "E591.second.point", {"position": v(-37.57, -63.84) * mm});
            skPoint(sketch, "E591.third.point", {"position": v(-34.65, -60.14) * mm});
            skSolve(sketch);
        }
        {
            var Q0;
            Q0 = qSketchRegion(id + "F39", true);
            extrude(context, id + "F40", {"entities" : qUnion([Q0]), "operationType" : NewBodyOperationType.ADD, "oppositeDirection" : true, "depth" : 1 * mm});
        }
    });
